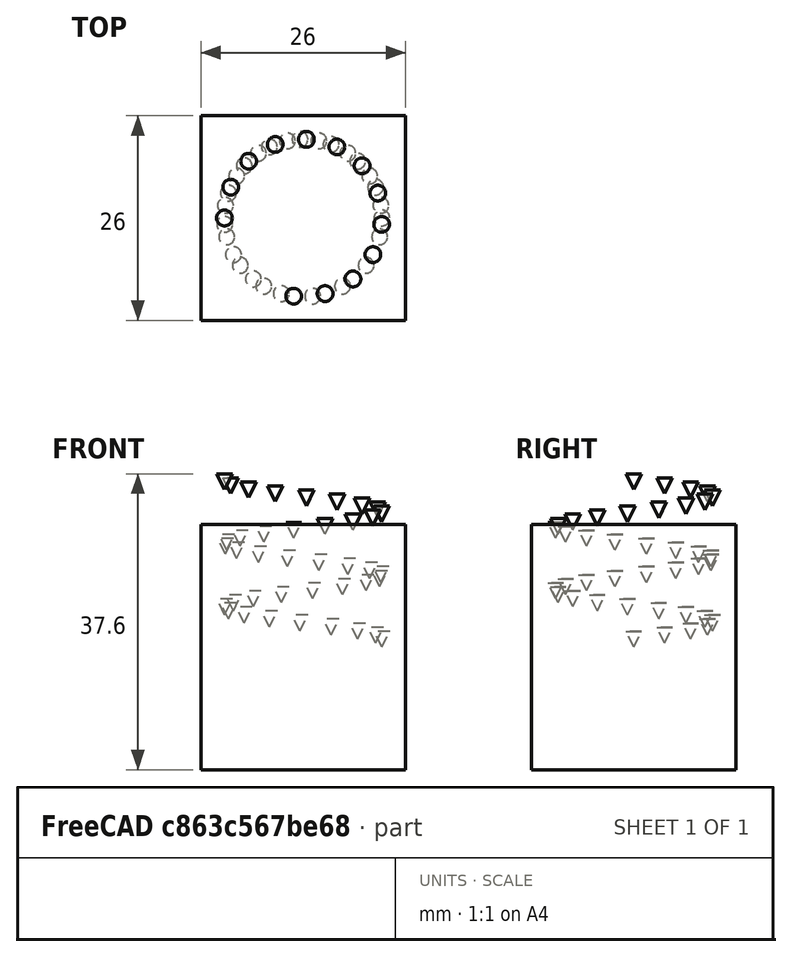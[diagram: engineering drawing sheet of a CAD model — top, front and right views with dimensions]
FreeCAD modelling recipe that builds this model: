
FCSTD DOCUMENT  (FreeCAD 0.21R33694 (Git))
Label: PathArray
License: All rights reserved
objects: App::DocumentObjectGroupPython×1251, Part::FeaturePython×2, App::Part×2, Part::Cone×1, Part::Helix×1
note: 4 computed .brp shape members not serialized (recipe doc carries the construction recipe); baked Part::Feature solids carry a one-line shape summary decoded from their .brp

FEATURE [App::DocumentObjectGroupPython] HALFPI  # scripted group (container) (typed FeaturePython)
  name = HALFPI
  value = pi/2.
FEATURE [App::DocumentObjectGroupPython] PI  # scripted group (container) (typed FeaturePython)
  name = PI
  value = 1.*pi
FEATURE [App::DocumentObjectGroupPython] TWOPI  # scripted group (container) (typed FeaturePython)
  name = TWOPI
  value = 2.*pi
FEATURE [App::DocumentObjectGroupPython] Constants  # scripted group (container) (typed FeaturePython)
  Group = -> [HALFPI,PI,TWOPI]
FEATURE [App::DocumentObjectGroupPython] Variables  # scripted group (container) (typed FeaturePython)
FEATURE [App::DocumentObjectGroupPython] Quantities  # scripted group (container) (typed FeaturePython)
FEATURE [App::DocumentObjectGroupPython] Isotopes  # scripted group (container) (typed FeaturePython)
FEATURE [App::DocumentObjectGroupPython] Elements  # scripted group (container) (typed FeaturePython)
FEATURE [App::DocumentObjectGroupPython] Matrix  # scripted group (container) (typed FeaturePython)
FEATURE [App::DocumentObjectGroupPython] Surfaces  # scripted group (container) (typed FeaturePython)
FEATURE [App::DocumentObjectGroupPython] Opticals  # scripted group (container) (typed FeaturePython)
  Group = -> [Matrix,Surfaces]
FEATURE [App::DocumentObjectGroupPython] G4Isotopes  # scripted group (container) (typed FeaturePython)
FEATURE [App::DocumentObjectGroupPython] H_element  # scripted group (container) (typed FeaturePython)
  Z = 1
  atom_value = 1.008
  formula = H
  name = H_element
FEATURE [App::DocumentObjectGroupPython] He_element  # scripted group (container) (typed FeaturePython)
  Z = 2
  atom_value = 4.0026
  formula = He
  name = He_element
FEATURE [App::DocumentObjectGroupPython] Li_element  # scripted group (container) (typed FeaturePython)
  Z = 3
  atom_value = 6.94
  formula = Li
  name = Li_element
FEATURE [App::DocumentObjectGroupPython] Be_element  # scripted group (container) (typed FeaturePython)
  Z = 4
  atom_value = 9.01218
  formula = Be
  name = Be_element
FEATURE [App::DocumentObjectGroupPython] B_element  # scripted group (container) (typed FeaturePython)
  Z = 5
  atom_value = 10.81
  formula = B
  name = B_element
FEATURE [App::DocumentObjectGroupPython] C_element  # scripted group (container) (typed FeaturePython)
  Z = 6
  atom_value = 12.011
  formula = C
  name = C_element
FEATURE [App::DocumentObjectGroupPython] N_element  # scripted group (container) (typed FeaturePython)
  Z = 7
  atom_value = 14.007
  formula = N
  name = N_element
FEATURE [App::DocumentObjectGroupPython] O_element  # scripted group (container) (typed FeaturePython)
  Z = 8
  atom_value = 15.999
  formula = O
  name = O_element
FEATURE [App::DocumentObjectGroupPython] F_element  # scripted group (container) (typed FeaturePython)
  Z = 9
  atom_value = 18.9984
  formula = F
  name = F_element
FEATURE [App::DocumentObjectGroupPython] Ne_element  # scripted group (container) (typed FeaturePython)
  Z = 10
  atom_value = 20.1797
  formula = Ne
  name = Ne_element
FEATURE [App::DocumentObjectGroupPython] Na_element  # scripted group (container) (typed FeaturePython)
  Z = 11
  atom_value = 22.9898
  formula = Na
  name = Na_element
FEATURE [App::DocumentObjectGroupPython] Mg_element  # scripted group (container) (typed FeaturePython)
  Z = 12
  atom_value = 24.305
  formula = Mg
  name = Mg_element
FEATURE [App::DocumentObjectGroupPython] Al_element  # scripted group (container) (typed FeaturePython)
  Z = 13
  atom_value = 26.9815
  formula = Al
  name = Al_element
FEATURE [App::DocumentObjectGroupPython] Si_element  # scripted group (container) (typed FeaturePython)
  Z = 14
  atom_value = 28.085
  formula = Si
  name = Si_element
FEATURE [App::DocumentObjectGroupPython] P_element  # scripted group (container) (typed FeaturePython)
  Z = 15
  atom_value = 30.9738
  formula = P
  name = P_element
FEATURE [App::DocumentObjectGroupPython] S_element  # scripted group (container) (typed FeaturePython)
  Z = 16
  atom_value = 32.06
  formula = S
  name = S_element
FEATURE [App::DocumentObjectGroupPython] Cl_element  # scripted group (container) (typed FeaturePython)
  Z = 17
  atom_value = 35.45
  formula = Cl
  name = Cl_element
FEATURE [App::DocumentObjectGroupPython] Ar_element  # scripted group (container) (typed FeaturePython)
  Z = 18
  atom_value = 39.95
  formula = Ar
  name = Ar_element
FEATURE [App::DocumentObjectGroupPython] K_element  # scripted group (container) (typed FeaturePython)
  Z = 19
  atom_value = 39.0983
  formula = K
  name = K_element
FEATURE [App::DocumentObjectGroupPython] Ca_element  # scripted group (container) (typed FeaturePython)
  Z = 20
  atom_value = 40.078
  formula = Ca
  name = Ca_element
FEATURE [App::DocumentObjectGroupPython] Sc_element  # scripted group (container) (typed FeaturePython)
  Z = 21
  atom_value = 44.9559
  formula = Sc
  name = Sc_element
FEATURE [App::DocumentObjectGroupPython] Ti_element  # scripted group (container) (typed FeaturePython)
  Z = 22
  atom_value = 47.867
  formula = Ti
  name = Ti_element
FEATURE [App::DocumentObjectGroupPython] V_element  # scripted group (container) (typed FeaturePython)
  Z = 23
  atom_value = 50.9415
  formula = V
  name = V_element
FEATURE [App::DocumentObjectGroupPython] Cr_element  # scripted group (container) (typed FeaturePython)
  Z = 24
  atom_value = 51.9961
  formula = Cr
  name = Cr_element
FEATURE [App::DocumentObjectGroupPython] Mn_element  # scripted group (container) (typed FeaturePython)
  Z = 25
  atom_value = 54.938
  formula = Mn
  name = Mn_element
FEATURE [App::DocumentObjectGroupPython] Fe_element  # scripted group (container) (typed FeaturePython)
  Z = 26
  atom_value = 55.845
  formula = Fe
  name = Fe_element
FEATURE [App::DocumentObjectGroupPython] Co_element  # scripted group (container) (typed FeaturePython)
  Z = 27
  atom_value = 58.9332
  formula = Co
  name = Co_element
FEATURE [App::DocumentObjectGroupPython] Ni_element  # scripted group (container) (typed FeaturePython)
  Z = 28
  atom_value = 58.6934
  formula = Ni
  name = Ni_element
FEATURE [App::DocumentObjectGroupPython] Cu_element  # scripted group (container) (typed FeaturePython)
  Z = 29
  atom_value = 63.546
  formula = Cu
  name = Cu_element
FEATURE [App::DocumentObjectGroupPython] Zn_element  # scripted group (container) (typed FeaturePython)
  Z = 30
  atom_value = 65.38
  formula = Zn
  name = Zn_element
FEATURE [App::DocumentObjectGroupPython] Ga_element  # scripted group (container) (typed FeaturePython)
  Z = 31
  atom_value = 69.723
  formula = Ga
  name = Ga_element
FEATURE [App::DocumentObjectGroupPython] Ge_element  # scripted group (container) (typed FeaturePython)
  Z = 32
  atom_value = 72.63
  formula = Ge
  name = Ge_element
FEATURE [App::DocumentObjectGroupPython] As_element  # scripted group (container) (typed FeaturePython)
  Z = 33
  atom_value = 74.9216
  formula = As
  name = As_element
FEATURE [App::DocumentObjectGroupPython] Se_element  # scripted group (container) (typed FeaturePython)
  Z = 34
  atom_value = 78.971
  formula = Se
  name = Se_element
FEATURE [App::DocumentObjectGroupPython] Br_element  # scripted group (container) (typed FeaturePython)
  Z = 35
  atom_value = 79.904
  formula = Br
  name = Br_element
FEATURE [App::DocumentObjectGroupPython] Kr_element  # scripted group (container) (typed FeaturePython)
  Z = 36
  atom_value = 83.798
  formula = Kr
  name = Kr_element
FEATURE [App::DocumentObjectGroupPython] Rb_element  # scripted group (container) (typed FeaturePython)
  Z = 37
  atom_value = 85.4678
  formula = Rb
  name = Rb_element
FEATURE [App::DocumentObjectGroupPython] Sr_element  # scripted group (container) (typed FeaturePython)
  Z = 38
  atom_value = 87.62
  formula = Sr
  name = Sr_element
FEATURE [App::DocumentObjectGroupPython] Y_element  # scripted group (container) (typed FeaturePython)
  Z = 39
  atom_value = 88.9058
  formula = Y
  name = Y_element
FEATURE [App::DocumentObjectGroupPython] Zr_element  # scripted group (container) (typed FeaturePython)
  Z = 40
  atom_value = 91.224
  formula = Zr
  name = Zr_element
FEATURE [App::DocumentObjectGroupPython] Nb_element  # scripted group (container) (typed FeaturePython)
  Z = 41
  atom_value = 92.9064
  formula = Nb
  name = Nb_element
FEATURE [App::DocumentObjectGroupPython] Mo_element  # scripted group (container) (typed FeaturePython)
  Z = 42
  atom_value = 95.95
  formula = Mo
  name = Mo_element
FEATURE [App::DocumentObjectGroupPython] Tc_element  # scripted group (container) (typed FeaturePython)
  Z = 43
  atom_value = 97
  formula = Tc
  name = Tc_element
FEATURE [App::DocumentObjectGroupPython] Ru_element  # scripted group (container) (typed FeaturePython)
  Z = 44
  atom_value = 101.07
  formula = Ru
  name = Ru_element
FEATURE [App::DocumentObjectGroupPython] Rh_element  # scripted group (container) (typed FeaturePython)
  Z = 45
  atom_value = 102.905
  formula = Rh
  name = Rh_element
FEATURE [App::DocumentObjectGroupPython] Pd_element  # scripted group (container) (typed FeaturePython)
  Z = 46
  atom_value = 106.42
  formula = Pd
  name = Pd_element
FEATURE [App::DocumentObjectGroupPython] Ag_element  # scripted group (container) (typed FeaturePython)
  Z = 47
  atom_value = 107.868
  formula = Ag
  name = Ag_element
FEATURE [App::DocumentObjectGroupPython] Cd_element  # scripted group (container) (typed FeaturePython)
  Z = 48
  atom_value = 112.414
  formula = Cd
  name = Cd_element
FEATURE [App::DocumentObjectGroupPython] In_element  # scripted group (container) (typed FeaturePython)
  Z = 49
  atom_value = 114.818
  formula = In
  name = In_element
FEATURE [App::DocumentObjectGroupPython] Sn_element  # scripted group (container) (typed FeaturePython)
  Z = 50
  atom_value = 118.71
  formula = Sn
  name = Sn_element
FEATURE [App::DocumentObjectGroupPython] Sb_element  # scripted group (container) (typed FeaturePython)
  Z = 51
  atom_value = 121.76
  formula = Sb
  name = Sb_element
FEATURE [App::DocumentObjectGroupPython] Te_element  # scripted group (container) (typed FeaturePython)
  Z = 52
  atom_value = 127.6
  formula = Te
  name = Te_element
FEATURE [App::DocumentObjectGroupPython] I_element  # scripted group (container) (typed FeaturePython)
  Z = 53
  atom_value = 126.904
  formula = I
  name = I_element
FEATURE [App::DocumentObjectGroupPython] Xe_element  # scripted group (container) (typed FeaturePython)
  Z = 54
  atom_value = 131.293
  formula = Xe
  name = Xe_element
FEATURE [App::DocumentObjectGroupPython] Cs_element  # scripted group (container) (typed FeaturePython)
  Z = 55
  atom_value = 132.905
  formula = Cs
  name = Cs_element
FEATURE [App::DocumentObjectGroupPython] Ba_element  # scripted group (container) (typed FeaturePython)
  Z = 56
  atom_value = 137.327
  formula = Ba
  name = Ba_element
FEATURE [App::DocumentObjectGroupPython] La_element  # scripted group (container) (typed FeaturePython)
  Z = 57
  atom_value = 138.905
  formula = La
  name = La_element
FEATURE [App::DocumentObjectGroupPython] Ce_element  # scripted group (container) (typed FeaturePython)
  Z = 58
  atom_value = 140.116
  formula = Ce
  name = Ce_element
FEATURE [App::DocumentObjectGroupPython] Pr_element  # scripted group (container) (typed FeaturePython)
  Z = 59
  atom_value = 140.908
  formula = Pr
  name = Pr_element
FEATURE [App::DocumentObjectGroupPython] Nd_element  # scripted group (container) (typed FeaturePython)
  Z = 60
  atom_value = 144.242
  formula = Nd
  name = Nd_element
FEATURE [App::DocumentObjectGroupPython] Pm_element  # scripted group (container) (typed FeaturePython)
  Z = 61
  atom_value = 145
  formula = Pm
  name = Pm_element
FEATURE [App::DocumentObjectGroupPython] Sm_element  # scripted group (container) (typed FeaturePython)
  Z = 62
  atom_value = 150.36
  formula = Sm
  name = Sm_element
FEATURE [App::DocumentObjectGroupPython] Eu_element  # scripted group (container) (typed FeaturePython)
  Z = 63
  atom_value = 151.964
  formula = Eu
  name = Eu_element
FEATURE [App::DocumentObjectGroupPython] Gd_element  # scripted group (container) (typed FeaturePython)
  Z = 64
  atom_value = 157.25
  formula = Gd
  name = Gd_element
FEATURE [App::DocumentObjectGroupPython] Tb_element  # scripted group (container) (typed FeaturePython)
  Z = 65
  atom_value = 158.925
  formula = Tb
  name = Tb_element
FEATURE [App::DocumentObjectGroupPython] Dy_element  # scripted group (container) (typed FeaturePython)
  Z = 66
  atom_value = 162.5
  formula = Dy
  name = Dy_element
FEATURE [App::DocumentObjectGroupPython] Ho_element  # scripted group (container) (typed FeaturePython)
  Z = 67
  atom_value = 164.93
  formula = Ho
  name = Ho_element
FEATURE [App::DocumentObjectGroupPython] Er_element  # scripted group (container) (typed FeaturePython)
  Z = 68
  atom_value = 167.259
  formula = Er
  name = Er_element
FEATURE [App::DocumentObjectGroupPython] Tm_element  # scripted group (container) (typed FeaturePython)
  Z = 69
  atom_value = 168.934
  formula = Tm
  name = Tm_element
FEATURE [App::DocumentObjectGroupPython] Yb_element  # scripted group (container) (typed FeaturePython)
  Z = 70
  atom_value = 173.045
  formula = Yb
  name = Yb_element
FEATURE [App::DocumentObjectGroupPython] Lu_element  # scripted group (container) (typed FeaturePython)
  Z = 71
  atom_value = 174.967
  formula = Lu
  name = Lu_element
FEATURE [App::DocumentObjectGroupPython] Hf_element  # scripted group (container) (typed FeaturePython)
  Z = 72
  atom_value = 178.49
  formula = Hf
  name = Hf_element
FEATURE [App::DocumentObjectGroupPython] Ta_element  # scripted group (container) (typed FeaturePython)
  Z = 73
  atom_value = 180.948
  formula = Ta
  name = Ta_element
FEATURE [App::DocumentObjectGroupPython] W_element  # scripted group (container) (typed FeaturePython)
  Z = 74
  atom_value = 183.84
  formula = W
  name = W_element
FEATURE [App::DocumentObjectGroupPython] Re_element  # scripted group (container) (typed FeaturePython)
  Z = 75
  atom_value = 186.207
  formula = Re
  name = Re_element
FEATURE [App::DocumentObjectGroupPython] Os_element  # scripted group (container) (typed FeaturePython)
  Z = 76
  atom_value = 190.23
  formula = Os
  name = Os_element
FEATURE [App::DocumentObjectGroupPython] Ir_element  # scripted group (container) (typed FeaturePython)
  Z = 77
  atom_value = 192.217
  formula = Ir
  name = Ir_element
FEATURE [App::DocumentObjectGroupPython] Pt_element  # scripted group (container) (typed FeaturePython)
  Z = 78
  atom_value = 195.084
  formula = Pt
  name = Pt_element
FEATURE [App::DocumentObjectGroupPython] Au_element  # scripted group (container) (typed FeaturePython)
  Z = 79
  atom_value = 196.967
  formula = Au
  name = Au_element
FEATURE [App::DocumentObjectGroupPython] Hg_element  # scripted group (container) (typed FeaturePython)
  Z = 80
  atom_value = 200.592
  formula = Hg
  name = Hg_element
FEATURE [App::DocumentObjectGroupPython] Tl_element  # scripted group (container) (typed FeaturePython)
  Z = 81
  atom_value = 204.38
  formula = Tl
  name = Tl_element
FEATURE [App::DocumentObjectGroupPython] Pb_element  # scripted group (container) (typed FeaturePython)
  Z = 82
  atom_value = 207.2
  formula = Pb
  name = Pb_element
FEATURE [App::DocumentObjectGroupPython] Bi_element  # scripted group (container) (typed FeaturePython)
  Z = 83
  atom_value = 208.98
  formula = Bi
  name = Bi_element
FEATURE [App::DocumentObjectGroupPython] Po_element  # scripted group (container) (typed FeaturePython)
  Z = 84
  atom_value = 209
  formula = Po
  name = Po_element
FEATURE [App::DocumentObjectGroupPython] At_element  # scripted group (container) (typed FeaturePython)
  Z = 85
  atom_value = 210
  formula = At
  name = At_element
FEATURE [App::DocumentObjectGroupPython] Rn_element  # scripted group (container) (typed FeaturePython)
  Z = 86
  atom_value = 222
  formula = Rn
  name = Rn_element
FEATURE [App::DocumentObjectGroupPython] Fr_element  # scripted group (container) (typed FeaturePython)
  Z = 87
  atom_value = 223
  formula = Fr
  name = Fr_element
FEATURE [App::DocumentObjectGroupPython] Ra_element  # scripted group (container) (typed FeaturePython)
  Z = 88
  atom_value = 226
  formula = Ra
  name = Ra_element
FEATURE [App::DocumentObjectGroupPython] Ac_element  # scripted group (container) (typed FeaturePython)
  Z = 89
  atom_value = 227
  formula = Ac
  name = Ac_element
FEATURE [App::DocumentObjectGroupPython] Th_element  # scripted group (container) (typed FeaturePython)
  Z = 90
  atom_value = 232.038
  formula = Th
  name = Th_element
FEATURE [App::DocumentObjectGroupPython] Pa_element  # scripted group (container) (typed FeaturePython)
  Z = 91
  atom_value = 231.036
  formula = Pa
  name = Pa_element
FEATURE [App::DocumentObjectGroupPython] U_element  # scripted group (container) (typed FeaturePython)
  Z = 92
  atom_value = 238.029
  formula = U
  name = U_element
FEATURE [App::DocumentObjectGroupPython] Np_element  # scripted group (container) (typed FeaturePython)
  Z = 93
  atom_value = 237
  formula = Np
  name = Np_element
FEATURE [App::DocumentObjectGroupPython] Pu_element  # scripted group (container) (typed FeaturePython)
  Z = 94
  atom_value = 244
  formula = Pu
  name = Pu_element
FEATURE [App::DocumentObjectGroupPython] Am_element  # scripted group (container) (typed FeaturePython)
  Z = 95
  atom_value = 243
  formula = Am
  name = Am_element
FEATURE [App::DocumentObjectGroupPython] Cm_element  # scripted group (container) (typed FeaturePython)
  Z = 96
  atom_value = 247
  formula = Cm
  name = Cm_element
FEATURE [App::DocumentObjectGroupPython] Bk_element  # scripted group (container) (typed FeaturePython)
  Z = 97
  atom_value = 247
  formula = Bk
  name = Bk_element
FEATURE [App::DocumentObjectGroupPython] Cf_element  # scripted group (container) (typed FeaturePython)
  Z = 98
  atom_value = 251
  formula = Cf
  name = Cf_element
FEATURE [App::DocumentObjectGroupPython] G4Elements  # scripted group (container) (typed FeaturePython)
  Group = -> [H_element,He_element,Li_element,Be_element,B_element,C_element,N_element,O_element,F_element,Ne_element,Na_element,Mg_element,Al_element,Si_element,P_element,S_element,Cl_element,Ar_element,K_element,Ca_element,Sc_element,Ti_element,V_element,Cr_element,Mn_element,Fe_element,Co_element,Ni_element,Cu_element,Zn_element,Ga_element,Ge_element,As_element,Se_element,Br_element,Kr_element,Rb_element,+61 more]
FEATURE [App::DocumentObjectGroupPython] H_element001  label="H_element : 0.101"  # scripted group (container) (typed FeaturePython)
  n = 0.101327
FEATURE [App::DocumentObjectGroupPython] C_element001  label="C_element : 0.775"  # scripted group (container) (typed FeaturePython)
  n = 0.7755
FEATURE [App::DocumentObjectGroupPython] N_element001  label="N_element : 0.035"  # scripted group (container) (typed FeaturePython)
  n = 0.035057
FEATURE [App::DocumentObjectGroupPython] O_element001  label="O_element : 0.052"  # scripted group (container) (typed FeaturePython)
  n = 0.0523159
FEATURE [App::DocumentObjectGroupPython] F_element001  label="F_element : 0.017"  # scripted group (container) (typed FeaturePython)
  n = 0.017422
FEATURE [App::DocumentObjectGroupPython] Ca_element001  label="Ca_element : 0.018"  # scripted group (container) (typed FeaturePython)
  n = 0.018378
FEATURE [App::DocumentObjectGroupPython] G4_A_150_TISSUE  label="G4_A-150_TISSUE"  # scripted group (container) (typed FeaturePython)
  Dunit = g/cm3
  Dvalue = 1.127
  Group = -> [H_element001,C_element001,N_element001,O_element001,F_element001,Ca_element001]
  conduct = 2
  density = 1
  expand = 3
  formula = G4_A-150_TISSUE
  name = G4_A-150_TISSUE
  specific = 4
FEATURE [App::DocumentObjectGroupPython] C_element002  label="C_element : 3"  # scripted group (container) (typed FeaturePython)
  n = 3
  ref = C_element
FEATURE [App::DocumentObjectGroupPython] H_element002  label="H_element : 6"  # scripted group (container) (typed FeaturePython)
  n = 6
  ref = H_element
FEATURE [App::DocumentObjectGroupPython] O_element002  label="O_element : 1"  # scripted group (container) (typed FeaturePython)
  n = 1
  ref = O_element
FEATURE [App::DocumentObjectGroupPython] G4_ACETONE  # scripted group (container) (typed FeaturePython)
  Dunit = g/cm3
  Dvalue = 0.7899
  Group = -> [C_element002,H_element002,O_element002]
  conduct = 2
  density = 1
  expand = 3
  formula = G4_ACETONE
  name = G4_ACETONE
  specific = 4
FEATURE [App::DocumentObjectGroupPython] C_element003  label="C_element : 2"  # scripted group (container) (typed FeaturePython)
  n = 2
  ref = C_element
FEATURE [App::DocumentObjectGroupPython] H_element003  label="H_element : 2"  # scripted group (container) (typed FeaturePython)
  n = 2
  ref = H_element
FEATURE [App::DocumentObjectGroupPython] G4_ACETYLENE  # scripted group (container) (typed FeaturePython)
  Dunit = g/cm3
  Dvalue = 0.0010967
  Group = -> [C_element003,H_element003]
  conduct = 2
  density = 1
  expand = 3
  formula = G4_ACETYLENE
  name = G4_ACETYLENE
  specific = 4
FEATURE [App::DocumentObjectGroupPython] C_element004  label="C_element : 5"  # scripted group (container) (typed FeaturePython)
  n = 5
  ref = C_element
FEATURE [App::DocumentObjectGroupPython] H_element004  label="H_element : 5"  # scripted group (container) (typed FeaturePython)
  n = 5
  ref = H_element
FEATURE [App::DocumentObjectGroupPython] N_element002  label="N_element : 5"  # scripted group (container) (typed FeaturePython)
  n = 5
  ref = N_element
FEATURE [App::DocumentObjectGroupPython] G4_ADENINE  # scripted group (container) (typed FeaturePython)
  Dunit = g/cm3
  Dvalue = 1.6
  Group = -> [C_element004,H_element004,N_element002]
  conduct = 2
  density = 1
  expand = 3
  formula = G4_ADENINE
  name = G4_ADENINE
  specific = 4
FEATURE [App::DocumentObjectGroupPython] H_element005  label="H_element : 0.114"  # scripted group (container) (typed FeaturePython)
  n = 0.114
FEATURE [App::DocumentObjectGroupPython] C_element005  label="C_element : 0.598"  # scripted group (container) (typed FeaturePython)
  n = 0.598
FEATURE [App::DocumentObjectGroupPython] N_element003  label="N_element : 0.007"  # scripted group (container) (typed FeaturePython)
  n = 0.007
FEATURE [App::DocumentObjectGroupPython] O_element003  label="O_element : 0.278"  # scripted group (container) (typed FeaturePython)
  n = 0.278
FEATURE [App::DocumentObjectGroupPython] Na_element001  label="Na_element : 0.001"  # scripted group (container) (typed FeaturePython)
  n = 0.001
FEATURE [App::DocumentObjectGroupPython] S_element001  label="S_element : 0.001"  # scripted group (container) (typed FeaturePython)
  n = 0.001
FEATURE [App::DocumentObjectGroupPython] Cl_element001  label="Cl_element : 0.001"  # scripted group (container) (typed FeaturePython)
  n = 0.001
FEATURE [App::DocumentObjectGroupPython] G4_ADIPOSE_TISSUE_ICRP  # scripted group (container) (typed FeaturePython)
  Dunit = g/cm3
  Dvalue = 0.95
  Group = -> [H_element005,C_element005,N_element003,O_element003,Na_element001,S_element001,Cl_element001]
  conduct = 2
  density = 1
  expand = 3
  formula = G4_ADIPOSE_TISSUE_ICRP
  name = G4_ADIPOSE_TISSUE_ICRP
  specific = 4
FEATURE [App::DocumentObjectGroupPython] C_element006  label="C_element : 0.000"  # scripted group (container) (typed FeaturePython)
  n = 0.000124
FEATURE [App::DocumentObjectGroupPython] N_element004  label="N_element : 0.755"  # scripted group (container) (typed FeaturePython)
  n = 0.755268
FEATURE [App::DocumentObjectGroupPython] O_element004  label="O_element : 0.232"  # scripted group (container) (typed FeaturePython)
  n = 0.231781
FEATURE [App::DocumentObjectGroupPython] Ar_element001  label="Ar_element : 0.013"  # scripted group (container) (typed FeaturePython)
  n = 0.012827
FEATURE [App::DocumentObjectGroupPython] G4_AIR  # scripted group (container) (typed FeaturePython)
  Dunit = g/cm3
  Dvalue = 0.00120479
  Group = -> [C_element006,N_element004,O_element004,Ar_element001]
  conduct = 2
  density = 1
  expand = 3
  formula = G4_AIR
  name = G4_AIR
  specific = 4
FEATURE [App::DocumentObjectGroupPython] C_element007  label="C_element : 006"  # scripted group (container) (typed FeaturePython)
  n = 3
  ref = C_element
FEATURE [App::DocumentObjectGroupPython] H_element006  label="H_element : 7"  # scripted group (container) (typed FeaturePython)
  n = 7
  ref = H_element
FEATURE [App::DocumentObjectGroupPython] N_element005  label="N_element : 1"  # scripted group (container) (typed FeaturePython)
  n = 1
  ref = N_element
FEATURE [App::DocumentObjectGroupPython] O_element005  label="O_element : 2"  # scripted group (container) (typed FeaturePython)
  n = 2
  ref = O_element
FEATURE [App::DocumentObjectGroupPython] G4_ALANINE  # scripted group (container) (typed FeaturePython)
  Dunit = g/cm3
  Dvalue = 1.42
  Group = -> [C_element007,H_element006,N_element005,O_element005]
  conduct = 2
  density = 1
  expand = 3
  formula = G4_ALANINE
  name = G4_ALANINE
  specific = 4
FEATURE [App::DocumentObjectGroupPython] Al_element001  label="Al_element : 2"  # scripted group (container) (typed FeaturePython)
  n = 2
  ref = Al_element
FEATURE [App::DocumentObjectGroupPython] O_element006  label="O_element : 3"  # scripted group (container) (typed FeaturePython)
  n = 3
  ref = O_element
FEATURE [App::DocumentObjectGroupPython] G4_ALUMINUM_OXIDE  # scripted group (container) (typed FeaturePython)
  Dunit = g/cm3
  Dvalue = 3.97
  Group = -> [Al_element001,O_element006]
  conduct = 2
  density = 1
  expand = 3
  formula = G4_ALUMINUM_OXIDE
  name = G4_ALUMINUM_OXIDE
  specific = 4
FEATURE [App::DocumentObjectGroupPython] H_element007  label="H_element : 0.106"  # scripted group (container) (typed FeaturePython)
  n = 0.10593
FEATURE [App::DocumentObjectGroupPython] C_element008  label="C_element : 0.789"  # scripted group (container) (typed FeaturePython)
  n = 0.788974
FEATURE [App::DocumentObjectGroupPython] O_element007  label="O_element : 0.105"  # scripted group (container) (typed FeaturePython)
  n = 0.105096
FEATURE [App::DocumentObjectGroupPython] G4_AMBER  # scripted group (container) (typed FeaturePython)
  Dunit = g/cm3
  Dvalue = 1.1
  Group = -> [H_element007,C_element008,O_element007]
  conduct = 2
  density = 1
  expand = 3
  formula = G4_AMBER
  name = G4_AMBER
  specific = 4
FEATURE [App::DocumentObjectGroupPython] N_element006  label="N_element : 006"  # scripted group (container) (typed FeaturePython)
  n = 1
  ref = N_element
FEATURE [App::DocumentObjectGroupPython] H_element008  label="H_element : 3"  # scripted group (container) (typed FeaturePython)
  n = 3
  ref = H_element
FEATURE [App::DocumentObjectGroupPython] G4_AMMONIA  # scripted group (container) (typed FeaturePython)
  Dunit = g/cm3
  Dvalue = 0.000826019
  Group = -> [N_element006,H_element008]
  conduct = 2
  density = 1
  expand = 3
  formula = G4_AMMONIA
  name = G4_AMMONIA
  specific = 4
FEATURE [App::DocumentObjectGroupPython] C_element009  label="C_element : 6"  # scripted group (container) (typed FeaturePython)
  n = 6
  ref = C_element
FEATURE [App::DocumentObjectGroupPython] H_element009  label="H_element : 008"  # scripted group (container) (typed FeaturePython)
  n = 7
  ref = H_element
FEATURE [App::DocumentObjectGroupPython] N_element007  label="N_element : 007"  # scripted group (container) (typed FeaturePython)
  n = 1
  ref = N_element
FEATURE [App::DocumentObjectGroupPython] G4_ANILINE  # scripted group (container) (typed FeaturePython)
  Dunit = g/cm3
  Dvalue = 1.0235
  Group = -> [C_element009,H_element009,N_element007]
  conduct = 2
  density = 1
  expand = 3
  formula = G4_ANILINE
  name = G4_ANILINE
  specific = 4
FEATURE [App::DocumentObjectGroupPython] C_element010  label="C_element : 14"  # scripted group (container) (typed FeaturePython)
  n = 14
  ref = C_element
FEATURE [App::DocumentObjectGroupPython] H_element010  label="H_element : 10"  # scripted group (container) (typed FeaturePython)
  n = 10
  ref = H_element
FEATURE [App::DocumentObjectGroupPython] G4_ANTHRACENE  # scripted group (container) (typed FeaturePython)
  Dunit = g/cm3
  Dvalue = 1.283
  Group = -> [C_element010,H_element010]
  conduct = 2
  density = 1
  expand = 3
  formula = G4_ANTHRACENE
  name = G4_ANTHRACENE
  specific = 4
FEATURE [App::DocumentObjectGroupPython] H_element011  label="H_element : 0.065"  # scripted group (container) (typed FeaturePython)
  n = 0.0654709
FEATURE [App::DocumentObjectGroupPython] C_element011  label="C_element : 0.537"  # scripted group (container) (typed FeaturePython)
  n = 0.536944
FEATURE [App::DocumentObjectGroupPython] N_element008  label="N_element : 0.021"  # scripted group (container) (typed FeaturePython)
  n = 0.0215
FEATURE [App::DocumentObjectGroupPython] O_element008  label="O_element : 0.032"  # scripted group (container) (typed FeaturePython)
  n = 0.032085
FEATURE [App::DocumentObjectGroupPython] F_element002  label="F_element : 0.167"  # scripted group (container) (typed FeaturePython)
  n = 0.167411
FEATURE [App::DocumentObjectGroupPython] Ca_element002  label="Ca_element : 0.177"  # scripted group (container) (typed FeaturePython)
  n = 0.176589
FEATURE [App::DocumentObjectGroupPython] G4_B_100_BONE  label="G4_B-100_BONE"  # scripted group (container) (typed FeaturePython)
  Dunit = g/cm3
  Dvalue = 1.45
  Group = -> [H_element011,C_element011,N_element008,O_element008,F_element002,Ca_element002]
  conduct = 2
  density = 1
  expand = 3
  formula = G4_B-100_BONE
  name = G4_B-100_BONE
  specific = 4
FEATURE [App::DocumentObjectGroupPython] H_element012  label="H_element : 0.057"  # scripted group (container) (typed FeaturePython)
  n = 0.057441
FEATURE [App::DocumentObjectGroupPython] C_element012  label="C_element : 0.790"  # scripted group (container) (typed FeaturePython)
  n = 0.774591
FEATURE [App::DocumentObjectGroupPython] O_element009  label="O_element : 0.168"  # scripted group (container) (typed FeaturePython)
  n = 0.167968
FEATURE [App::DocumentObjectGroupPython] G4_BAKELITE  # scripted group (container) (typed FeaturePython)
  Dunit = g/cm3
  Dvalue = 1.25
  Group = -> [H_element012,C_element012,O_element009]
  conduct = 2
  density = 1
  expand = 3
  formula = G4_BAKELITE
  name = G4_BAKELITE
  specific = 4
FEATURE [App::DocumentObjectGroupPython] Ba_element001  label="Ba_element : 1"  # scripted group (container) (typed FeaturePython)
  n = 1
  ref = Ba_element
FEATURE [App::DocumentObjectGroupPython] F_element003  label="F_element : 2"  # scripted group (container) (typed FeaturePython)
  n = 2
  ref = F_element
FEATURE [App::DocumentObjectGroupPython] G4_BARIUM_FLUORIDE  # scripted group (container) (typed FeaturePython)
  Dunit = g/cm3
  Dvalue = 4.89
  Group = -> [Ba_element001,F_element003]
  conduct = 2
  density = 1
  expand = 3
  formula = G4_BARIUM_FLUORIDE
  name = G4_BARIUM_FLUORIDE
  specific = 4
FEATURE [App::DocumentObjectGroupPython] Ba_element002  label="Ba_element : 002"  # scripted group (container) (typed FeaturePython)
  n = 1
  ref = Ba_element
FEATURE [App::DocumentObjectGroupPython] S_element002  label="S_element : 1"  # scripted group (container) (typed FeaturePython)
  n = 1
  ref = S_element
FEATURE [App::DocumentObjectGroupPython] O_element010  label="O_element : 4"  # scripted group (container) (typed FeaturePython)
  n = 4
  ref = O_element
FEATURE [App::DocumentObjectGroupPython] G4_BARIUM_SULFATE  # scripted group (container) (typed FeaturePython)
  Dunit = g/cm3
  Dvalue = 4.5
  Group = -> [Ba_element002,S_element002,O_element010]
  conduct = 2
  density = 1
  expand = 3
  formula = G4_BARIUM_SULFATE
  name = G4_BARIUM_SULFATE
  specific = 4
FEATURE [App::DocumentObjectGroupPython] C_element013  label="C_element : 007"  # scripted group (container) (typed FeaturePython)
  n = 6
  ref = C_element
FEATURE [App::DocumentObjectGroupPython] H_element013  label="H_element : 009"  # scripted group (container) (typed FeaturePython)
  n = 6
  ref = H_element
FEATURE [App::DocumentObjectGroupPython] G4_BENZENE  # scripted group (container) (typed FeaturePython)
  Dunit = g/cm3
  Dvalue = 0.87865
  Group = -> [C_element013,H_element013]
  conduct = 2
  density = 1
  expand = 3
  formula = G4_BENZENE
  name = G4_BENZENE
  specific = 4
FEATURE [App::DocumentObjectGroupPython] Be_element001  label="Be_element : 1"  # scripted group (container) (typed FeaturePython)
  n = 1
  ref = Be_element
FEATURE [App::DocumentObjectGroupPython] O_element011  label="O_element : 005"  # scripted group (container) (typed FeaturePython)
  n = 1
  ref = O_element
FEATURE [App::DocumentObjectGroupPython] G4_BERYLLIUM_OXIDE  # scripted group (container) (typed FeaturePython)
  Dunit = g/cm3
  Dvalue = 3.01
  Group = -> [Be_element001,O_element011]
  conduct = 2
  density = 1
  expand = 3
  formula = G4_BERYLLIUM_OXIDE
  name = G4_BERYLLIUM_OXIDE
  specific = 4
FEATURE [App::DocumentObjectGroupPython] Bi_element001  label="Bi_element : 4"  # scripted group (container) (typed FeaturePython)
  n = 4
  ref = Bi_element
FEATURE [App::DocumentObjectGroupPython] Ge_element001  label="Ge_element : 3"  # scripted group (container) (typed FeaturePython)
  n = 3
  ref = Ge_element
FEATURE [App::DocumentObjectGroupPython] O_element012  label="O_element : 12"  # scripted group (container) (typed FeaturePython)
  n = 12
  ref = O_element
FEATURE [App::DocumentObjectGroupPython] G4_BGO  # scripted group (container) (typed FeaturePython)
  Dunit = g/cm3
  Dvalue = 7.13
  Group = -> [Bi_element001,Ge_element001,O_element012]
  conduct = 2
  density = 1
  expand = 3
  formula = G4_BGO
  name = G4_BGO
  specific = 4
FEATURE [App::DocumentObjectGroupPython] H_element014  label="H_element : 0.102"  # scripted group (container) (typed FeaturePython)
  n = 0.102
FEATURE [App::DocumentObjectGroupPython] C_element014  label="C_element : 0.110"  # scripted group (container) (typed FeaturePython)
  n = 0.11
FEATURE [App::DocumentObjectGroupPython] N_element009  label="N_element : 0.033"  # scripted group (container) (typed FeaturePython)
  n = 0.033
FEATURE [App::DocumentObjectGroupPython] O_element013  label="O_element : 0.745"  # scripted group (container) (typed FeaturePython)
  n = 0.745
FEATURE [App::DocumentObjectGroupPython] Na_element002  label="Na_element : 0.002"  # scripted group (container) (typed FeaturePython)
  n = 0.001
FEATURE [App::DocumentObjectGroupPython] P_element001  label="P_element : 0.001"  # scripted group (container) (typed FeaturePython)
  n = 0.001
FEATURE [App::DocumentObjectGroupPython] S_element003  label="S_element : 0.002"  # scripted group (container) (typed FeaturePython)
  n = 0.002
FEATURE [App::DocumentObjectGroupPython] Cl_element002  label="Cl_element : 0.003"  # scripted group (container) (typed FeaturePython)
  n = 0.003
FEATURE [App::DocumentObjectGroupPython] K_element001  label="K_element : 0.002"  # scripted group (container) (typed FeaturePython)
  n = 0.002
FEATURE [App::DocumentObjectGroupPython] Fe_element001  label="Fe_element : 0.001"  # scripted group (container) (typed FeaturePython)
  n = 0.001
FEATURE [App::DocumentObjectGroupPython] G4_BLOOD_ICRP  # scripted group (container) (typed FeaturePython)
  Dunit = g/cm3
  Dvalue = 1.06
  Group = -> [H_element014,C_element014,N_element009,O_element013,Na_element002,P_element001,S_element003,Cl_element002,K_element001,Fe_element001]
  conduct = 2
  density = 1
  expand = 3
  formula = G4_BLOOD_ICRP
  name = G4_BLOOD_ICRP
  specific = 4
FEATURE [App::DocumentObjectGroupPython] H_element015  label="H_element : 0.064"  # scripted group (container) (typed FeaturePython)
  n = 0.064
FEATURE [App::DocumentObjectGroupPython] C_element015  label="C_element : 0.278"  # scripted group (container) (typed FeaturePython)
  n = 0.278
FEATURE [App::DocumentObjectGroupPython] N_element010  label="N_element : 0.027"  # scripted group (container) (typed FeaturePython)
  n = 0.027
FEATURE [App::DocumentObjectGroupPython] O_element014  label="O_element : 0.410"  # scripted group (container) (typed FeaturePython)
  n = 0.41
FEATURE [App::DocumentObjectGroupPython] Mg_element001  label="Mg_element : 0.002"  # scripted group (container) (typed FeaturePython)
  n = 0.002
FEATURE [App::DocumentObjectGroupPython] P_element002  label="P_element : 0.070"  # scripted group (container) (typed FeaturePython)
  n = 0.07
FEATURE [App::DocumentObjectGroupPython] S_element004  label="S_element : 0.003"  # scripted group (container) (typed FeaturePython)
  n = 0.002
FEATURE [App::DocumentObjectGroupPython] Ca_element003  label="Ca_element : 0.147"  # scripted group (container) (typed FeaturePython)
  n = 0.147
FEATURE [App::DocumentObjectGroupPython] G4_BONE_COMPACT_ICRU  # scripted group (container) (typed FeaturePython)
  Dunit = g/cm3
  Dvalue = 1.85
  Group = -> [H_element015,C_element015,N_element010,O_element014,Mg_element001,P_element002,S_element004,Ca_element003]
  conduct = 2
  density = 1
  expand = 3
  formula = G4_BONE_COMPACT_ICRU
  name = G4_BONE_COMPACT_ICRU
  specific = 4
FEATURE [App::DocumentObjectGroupPython] H_element016  label="H_element : 0.034"  # scripted group (container) (typed FeaturePython)
  n = 0.034
FEATURE [App::DocumentObjectGroupPython] C_element016  label="C_element : 0.155"  # scripted group (container) (typed FeaturePython)
  n = 0.155
FEATURE [App::DocumentObjectGroupPython] N_element011  label="N_element : 0.042"  # scripted group (container) (typed FeaturePython)
  n = 0.042
FEATURE [App::DocumentObjectGroupPython] O_element015  label="O_element : 0.435"  # scripted group (container) (typed FeaturePython)
  n = 0.435
FEATURE [App::DocumentObjectGroupPython] Na_element003  label="Na_element : 0.003"  # scripted group (container) (typed FeaturePython)
  n = 0.001
FEATURE [App::DocumentObjectGroupPython] Mg_element002  label="Mg_element : 0.003"  # scripted group (container) (typed FeaturePython)
  n = 0.002
FEATURE [App::DocumentObjectGroupPython] P_element003  label="P_element : 0.103"  # scripted group (container) (typed FeaturePython)
  n = 0.103
FEATURE [App::DocumentObjectGroupPython] S_element005  label="S_element : 0.004"  # scripted group (container) (typed FeaturePython)
  n = 0.003
FEATURE [App::DocumentObjectGroupPython] Ca_element004  label="Ca_element : 0.225"  # scripted group (container) (typed FeaturePython)
  n = 0.225
FEATURE [App::DocumentObjectGroupPython] G4_BONE_CORTICAL_ICRP  # scripted group (container) (typed FeaturePython)
  Dunit = g/cm3
  Dvalue = 1.92
  Group = -> [H_element016,C_element016,N_element011,O_element015,Na_element003,Mg_element002,P_element003,S_element005,Ca_element004]
  conduct = 2
  density = 1
  expand = 3
  formula = G4_BONE_CORTICAL_ICRP
  name = G4_BONE_CORTICAL_ICRP
  specific = 4
FEATURE [App::DocumentObjectGroupPython] B_element001  label="B_element : 4"  # scripted group (container) (typed FeaturePython)
  n = 4
  ref = B_element
FEATURE [App::DocumentObjectGroupPython] C_element017  label="C_element : 1"  # scripted group (container) (typed FeaturePython)
  n = 1
  ref = C_element
FEATURE [App::DocumentObjectGroupPython] G4_BORON_CARBIDE  # scripted group (container) (typed FeaturePython)
  Dunit = g/cm3
  Dvalue = 2.52
  Group = -> [B_element001,C_element017]
  conduct = 2
  density = 1
  expand = 3
  formula = G4_BORON_CARBIDE
  name = G4_BORON_CARBIDE
  specific = 4
FEATURE [App::DocumentObjectGroupPython] B_element002  label="B_element : 2"  # scripted group (container) (typed FeaturePython)
  n = 2
  ref = B_element
FEATURE [App::DocumentObjectGroupPython] O_element016  label="O_element : 006"  # scripted group (container) (typed FeaturePython)
  n = 3
  ref = O_element
FEATURE [App::DocumentObjectGroupPython] G4_BORON_OXIDE  # scripted group (container) (typed FeaturePython)
  Dunit = g/cm3
  Dvalue = 1.812
  Group = -> [B_element002,O_element016]
  conduct = 2
  density = 1
  expand = 3
  formula = G4_BORON_OXIDE
  name = G4_BORON_OXIDE
  specific = 4
FEATURE [App::DocumentObjectGroupPython] H_element017  label="H_element : 0.107"  # scripted group (container) (typed FeaturePython)
  n = 0.107
FEATURE [App::DocumentObjectGroupPython] C_element018  label="C_element : 0.145"  # scripted group (container) (typed FeaturePython)
  n = 0.145
FEATURE [App::DocumentObjectGroupPython] N_element012  label="N_element : 0.022"  # scripted group (container) (typed FeaturePython)
  n = 0.022
FEATURE [App::DocumentObjectGroupPython] O_element017  label="O_element : 0.712"  # scripted group (container) (typed FeaturePython)
  n = 0.712
FEATURE [App::DocumentObjectGroupPython] Na_element004  label="Na_element : 0.004"  # scripted group (container) (typed FeaturePython)
  n = 0.002
FEATURE [App::DocumentObjectGroupPython] P_element004  label="P_element : 0.004"  # scripted group (container) (typed FeaturePython)
  n = 0.004
FEATURE [App::DocumentObjectGroupPython] S_element006  label="S_element : 0.005"  # scripted group (container) (typed FeaturePython)
  n = 0.002
FEATURE [App::DocumentObjectGroupPython] Cl_element003  label="Cl_element : 0.004"  # scripted group (container) (typed FeaturePython)
  n = 0.003
FEATURE [App::DocumentObjectGroupPython] K_element002  label="K_element : 0.003"  # scripted group (container) (typed FeaturePython)
  n = 0.003
FEATURE [App::DocumentObjectGroupPython] G4_BRAIN_ICRP  # scripted group (container) (typed FeaturePython)
  Dunit = g/cm3
  Dvalue = 1.04
  Group = -> [H_element017,C_element018,N_element012,O_element017,Na_element004,P_element004,S_element006,Cl_element003,K_element002]
  conduct = 2
  density = 1
  expand = 3
  formula = G4_BRAIN_ICRP
  name = G4_BRAIN_ICRP
  specific = 4
FEATURE [App::DocumentObjectGroupPython] C_element019  label="C_element : 4"  # scripted group (container) (typed FeaturePython)
  n = 4
  ref = C_element
FEATURE [App::DocumentObjectGroupPython] H_element018  label="H_element : 010"  # scripted group (container) (typed FeaturePython)
  n = 10
  ref = H_element
FEATURE [App::DocumentObjectGroupPython] G4_BUTANE  # scripted group (container) (typed FeaturePython)
  Dunit = g/cm3
  Dvalue = 0.00249343
  Group = -> [C_element019,H_element018]
  conduct = 2
  density = 1
  expand = 3
  formula = G4_BUTANE
  name = G4_BUTANE
  specific = 4
FEATURE [App::DocumentObjectGroupPython] C_element020  label="C_element : 008"  # scripted group (container) (typed FeaturePython)
  n = 4
  ref = C_element
FEATURE [App::DocumentObjectGroupPython] H_element019  label="H_element : 011"  # scripted group (container) (typed FeaturePython)
  n = 10
  ref = H_element
FEATURE [App::DocumentObjectGroupPython] O_element018  label="O_element : 007"  # scripted group (container) (typed FeaturePython)
  n = 1
  ref = O_element
FEATURE [App::DocumentObjectGroupPython] G4_N_BUTYL_ALCOHOL  label="G4_N-BUTYL_ALCOHOL"  # scripted group (container) (typed FeaturePython)
  Dunit = g/cm3
  Dvalue = 0.8098
  Group = -> [C_element020,H_element019,O_element018]
  conduct = 2
  density = 1
  expand = 3
  formula = G4_N-BUTYL_ALCOHOL
  name = G4_N-BUTYL_ALCOHOL
  specific = 4
FEATURE [App::DocumentObjectGroupPython] H_element020  label="H_element : 0.025"  # scripted group (container) (typed FeaturePython)
  n = 0.02468
FEATURE [App::DocumentObjectGroupPython] C_element021  label="C_element : 0.502"  # scripted group (container) (typed FeaturePython)
  n = 0.501611
FEATURE [App::DocumentObjectGroupPython] O_element019  label="O_element : 0.005"  # scripted group (container) (typed FeaturePython)
  n = 0.004527
FEATURE [App::DocumentObjectGroupPython] F_element004  label="F_element : 0.465"  # scripted group (container) (typed FeaturePython)
  n = 0.465209
FEATURE [App::DocumentObjectGroupPython] Si_element001  label="Si_element : 0.004"  # scripted group (container) (typed FeaturePython)
  n = 0.003973
FEATURE [App::DocumentObjectGroupPython] G4_C_552  label="G4_C-552"  # scripted group (container) (typed FeaturePython)
  Dunit = g/cm3
  Dvalue = 1.76
  Group = -> [H_element020,C_element021,O_element019,F_element004,Si_element001]
  conduct = 2
  density = 1
  expand = 3
  formula = G4_C-552
  name = G4_C-552
  specific = 4
FEATURE [App::DocumentObjectGroupPython] Cd_element001  label="Cd_element : 1"  # scripted group (container) (typed FeaturePython)
  n = 1
  ref = Cd_element
FEATURE [App::DocumentObjectGroupPython] Te_element001  label="Te_element : 1"  # scripted group (container) (typed FeaturePython)
  n = 1
  ref = Te_element
FEATURE [App::DocumentObjectGroupPython] G4_CADMIUM_TELLURIDE  # scripted group (container) (typed FeaturePython)
  Dunit = g/cm3
  Dvalue = 6.2
  Group = -> [Cd_element001,Te_element001]
  conduct = 2
  density = 1
  expand = 3
  formula = G4_CADMIUM_TELLURIDE
  name = G4_CADMIUM_TELLURIDE
  specific = 4
FEATURE [App::DocumentObjectGroupPython] Cd_element002  label="Cd_element : 002"  # scripted group (container) (typed FeaturePython)
  n = 1
  ref = Cd_element
FEATURE [App::DocumentObjectGroupPython] W_element001  label="W_element : 1"  # scripted group (container) (typed FeaturePython)
  n = 1
  ref = W_element
FEATURE [App::DocumentObjectGroupPython] O_element020  label="O_element : 008"  # scripted group (container) (typed FeaturePython)
  n = 4
  ref = O_element
FEATURE [App::DocumentObjectGroupPython] G4_CADMIUM_TUNGSTATE  # scripted group (container) (typed FeaturePython)
  Dunit = g/cm3
  Dvalue = 7.9
  Group = -> [Cd_element002,W_element001,O_element020]
  conduct = 2
  density = 1
  expand = 3
  formula = G4_CADMIUM_TUNGSTATE
  name = G4_CADMIUM_TUNGSTATE
  specific = 4
FEATURE [App::DocumentObjectGroupPython] Ca_element005  label="Ca_element : 1"  # scripted group (container) (typed FeaturePython)
  n = 1
  ref = Ca_element
FEATURE [App::DocumentObjectGroupPython] C_element022  label="C_element : 009"  # scripted group (container) (typed FeaturePython)
  n = 1
  ref = C_element
FEATURE [App::DocumentObjectGroupPython] O_element021  label="O_element : 009"  # scripted group (container) (typed FeaturePython)
  n = 3
  ref = O_element
FEATURE [App::DocumentObjectGroupPython] G4_CALCIUM_CARBONATE  # scripted group (container) (typed FeaturePython)
  Dunit = g/cm3
  Dvalue = 2.8
  Group = -> [Ca_element005,C_element022,O_element021]
  conduct = 2
  density = 1
  expand = 3
  formula = G4_CALCIUM_CARBONATE
  name = G4_CALCIUM_CARBONATE
  specific = 4
FEATURE [App::DocumentObjectGroupPython] Ca_element006  label="Ca_element : 002"  # scripted group (container) (typed FeaturePython)
  n = 1
  ref = Ca_element
FEATURE [App::DocumentObjectGroupPython] F_element005  label="F_element : 003"  # scripted group (container) (typed FeaturePython)
  n = 2
  ref = F_element
FEATURE [App::DocumentObjectGroupPython] G4_CALCIUM_FLUORIDE  # scripted group (container) (typed FeaturePython)
  Dunit = g/cm3
  Dvalue = 3.18
  Group = -> [Ca_element006,F_element005]
  conduct = 2
  density = 1
  expand = 3
  formula = G4_CALCIUM_FLUORIDE
  name = G4_CALCIUM_FLUORIDE
  specific = 4
FEATURE [App::DocumentObjectGroupPython] Ca_element007  label="Ca_element : 003"  # scripted group (container) (typed FeaturePython)
  n = 1
  ref = Ca_element
FEATURE [App::DocumentObjectGroupPython] O_element022  label="O_element : 010"  # scripted group (container) (typed FeaturePython)
  n = 1
  ref = O_element
FEATURE [App::DocumentObjectGroupPython] G4_CALCIUM_OXIDE  # scripted group (container) (typed FeaturePython)
  Dunit = g/cm3
  Dvalue = 3.3
  Group = -> [Ca_element007,O_element022]
  conduct = 2
  density = 1
  expand = 3
  formula = G4_CALCIUM_OXIDE
  name = G4_CALCIUM_OXIDE
  specific = 4
FEATURE [App::DocumentObjectGroupPython] Ca_element008  label="Ca_element : 004"  # scripted group (container) (typed FeaturePython)
  n = 1
  ref = Ca_element
FEATURE [App::DocumentObjectGroupPython] S_element007  label="S_element : 002"  # scripted group (container) (typed FeaturePython)
  n = 1
  ref = S_element
FEATURE [App::DocumentObjectGroupPython] O_element023  label="O_element : 011"  # scripted group (container) (typed FeaturePython)
  n = 4
  ref = O_element
FEATURE [App::DocumentObjectGroupPython] G4_CALCIUM_SULFATE  # scripted group (container) (typed FeaturePython)
  Dunit = g/cm3
  Dvalue = 2.96
  Group = -> [Ca_element008,S_element007,O_element023]
  conduct = 2
  density = 1
  expand = 3
  formula = G4_CALCIUM_SULFATE
  name = G4_CALCIUM_SULFATE
  specific = 4
FEATURE [App::DocumentObjectGroupPython] Ca_element009  label="Ca_element : 005"  # scripted group (container) (typed FeaturePython)
  n = 1
  ref = Ca_element
FEATURE [App::DocumentObjectGroupPython] W_element002  label="W_element : 002"  # scripted group (container) (typed FeaturePython)
  n = 1
  ref = W_element
FEATURE [App::DocumentObjectGroupPython] O_element024  label="O_element : 012"  # scripted group (container) (typed FeaturePython)
  n = 4
  ref = O_element
FEATURE [App::DocumentObjectGroupPython] G4_CALCIUM_TUNGSTATE  # scripted group (container) (typed FeaturePython)
  Dunit = g/cm3
  Dvalue = 6.062
  Group = -> [Ca_element009,W_element002,O_element024]
  conduct = 2
  density = 1
  expand = 3
  formula = G4_CALCIUM_TUNGSTATE
  name = G4_CALCIUM_TUNGSTATE
  specific = 4
FEATURE [App::DocumentObjectGroupPython] C_element023  label="C_element : 010"  # scripted group (container) (typed FeaturePython)
  n = 1
  ref = C_element
FEATURE [App::DocumentObjectGroupPython] O_element025  label="O_element : 013"  # scripted group (container) (typed FeaturePython)
  n = 2
  ref = O_element
FEATURE [App::DocumentObjectGroupPython] G4_CARBON_DIOXIDE  # scripted group (container) (typed FeaturePython)
  Dunit = g/cm3
  Dvalue = 0.00184212
  Group = -> [C_element023,O_element025]
  conduct = 2
  density = 1
  expand = 3
  formula = G4_CARBON_DIOXIDE
  name = G4_CARBON_DIOXIDE
  specific = 4
FEATURE [App::DocumentObjectGroupPython] C_element024  label="C_element : 011"  # scripted group (container) (typed FeaturePython)
  n = 1
  ref = C_element
FEATURE [App::DocumentObjectGroupPython] Cl_element004  label="Cl_element : 4"  # scripted group (container) (typed FeaturePython)
  n = 4
  ref = Cl_element
FEATURE [App::DocumentObjectGroupPython] G4_CARBON_TETRACHLORIDE  # scripted group (container) (typed FeaturePython)
  Dunit = g/cm3
  Dvalue = 1.594
  Group = -> [C_element024,Cl_element004]
  conduct = 2
  density = 1
  expand = 3
  formula = G4_CARBON_TETRACHLORIDE
  name = G4_CARBON_TETRACHLORIDE
  specific = 4
FEATURE [App::DocumentObjectGroupPython] C_element025  label="C_element : 012"  # scripted group (container) (typed FeaturePython)
  n = 6
  ref = C_element
FEATURE [App::DocumentObjectGroupPython] H_element021  label="H_element : 012"  # scripted group (container) (typed FeaturePython)
  n = 10
  ref = H_element
FEATURE [App::DocumentObjectGroupPython] O_element026  label="O_element : 5"  # scripted group (container) (typed FeaturePython)
  n = 5
  ref = O_element
FEATURE [App::DocumentObjectGroupPython] G4_CELLULOSE_CELLOPHANE  # scripted group (container) (typed FeaturePython)
  Dunit = g/cm3
  Dvalue = 1.42
  Group = -> [C_element025,H_element021,O_element026]
  conduct = 2
  density = 1
  expand = 3
  formula = G4_CELLULOSE_CELLOPHANE
  name = G4_CELLULOSE_CELLOPHANE
  specific = 4
FEATURE [App::DocumentObjectGroupPython] H_element022  label="H_element : 0.067"  # scripted group (container) (typed FeaturePython)
  n = 0.067125
FEATURE [App::DocumentObjectGroupPython] C_element026  label="C_element : 0.545"  # scripted group (container) (typed FeaturePython)
  n = 0.545403
FEATURE [App::DocumentObjectGroupPython] O_element027  label="O_element : 0.387"  # scripted group (container) (typed FeaturePython)
  n = 0.387472
FEATURE [App::DocumentObjectGroupPython] G4_CELLULOSE_BUTYRATE  # scripted group (container) (typed FeaturePython)
  Dunit = g/cm3
  Dvalue = 1.2
  Group = -> [H_element022,C_element026,O_element027]
  conduct = 2
  density = 1
  expand = 3
  formula = G4_CELLULOSE_BUTYRATE
  name = G4_CELLULOSE_BUTYRATE
  specific = 4
FEATURE [App::DocumentObjectGroupPython] H_element023  label="H_element : 0.029"  # scripted group (container) (typed FeaturePython)
  n = 0.029216
FEATURE [App::DocumentObjectGroupPython] C_element027  label="C_element : 0.271"  # scripted group (container) (typed FeaturePython)
  n = 0.271296
FEATURE [App::DocumentObjectGroupPython] N_element013  label="N_element : 0.121"  # scripted group (container) (typed FeaturePython)
  n = 0.121276
FEATURE [App::DocumentObjectGroupPython] O_element028  label="O_element : 0.578"  # scripted group (container) (typed FeaturePython)
  n = 0.578212
FEATURE [App::DocumentObjectGroupPython] G4_CELLULOSE_NITRATE  # scripted group (container) (typed FeaturePython)
  Dunit = g/cm3
  Dvalue = 1.49
  Group = -> [H_element023,C_element027,N_element013,O_element028]
  conduct = 2
  density = 1
  expand = 3
  formula = G4_CELLULOSE_NITRATE
  name = G4_CELLULOSE_NITRATE
  specific = 4
FEATURE [App::DocumentObjectGroupPython] H_element024  label="H_element : 0.108"  # scripted group (container) (typed FeaturePython)
  n = 0.107596
FEATURE [App::DocumentObjectGroupPython] N_element014  label="N_element : 0.001"  # scripted group (container) (typed FeaturePython)
  n = 0.0008
FEATURE [App::DocumentObjectGroupPython] O_element029  label="O_element : 0.875"  # scripted group (container) (typed FeaturePython)
  n = 0.874976
FEATURE [App::DocumentObjectGroupPython] S_element008  label="S_element : 0.015"  # scripted group (container) (typed FeaturePython)
  n = 0.014627
FEATURE [App::DocumentObjectGroupPython] Ce_element001  label="Ce_element : 0.002"  # scripted group (container) (typed FeaturePython)
  n = 0.002001
FEATURE [App::DocumentObjectGroupPython] G4_CERIC_SULFATE  # scripted group (container) (typed FeaturePython)
  Dunit = g/cm3
  Dvalue = 1.03
  Group = -> [H_element024,N_element014,O_element029,S_element008,Ce_element001]
  conduct = 2
  density = 1
  expand = 3
  formula = G4_CERIC_SULFATE
  name = G4_CERIC_SULFATE
  specific = 4
FEATURE [App::DocumentObjectGroupPython] Cs_element001  label="Cs_element : 1"  # scripted group (container) (typed FeaturePython)
  n = 1
  ref = Cs_element
FEATURE [App::DocumentObjectGroupPython] F_element006  label="F_element : 1"  # scripted group (container) (typed FeaturePython)
  n = 1
  ref = F_element
FEATURE [App::DocumentObjectGroupPython] G4_CESIUM_FLUORIDE  # scripted group (container) (typed FeaturePython)
  Dunit = g/cm3
  Dvalue = 4.115
  Group = -> [Cs_element001,F_element006]
  conduct = 2
  density = 1
  expand = 3
  formula = G4_CESIUM_FLUORIDE
  name = G4_CESIUM_FLUORIDE
  specific = 4
FEATURE [App::DocumentObjectGroupPython] Cs_element002  label="Cs_element : 002"  # scripted group (container) (typed FeaturePython)
  n = 1
  ref = Cs_element
FEATURE [App::DocumentObjectGroupPython] I_element001  label="I_element : 1"  # scripted group (container) (typed FeaturePython)
  n = 1
  ref = I_element
FEATURE [App::DocumentObjectGroupPython] G4_CESIUM_IODIDE  # scripted group (container) (typed FeaturePython)
  Dunit = g/cm3
  Dvalue = 4.51
  Group = -> [Cs_element002,I_element001]
  conduct = 2
  density = 1
  expand = 3
  formula = G4_CESIUM_IODIDE
  name = G4_CESIUM_IODIDE
  specific = 4
FEATURE [App::DocumentObjectGroupPython] C_element028  label="C_element : 013"  # scripted group (container) (typed FeaturePython)
  n = 6
  ref = C_element
FEATURE [App::DocumentObjectGroupPython] H_element025  label="H_element : 013"  # scripted group (container) (typed FeaturePython)
  n = 5
  ref = H_element
FEATURE [App::DocumentObjectGroupPython] Cl_element005  label="Cl_element : 1"  # scripted group (container) (typed FeaturePython)
  n = 1
  ref = Cl_element
FEATURE [App::DocumentObjectGroupPython] G4_CHLOROBENZENE  # scripted group (container) (typed FeaturePython)
  Dunit = g/cm3
  Dvalue = 1.1058
  Group = -> [C_element028,H_element025,Cl_element005]
  conduct = 2
  density = 1
  expand = 3
  formula = G4_CHLOROBENZENE
  name = G4_CHLOROBENZENE
  specific = 4
FEATURE [App::DocumentObjectGroupPython] C_element029  label="C_element : 014"  # scripted group (container) (typed FeaturePython)
  n = 1
  ref = C_element
FEATURE [App::DocumentObjectGroupPython] H_element026  label="H_element : 1"  # scripted group (container) (typed FeaturePython)
  n = 1
  ref = H_element
FEATURE [App::DocumentObjectGroupPython] Cl_element006  label="Cl_element : 3"  # scripted group (container) (typed FeaturePython)
  n = 3
  ref = Cl_element
FEATURE [App::DocumentObjectGroupPython] G4_CHLOROFORM  # scripted group (container) (typed FeaturePython)
  Dunit = g/cm3
  Dvalue = 1.4832
  Group = -> [C_element029,H_element026,Cl_element006]
  conduct = 2
  density = 1
  expand = 3
  formula = G4_CHLOROFORM
  name = G4_CHLOROFORM
  specific = 4
FEATURE [App::DocumentObjectGroupPython] H_element027  label="H_element : 0.010"  # scripted group (container) (typed FeaturePython)
  n = 0.01
FEATURE [App::DocumentObjectGroupPython] C_element030  label="C_element : 0.001"  # scripted group (container) (typed FeaturePython)
  n = 0.001
FEATURE [App::DocumentObjectGroupPython] O_element030  label="O_element : 0.529"  # scripted group (container) (typed FeaturePython)
  n = 0.529107
FEATURE [App::DocumentObjectGroupPython] Na_element005  label="Na_element : 0.016"  # scripted group (container) (typed FeaturePython)
  n = 0.016
FEATURE [App::DocumentObjectGroupPython] Mg_element003  label="Mg_element : 0.004"  # scripted group (container) (typed FeaturePython)
  n = 0.002
FEATURE [App::DocumentObjectGroupPython] Al_element002  label="Al_element : 0.034"  # scripted group (container) (typed FeaturePython)
  n = 0.033872
FEATURE [App::DocumentObjectGroupPython] Si_element002  label="Si_element : 0.337"  # scripted group (container) (typed FeaturePython)
  n = 0.337021
FEATURE [App::DocumentObjectGroupPython] K_element003  label="K_element : 0.013"  # scripted group (container) (typed FeaturePython)
  n = 0.013
FEATURE [App::DocumentObjectGroupPython] Ca_element010  label="Ca_element : 0.044"  # scripted group (container) (typed FeaturePython)
  n = 0.044
FEATURE [App::DocumentObjectGroupPython] Fe_element002  label="Fe_element : 0.014"  # scripted group (container) (typed FeaturePython)
  n = 0.014
FEATURE [App::DocumentObjectGroupPython] G4_CONCRETE  # scripted group (container) (typed FeaturePython)
  Dunit = g/cm3
  Dvalue = 2.3
  Group = -> [H_element027,C_element030,O_element030,Na_element005,Mg_element003,Al_element002,Si_element002,K_element003,Ca_element010,Fe_element002]
  conduct = 2
  density = 1
  expand = 3
  formula = G4_CONCRETE
  name = G4_CONCRETE
  specific = 4
FEATURE [App::DocumentObjectGroupPython] C_element031  label="C_element : 015"  # scripted group (container) (typed FeaturePython)
  n = 6
  ref = C_element
FEATURE [App::DocumentObjectGroupPython] H_element028  label="H_element : 12"  # scripted group (container) (typed FeaturePython)
  n = 12
  ref = H_element
FEATURE [App::DocumentObjectGroupPython] G4_CYCLOHEXANE  # scripted group (container) (typed FeaturePython)
  Dunit = g/cm3
  Dvalue = 0.779
  Group = -> [C_element031,H_element028]
  conduct = 2
  density = 1
  expand = 3
  formula = G4_CYCLOHEXANE
  name = G4_CYCLOHEXANE
  specific = 4
FEATURE [App::DocumentObjectGroupPython] C_element032  label="C_element : 016"  # scripted group (container) (typed FeaturePython)
  n = 6
  ref = C_element
FEATURE [App::DocumentObjectGroupPython] H_element029  label="H_element : 4"  # scripted group (container) (typed FeaturePython)
  n = 4
  ref = H_element
FEATURE [App::DocumentObjectGroupPython] Cl_element007  label="Cl_element : 2"  # scripted group (container) (typed FeaturePython)
  n = 2
  ref = Cl_element
FEATURE [App::DocumentObjectGroupPython] G4_1_2_DICHLOROBENZENE  label="G4_1.2-DICHLOROBENZENE"  # scripted group (container) (typed FeaturePython)
  Dunit = g/cm3
  Dvalue = 1.3048
  Group = -> [C_element032,H_element029,Cl_element007]
  conduct = 2
  density = 1
  expand = 3
  formula = G4_1.2-DICHLOROBENZENE
  name = G4_1.2-DICHLOROBENZENE
  specific = 4
FEATURE [App::DocumentObjectGroupPython] C_element033  label="C_element : 017"  # scripted group (container) (typed FeaturePython)
  n = 4
  ref = C_element
FEATURE [App::DocumentObjectGroupPython] H_element030  label="H_element : 8"  # scripted group (container) (typed FeaturePython)
  n = 8
  ref = H_element
FEATURE [App::DocumentObjectGroupPython] O_element031  label="O_element : 014"  # scripted group (container) (typed FeaturePython)
  n = 1
  ref = O_element
FEATURE [App::DocumentObjectGroupPython] Cl_element008  label="Cl_element : 005"  # scripted group (container) (typed FeaturePython)
  n = 2
  ref = Cl_element
FEATURE [App::DocumentObjectGroupPython] G4_DICHLORODIETHYL_ETHER  # scripted group (container) (typed FeaturePython)
  Dunit = g/cm3
  Dvalue = 1.2199
  Group = -> [C_element033,H_element030,O_element031,Cl_element008]
  conduct = 2
  density = 1
  expand = 3
  formula = G4_DICHLORODIETHYL_ETHER
  name = G4_DICHLORODIETHYL_ETHER
  specific = 4
FEATURE [App::DocumentObjectGroupPython] C_element034  label="C_element : 018"  # scripted group (container) (typed FeaturePython)
  n = 2
  ref = C_element
FEATURE [App::DocumentObjectGroupPython] H_element031  label="H_element : 014"  # scripted group (container) (typed FeaturePython)
  n = 4
  ref = H_element
FEATURE [App::DocumentObjectGroupPython] Cl_element009  label="Cl_element : 006"  # scripted group (container) (typed FeaturePython)
  n = 2
  ref = Cl_element
FEATURE [App::DocumentObjectGroupPython] G4_1_2_DICHLOROETHANE  label="G4_1.2-DICHLOROETHANE"  # scripted group (container) (typed FeaturePython)
  Dunit = g/cm3
  Dvalue = 1.2351
  Group = -> [C_element034,H_element031,Cl_element009]
  conduct = 2
  density = 1
  expand = 3
  formula = G4_1.2-DICHLOROETHANE
  name = G4_1.2-DICHLOROETHANE
  specific = 4
FEATURE [App::DocumentObjectGroupPython] C_element035  label="C_element : 019"  # scripted group (container) (typed FeaturePython)
  n = 4
  ref = C_element
FEATURE [App::DocumentObjectGroupPython] H_element032  label="H_element : 015"  # scripted group (container) (typed FeaturePython)
  n = 10
  ref = H_element
FEATURE [App::DocumentObjectGroupPython] O_element032  label="O_element : 015"  # scripted group (container) (typed FeaturePython)
  n = 1
  ref = O_element
FEATURE [App::DocumentObjectGroupPython] G4_DIETHYL_ETHER  # scripted group (container) (typed FeaturePython)
  Dunit = g/cm3
  Dvalue = 0.71378
  Group = -> [C_element035,H_element032,O_element032]
  conduct = 2
  density = 1
  expand = 3
  formula = G4_DIETHYL_ETHER
  name = G4_DIETHYL_ETHER
  specific = 4
FEATURE [App::DocumentObjectGroupPython] C_element036  label="C_element : 020"  # scripted group (container) (typed FeaturePython)
  n = 3
  ref = C_element
FEATURE [App::DocumentObjectGroupPython] H_element033  label="H_element : 016"  # scripted group (container) (typed FeaturePython)
  n = 7
  ref = H_element
FEATURE [App::DocumentObjectGroupPython] N_element015  label="N_element : 008"  # scripted group (container) (typed FeaturePython)
  n = 1
  ref = N_element
FEATURE [App::DocumentObjectGroupPython] O_element033  label="O_element : 016"  # scripted group (container) (typed FeaturePython)
  n = 1
  ref = O_element
FEATURE [App::DocumentObjectGroupPython] G4_N_N_DIMETHYL_FORMAMIDE  label="G4_N.N-DIMETHYL_FORMAMIDE"  # scripted group (container) (typed FeaturePython)
  Dunit = g/cm3
  Dvalue = 0.9487
  Group = -> [C_element036,H_element033,N_element015,O_element033]
  conduct = 2
  density = 1
  expand = 3
  formula = G4_N.N-DIMETHYL_FORMAMIDE
  name = G4_N.N-DIMETHYL_FORMAMIDE
  specific = 4
FEATURE [App::DocumentObjectGroupPython] C_element037  label="C_element : 021"  # scripted group (container) (typed FeaturePython)
  n = 2
  ref = C_element
FEATURE [App::DocumentObjectGroupPython] H_element034  label="H_element : 017"  # scripted group (container) (typed FeaturePython)
  n = 6
  ref = H_element
FEATURE [App::DocumentObjectGroupPython] O_element034  label="O_element : 017"  # scripted group (container) (typed FeaturePython)
  n = 1
  ref = O_element
FEATURE [App::DocumentObjectGroupPython] S_element009  label="S_element : 003"  # scripted group (container) (typed FeaturePython)
  n = 1
  ref = S_element
FEATURE [App::DocumentObjectGroupPython] G4_DIMETHYL_SULFOXIDE  # scripted group (container) (typed FeaturePython)
  Dunit = g/cm3
  Dvalue = 1.1014
  Group = -> [C_element037,H_element034,O_element034,S_element009]
  conduct = 2
  density = 1
  expand = 3
  formula = G4_DIMETHYL_SULFOXIDE
  name = G4_DIMETHYL_SULFOXIDE
  specific = 4
FEATURE [App::DocumentObjectGroupPython] C_element038  label="C_element : 022"  # scripted group (container) (typed FeaturePython)
  n = 2
  ref = C_element
FEATURE [App::DocumentObjectGroupPython] H_element035  label="H_element : 018"  # scripted group (container) (typed FeaturePython)
  n = 6
  ref = H_element
FEATURE [App::DocumentObjectGroupPython] G4_ETHANE  # scripted group (container) (typed FeaturePython)
  Dunit = g/cm3
  Dvalue = 0.00125324
  Group = -> [C_element038,H_element035]
  conduct = 2
  density = 1
  expand = 3
  formula = G4_ETHANE
  name = G4_ETHANE
  specific = 4
FEATURE [App::DocumentObjectGroupPython] C_element039  label="C_element : 023"  # scripted group (container) (typed FeaturePython)
  n = 2
  ref = C_element
FEATURE [App::DocumentObjectGroupPython] H_element036  label="H_element : 019"  # scripted group (container) (typed FeaturePython)
  n = 6
  ref = H_element
FEATURE [App::DocumentObjectGroupPython] O_element035  label="O_element : 018"  # scripted group (container) (typed FeaturePython)
  n = 1
  ref = O_element
FEATURE [App::DocumentObjectGroupPython] G4_ETHYL_ALCOHOL  # scripted group (container) (typed FeaturePython)
  Dunit = g/cm3
  Dvalue = 0.7893
  Group = -> [C_element039,H_element036,O_element035]
  conduct = 2
  density = 1
  expand = 3
  formula = G4_ETHYL_ALCOHOL
  name = G4_ETHYL_ALCOHOL
  specific = 4
FEATURE [App::DocumentObjectGroupPython] H_element037  label="H_element : 0.090"  # scripted group (container) (typed FeaturePython)
  n = 0.090027
FEATURE [App::DocumentObjectGroupPython] C_element040  label="C_element : 0.585"  # scripted group (container) (typed FeaturePython)
  n = 0.585182
FEATURE [App::DocumentObjectGroupPython] O_element036  label="O_element : 0.325"  # scripted group (container) (typed FeaturePython)
  n = 0.324791
FEATURE [App::DocumentObjectGroupPython] G4_ETHYL_CELLULOSE  # scripted group (container) (typed FeaturePython)
  Dunit = g/cm3
  Dvalue = 1.13
  Group = -> [H_element037,C_element040,O_element036]
  conduct = 2
  density = 1
  expand = 3
  formula = G4_ETHYL_CELLULOSE
  name = G4_ETHYL_CELLULOSE
  specific = 4
FEATURE [App::DocumentObjectGroupPython] C_element041  label="C_element : 024"  # scripted group (container) (typed FeaturePython)
  n = 2
  ref = C_element
FEATURE [App::DocumentObjectGroupPython] H_element038  label="H_element : 020"  # scripted group (container) (typed FeaturePython)
  n = 4
  ref = H_element
FEATURE [App::DocumentObjectGroupPython] G4_ETHYLENE  # scripted group (container) (typed FeaturePython)
  Dunit = g/cm3
  Dvalue = 0.00117497
  Group = -> [C_element041,H_element038]
  conduct = 2
  density = 1
  expand = 3
  formula = G4_ETHYLENE
  name = G4_ETHYLENE
  specific = 4
FEATURE [App::DocumentObjectGroupPython] H_element039  label="H_element : 0.096"  # scripted group (container) (typed FeaturePython)
  n = 0.096
FEATURE [App::DocumentObjectGroupPython] C_element042  label="C_element : 0.195"  # scripted group (container) (typed FeaturePython)
  n = 0.195
FEATURE [App::DocumentObjectGroupPython] N_element016  label="N_element : 0.057"  # scripted group (container) (typed FeaturePython)
  n = 0.057
FEATURE [App::DocumentObjectGroupPython] O_element037  label="O_element : 0.646"  # scripted group (container) (typed FeaturePython)
  n = 0.646
FEATURE [App::DocumentObjectGroupPython] Na_element006  label="Na_element : 0.017"  # scripted group (container) (typed FeaturePython)
  n = 0.001
FEATURE [App::DocumentObjectGroupPython] P_element005  label="P_element : 0.104"  # scripted group (container) (typed FeaturePython)
  n = 0.001
FEATURE [App::DocumentObjectGroupPython] S_element010  label="S_element : 0.016"  # scripted group (container) (typed FeaturePython)
  n = 0.003
FEATURE [App::DocumentObjectGroupPython] Cl_element010  label="Cl_element : 0.005"  # scripted group (container) (typed FeaturePython)
  n = 0.001
FEATURE [App::DocumentObjectGroupPython] G4_EYE_LENS_ICRP  # scripted group (container) (typed FeaturePython)
  Dunit = g/cm3
  Dvalue = 1.07
  Group = -> [H_element039,C_element042,N_element016,O_element037,Na_element006,P_element005,S_element010,Cl_element010]
  conduct = 2
  density = 1
  expand = 3
  formula = G4_EYE_LENS_ICRP
  name = G4_EYE_LENS_ICRP
  specific = 4
FEATURE [App::DocumentObjectGroupPython] Fe_element003  label="Fe_element : 2"  # scripted group (container) (typed FeaturePython)
  n = 2
  ref = Fe_element
FEATURE [App::DocumentObjectGroupPython] O_element038  label="O_element : 019"  # scripted group (container) (typed FeaturePython)
  n = 3
  ref = O_element
FEATURE [App::DocumentObjectGroupPython] G4_FERRIC_OXIDE  # scripted group (container) (typed FeaturePython)
  Dunit = g/cm3
  Dvalue = 5.2
  Group = -> [Fe_element003,O_element038]
  conduct = 2
  density = 1
  expand = 3
  formula = G4_FERRIC_OXIDE
  name = G4_FERRIC_OXIDE
  specific = 4
FEATURE [App::DocumentObjectGroupPython] Fe_element004  label="Fe_element : 1"  # scripted group (container) (typed FeaturePython)
  n = 1
  ref = Fe_element
FEATURE [App::DocumentObjectGroupPython] B_element003  label="B_element : 1"  # scripted group (container) (typed FeaturePython)
  n = 1
  ref = B_element
FEATURE [App::DocumentObjectGroupPython] G4_FERROBORIDE  # scripted group (container) (typed FeaturePython)
  Dunit = g/cm3
  Dvalue = 7.15
  Group = -> [Fe_element004,B_element003]
  conduct = 2
  density = 1
  expand = 3
  formula = G4_FERROBORIDE
  name = G4_FERROBORIDE
  specific = 4
FEATURE [App::DocumentObjectGroupPython] Fe_element005  label="Fe_element : 003"  # scripted group (container) (typed FeaturePython)
  n = 1
  ref = Fe_element
FEATURE [App::DocumentObjectGroupPython] O_element039  label="O_element : 020"  # scripted group (container) (typed FeaturePython)
  n = 1
  ref = O_element
FEATURE [App::DocumentObjectGroupPython] G4_FERROUS_OXIDE  # scripted group (container) (typed FeaturePython)
  Dunit = g/cm3
  Dvalue = 5.7
  Group = -> [Fe_element005,O_element039]
  conduct = 2
  density = 1
  expand = 3
  formula = G4_FERROUS_OXIDE
  name = G4_FERROUS_OXIDE
  specific = 4
FEATURE [App::DocumentObjectGroupPython] H_element040  label="H_element : 0.115"  # scripted group (container) (typed FeaturePython)
  n = 0.108259
FEATURE [App::DocumentObjectGroupPython] N_element017  label="N_element : 0.000"  # scripted group (container) (typed FeaturePython)
  n = 2.7e-05
FEATURE [App::DocumentObjectGroupPython] O_element040  label="O_element : 0.879"  # scripted group (container) (typed FeaturePython)
  n = 0.878636
FEATURE [App::DocumentObjectGroupPython] Na_element007  label="Na_element : 0.000"  # scripted group (container) (typed FeaturePython)
  n = 2.2e-05
FEATURE [App::DocumentObjectGroupPython] S_element011  label="S_element : 0.013"  # scripted group (container) (typed FeaturePython)
  n = 0.012968
FEATURE [App::DocumentObjectGroupPython] Cl_element011  label="Cl_element : 0.000"  # scripted group (container) (typed FeaturePython)
  n = 3.4e-05
FEATURE [App::DocumentObjectGroupPython] Fe_element006  label="Fe_element : 0.000"  # scripted group (container) (typed FeaturePython)
  n = 5.4e-05
FEATURE [App::DocumentObjectGroupPython] G4_FERROUS_SULFATE  # scripted group (container) (typed FeaturePython)
  Dunit = g/cm3
  Dvalue = 1.024
  Group = -> [H_element040,N_element017,O_element040,Na_element007,S_element011,Cl_element011,Fe_element006]
  conduct = 2
  density = 1
  expand = 3
  formula = G4_FERROUS_SULFATE
  name = G4_FERROUS_SULFATE
  specific = 4
FEATURE [App::DocumentObjectGroupPython] C_element043  label="C_element : 0.099"  # scripted group (container) (typed FeaturePython)
  n = 0.099335
FEATURE [App::DocumentObjectGroupPython] F_element007  label="F_element : 0.314"  # scripted group (container) (typed FeaturePython)
  n = 0.314247
FEATURE [App::DocumentObjectGroupPython] Cl_element012  label="Cl_element : 0.586"  # scripted group (container) (typed FeaturePython)
  n = 0.586418
FEATURE [App::DocumentObjectGroupPython] G4_FREON_12  label="G4_FREON-12"  # scripted group (container) (typed FeaturePython)
  Dunit = g/cm3
  Dvalue = 1.12
  Group = -> [C_element043,F_element007,Cl_element012]
  conduct = 2
  density = 1
  expand = 3
  formula = G4_FREON-12
  name = G4_FREON-12
  specific = 4
FEATURE [App::DocumentObjectGroupPython] C_element044  label="C_element : 0.057"  # scripted group (container) (typed FeaturePython)
  n = 0.057245
FEATURE [App::DocumentObjectGroupPython] F_element008  label="F_element : 0.181"  # scripted group (container) (typed FeaturePython)
  n = 0.181096
FEATURE [App::DocumentObjectGroupPython] Br_element001  label="Br_element : 0.762"  # scripted group (container) (typed FeaturePython)
  n = 0.761659
FEATURE [App::DocumentObjectGroupPython] G4_FREON_12B2  label="G4_FREON-12B2"  # scripted group (container) (typed FeaturePython)
  Dunit = g/cm3
  Dvalue = 1.8
  Group = -> [C_element044,F_element008,Br_element001]
  conduct = 2
  density = 1
  expand = 3
  formula = G4_FREON-12B2
  name = G4_FREON-12B2
  specific = 4
FEATURE [App::DocumentObjectGroupPython] C_element045  label="C_element : 0.115"  # scripted group (container) (typed FeaturePython)
  n = 0.114983
FEATURE [App::DocumentObjectGroupPython] F_element009  label="F_element : 0.546"  # scripted group (container) (typed FeaturePython)
  n = 0.545621
FEATURE [App::DocumentObjectGroupPython] Cl_element013  label="Cl_element : 0.339"  # scripted group (container) (typed FeaturePython)
  n = 0.339396
FEATURE [App::DocumentObjectGroupPython] G4_FREON_13  label="G4_FREON-13"  # scripted group (container) (typed FeaturePython)
  Dunit = g/cm3
  Dvalue = 0.95
  Group = -> [C_element045,F_element009,Cl_element013]
  conduct = 2
  density = 1
  expand = 3
  formula = G4_FREON-13
  name = G4_FREON-13
  specific = 4
FEATURE [App::DocumentObjectGroupPython] C_element046  label="C_element : 025"  # scripted group (container) (typed FeaturePython)
  n = 1
  ref = C_element
FEATURE [App::DocumentObjectGroupPython] F_element010  label="F_element : 3"  # scripted group (container) (typed FeaturePython)
  n = 3
  ref = F_element
FEATURE [App::DocumentObjectGroupPython] Br_element002  label="Br_element : 1"  # scripted group (container) (typed FeaturePython)
  n = 1
  ref = Br_element
FEATURE [App::DocumentObjectGroupPython] G4_FREON_13B1  label="G4_FREON-13B1"  # scripted group (container) (typed FeaturePython)
  Dunit = g/cm3
  Dvalue = 1.5
  Group = -> [C_element046,F_element010,Br_element002]
  conduct = 2
  density = 1
  expand = 3
  formula = G4_FREON-13B1
  name = G4_FREON-13B1
  specific = 4
FEATURE [App::DocumentObjectGroupPython] C_element047  label="C_element : 0.061"  # scripted group (container) (typed FeaturePython)
  n = 0.061309
FEATURE [App::DocumentObjectGroupPython] F_element011  label="F_element : 0.291"  # scripted group (container) (typed FeaturePython)
  n = 0.290924
FEATURE [App::DocumentObjectGroupPython] I_element002  label="I_element : 0.648"  # scripted group (container) (typed FeaturePython)
  n = 0.647767
FEATURE [App::DocumentObjectGroupPython] G4_FREON_13I1  label="G4_FREON-13I1"  # scripted group (container) (typed FeaturePython)
  Dunit = g/cm3
  Dvalue = 1.8
  Group = -> [C_element047,F_element011,I_element002]
  conduct = 2
  density = 1
  expand = 3
  formula = G4_FREON-13I1
  name = G4_FREON-13I1
  specific = 4
FEATURE [App::DocumentObjectGroupPython] Gd_element001  label="Gd_element : 2"  # scripted group (container) (typed FeaturePython)
  n = 2
  ref = Gd_element
FEATURE [App::DocumentObjectGroupPython] O_element041  label="O_element : 021"  # scripted group (container) (typed FeaturePython)
  n = 2
  ref = O_element
FEATURE [App::DocumentObjectGroupPython] S_element012  label="S_element : 004"  # scripted group (container) (typed FeaturePython)
  n = 1
  ref = S_element
FEATURE [App::DocumentObjectGroupPython] G4_GADOLINIUM_OXYSULFIDE  # scripted group (container) (typed FeaturePython)
  Dunit = g/cm3
  Dvalue = 7.44
  Group = -> [Gd_element001,O_element041,S_element012]
  conduct = 2
  density = 1
  expand = 3
  formula = G4_GADOLINIUM_OXYSULFIDE
  name = G4_GADOLINIUM_OXYSULFIDE
  specific = 4
FEATURE [App::DocumentObjectGroupPython] Ga_element001  label="Ga_element : 1"  # scripted group (container) (typed FeaturePython)
  n = 1
  ref = Ga_element
FEATURE [App::DocumentObjectGroupPython] As_element001  label="As_element : 1"  # scripted group (container) (typed FeaturePython)
  n = 1
  ref = As_element
FEATURE [App::DocumentObjectGroupPython] G4_GALLIUM_ARSENIDE  # scripted group (container) (typed FeaturePython)
  Dunit = g/cm3
  Dvalue = 5.31
  Group = -> [Ga_element001,As_element001]
  conduct = 2
  density = 1
  expand = 3
  formula = G4_GALLIUM_ARSENIDE
  name = G4_GALLIUM_ARSENIDE
  specific = 4
FEATURE [App::DocumentObjectGroupPython] H_element041  label="H_element : 0.081"  # scripted group (container) (typed FeaturePython)
  n = 0.08118
FEATURE [App::DocumentObjectGroupPython] C_element048  label="C_element : 0.416"  # scripted group (container) (typed FeaturePython)
  n = 0.41606
FEATURE [App::DocumentObjectGroupPython] N_element018  label="N_element : 0.111"  # scripted group (container) (typed FeaturePython)
  n = 0.11124
FEATURE [App::DocumentObjectGroupPython] O_element042  label="O_element : 0.381"  # scripted group (container) (typed FeaturePython)
  n = 0.38064
FEATURE [App::DocumentObjectGroupPython] S_element013  label="S_element : 0.011"  # scripted group (container) (typed FeaturePython)
  n = 0.01088
FEATURE [App::DocumentObjectGroupPython] G4_GEL_PHOTO_EMULSION  # scripted group (container) (typed FeaturePython)
  Dunit = g/cm3
  Dvalue = 1.2914
  Group = -> [H_element041,C_element048,N_element018,O_element042,S_element013]
  conduct = 2
  density = 1
  expand = 3
  formula = G4_GEL_PHOTO_EMULSION
  name = G4_GEL_PHOTO_EMULSION
  specific = 4
FEATURE [App::DocumentObjectGroupPython] B_element004  label="B_element : 0.040"  # scripted group (container) (typed FeaturePython)
  n = 0.0400639
FEATURE [App::DocumentObjectGroupPython] O_element043  label="O_element : 0.540"  # scripted group (container) (typed FeaturePython)
  n = 0.539561
FEATURE [App::DocumentObjectGroupPython] Na_element008  label="Na_element : 0.028"  # scripted group (container) (typed FeaturePython)
  n = 0.0281909
FEATURE [App::DocumentObjectGroupPython] Al_element003  label="Al_element : 0.012"  # scripted group (container) (typed FeaturePython)
  n = 0.011644
FEATURE [App::DocumentObjectGroupPython] Si_element003  label="Si_element : 0.377"  # scripted group (container) (typed FeaturePython)
  n = 0.377219
FEATURE [App::DocumentObjectGroupPython] K_element004  label="K_element : 0.014"  # scripted group (container) (typed FeaturePython)
  n = 0.00332099
FEATURE [App::DocumentObjectGroupPython] G4_Pyrex_Glass  # scripted group (container) (typed FeaturePython)
  Dunit = g/cm3
  Dvalue = 2.23
  Group = -> [B_element004,O_element043,Na_element008,Al_element003,Si_element003,K_element004]
  conduct = 2
  density = 1
  expand = 3
  formula = G4_Pyrex_Glass
  name = G4_Pyrex_Glass
  specific = 4
FEATURE [App::DocumentObjectGroupPython] O_element044  label="O_element : 0.156"  # scripted group (container) (typed FeaturePython)
  n = 0.156453
FEATURE [App::DocumentObjectGroupPython] Si_element004  label="Si_element : 0.081"  # scripted group (container) (typed FeaturePython)
  n = 0.080866
FEATURE [App::DocumentObjectGroupPython] Ti_element001  label="Ti_element : 0.008"  # scripted group (container) (typed FeaturePython)
  n = 0.008092
FEATURE [App::DocumentObjectGroupPython] As_element002  label="As_element : 0.003"  # scripted group (container) (typed FeaturePython)
  n = 0.002651
FEATURE [App::DocumentObjectGroupPython] Pb_element001  label="Pb_element : 0.752"  # scripted group (container) (typed FeaturePython)
  n = 0.751938
FEATURE [App::DocumentObjectGroupPython] G4_GLASS_LEAD  # scripted group (container) (typed FeaturePython)
  Dunit = g/cm3
  Dvalue = 6.22
  Group = -> [O_element044,Si_element004,Ti_element001,As_element002,Pb_element001]
  conduct = 2
  density = 1
  expand = 3
  formula = G4_GLASS_LEAD
  name = G4_GLASS_LEAD
  specific = 4
FEATURE [App::DocumentObjectGroupPython] O_element045  label="O_element : 0.460"  # scripted group (container) (typed FeaturePython)
  n = 0.4598
FEATURE [App::DocumentObjectGroupPython] Na_element009  label="Na_element : 0.096"  # scripted group (container) (typed FeaturePython)
  n = 0.0964411
FEATURE [App::DocumentObjectGroupPython] Si_element005  label="Si_element : 0.378"  # scripted group (container) (typed FeaturePython)
  n = 0.336553
FEATURE [App::DocumentObjectGroupPython] Ca_element011  label="Ca_element : 0.107"  # scripted group (container) (typed FeaturePython)
  n = 0.107205
FEATURE [App::DocumentObjectGroupPython] G4_GLASS_PLATE  # scripted group (container) (typed FeaturePython)
  Dunit = g/cm3
  Dvalue = 2.4
  Group = -> [O_element045,Na_element009,Si_element005,Ca_element011]
  conduct = 2
  density = 1
  expand = 3
  formula = G4_GLASS_PLATE
  name = G4_GLASS_PLATE
  specific = 4
FEATURE [App::DocumentObjectGroupPython] C_element049  label="C_element : 026"  # scripted group (container) (typed FeaturePython)
  n = 5
  ref = C_element
FEATURE [App::DocumentObjectGroupPython] H_element042  label="H_element : 021"  # scripted group (container) (typed FeaturePython)
  n = 10
  ref = H_element
FEATURE [App::DocumentObjectGroupPython] N_element019  label="N_element : 2"  # scripted group (container) (typed FeaturePython)
  n = 2
  ref = N_element
FEATURE [App::DocumentObjectGroupPython] O_element046  label="O_element : 022"  # scripted group (container) (typed FeaturePython)
  n = 3
  ref = O_element
FEATURE [App::DocumentObjectGroupPython] G4_GLUTAMINE  # scripted group (container) (typed FeaturePython)
  Dunit = g/cm3
  Dvalue = 1.46
  Group = -> [C_element049,H_element042,N_element019,O_element046]
  conduct = 2
  density = 1
  expand = 3
  formula = G4_GLUTAMINE
  name = G4_GLUTAMINE
  specific = 4
FEATURE [App::DocumentObjectGroupPython] C_element050  label="C_element : 027"  # scripted group (container) (typed FeaturePython)
  n = 3
  ref = C_element
FEATURE [App::DocumentObjectGroupPython] H_element043  label="H_element : 022"  # scripted group (container) (typed FeaturePython)
  n = 8
  ref = H_element
FEATURE [App::DocumentObjectGroupPython] O_element047  label="O_element : 023"  # scripted group (container) (typed FeaturePython)
  n = 3
  ref = O_element
FEATURE [App::DocumentObjectGroupPython] G4_GLYCEROL  # scripted group (container) (typed FeaturePython)
  Dunit = g/cm3
  Dvalue = 1.2613
  Group = -> [C_element050,H_element043,O_element047]
  conduct = 2
  density = 1
  expand = 3
  formula = G4_GLYCEROL
  name = G4_GLYCEROL
  specific = 4
FEATURE [App::DocumentObjectGroupPython] C_element051  label="C_element : 028"  # scripted group (container) (typed FeaturePython)
  n = 5
  ref = C_element
FEATURE [App::DocumentObjectGroupPython] H_element044  label="H_element : 023"  # scripted group (container) (typed FeaturePython)
  n = 5
  ref = H_element
FEATURE [App::DocumentObjectGroupPython] N_element020  label="N_element : 009"  # scripted group (container) (typed FeaturePython)
  n = 5
  ref = N_element
FEATURE [App::DocumentObjectGroupPython] O_element048  label="O_element : 024"  # scripted group (container) (typed FeaturePython)
  n = 1
  ref = O_element
FEATURE [App::DocumentObjectGroupPython] G4_GUANINE  # scripted group (container) (typed FeaturePython)
  Dunit = g/cm3
  Dvalue = 2.2
  Group = -> [C_element051,H_element044,N_element020,O_element048]
  conduct = 2
  density = 1
  expand = 3
  formula = G4_GUANINE
  name = G4_GUANINE
  specific = 4
FEATURE [App::DocumentObjectGroupPython] Ca_element012  label="Ca_element : 006"  # scripted group (container) (typed FeaturePython)
  n = 1
  ref = Ca_element
FEATURE [App::DocumentObjectGroupPython] S_element014  label="S_element : 005"  # scripted group (container) (typed FeaturePython)
  n = 1
  ref = S_element
FEATURE [App::DocumentObjectGroupPython] O_element049  label="O_element : 6"  # scripted group (container) (typed FeaturePython)
  n = 6
  ref = O_element
FEATURE [App::DocumentObjectGroupPython] H_element045  label="H_element : 024"  # scripted group (container) (typed FeaturePython)
  n = 4
  ref = H_element
FEATURE [App::DocumentObjectGroupPython] G4_GYPSUM  # scripted group (container) (typed FeaturePython)
  Dunit = g/cm3
  Dvalue = 2.32
  Group = -> [Ca_element012,S_element014,O_element049,H_element045]
  conduct = 2
  density = 1
  expand = 3
  formula = G4_GYPSUM
  name = G4_GYPSUM
  specific = 4
FEATURE [App::DocumentObjectGroupPython] C_element052  label="C_element : 7"  # scripted group (container) (typed FeaturePython)
  n = 7
  ref = C_element
FEATURE [App::DocumentObjectGroupPython] H_element046  label="H_element : 16"  # scripted group (container) (typed FeaturePython)
  n = 16
  ref = H_element
FEATURE [App::DocumentObjectGroupPython] G4_N_HEPTANE  label="G4_N-HEPTANE"  # scripted group (container) (typed FeaturePython)
  Dunit = g/cm3
  Dvalue = 0.68376
  Group = -> [C_element052,H_element046]
  conduct = 2
  density = 1
  expand = 3
  formula = G4_N-HEPTANE
  name = G4_N-HEPTANE
  specific = 4
FEATURE [App::DocumentObjectGroupPython] C_element053  label="C_element : 029"  # scripted group (container) (typed FeaturePython)
  n = 6
  ref = C_element
FEATURE [App::DocumentObjectGroupPython] H_element047  label="H_element : 14"  # scripted group (container) (typed FeaturePython)
  n = 14
  ref = H_element
FEATURE [App::DocumentObjectGroupPython] G4_N_HEXANE  label="G4_N-HEXANE"  # scripted group (container) (typed FeaturePython)
  Dunit = g/cm3
  Dvalue = 0.6603
  Group = -> [C_element053,H_element047]
  conduct = 2
  density = 1
  expand = 3
  formula = G4_N-HEXANE
  name = G4_N-HEXANE
  specific = 4
FEATURE [App::DocumentObjectGroupPython] C_element054  label="C_element : 22"  # scripted group (container) (typed FeaturePython)
  n = 22
  ref = C_element
FEATURE [App::DocumentObjectGroupPython] H_element048  label="H_element : 025"  # scripted group (container) (typed FeaturePython)
  n = 10
  ref = H_element
FEATURE [App::DocumentObjectGroupPython] N_element021  label="N_element : 010"  # scripted group (container) (typed FeaturePython)
  n = 2
  ref = N_element
FEATURE [App::DocumentObjectGroupPython] O_element050  label="O_element : 025"  # scripted group (container) (typed FeaturePython)
  n = 5
  ref = O_element
FEATURE [App::DocumentObjectGroupPython] G4_KAPTON  # scripted group (container) (typed FeaturePython)
  Dunit = g/cm3
  Dvalue = 1.42
  Group = -> [C_element054,H_element048,N_element021,O_element050]
  conduct = 2
  density = 1
  expand = 3
  formula = G4_KAPTON
  name = G4_KAPTON
  specific = 4
FEATURE [App::DocumentObjectGroupPython] La_element001  label="La_element : 1"  # scripted group (container) (typed FeaturePython)
  n = 1
  ref = La_element
FEATURE [App::DocumentObjectGroupPython] Br_element003  label="Br_element : 002"  # scripted group (container) (typed FeaturePython)
  n = 1
  ref = Br_element
FEATURE [App::DocumentObjectGroupPython] O_element051  label="O_element : 026"  # scripted group (container) (typed FeaturePython)
  n = 1
  ref = O_element
FEATURE [App::DocumentObjectGroupPython] G4_LANTHANUM_OXYBROMIDE  # scripted group (container) (typed FeaturePython)
  Dunit = g/cm3
  Dvalue = 6.28
  Group = -> [La_element001,Br_element003,O_element051]
  conduct = 2
  density = 1
  expand = 3
  formula = G4_LANTHANUM_OXYBROMIDE
  name = G4_LANTHANUM_OXYBROMIDE
  specific = 4
FEATURE [App::DocumentObjectGroupPython] La_element002  label="La_element : 2"  # scripted group (container) (typed FeaturePython)
  n = 2
  ref = La_element
FEATURE [App::DocumentObjectGroupPython] O_element052  label="O_element : 027"  # scripted group (container) (typed FeaturePython)
  n = 2
  ref = O_element
FEATURE [App::DocumentObjectGroupPython] S_element015  label="S_element : 006"  # scripted group (container) (typed FeaturePython)
  n = 1
  ref = S_element
FEATURE [App::DocumentObjectGroupPython] G4_LANTHANUM_OXYSULFIDE  # scripted group (container) (typed FeaturePython)
  Dunit = g/cm3
  Dvalue = 5.86
  Group = -> [La_element002,O_element052,S_element015]
  conduct = 2
  density = 1
  expand = 3
  formula = G4_LANTHANUM_OXYSULFIDE
  name = G4_LANTHANUM_OXYSULFIDE
  specific = 4
FEATURE [App::DocumentObjectGroupPython] O_element053  label="O_element : 0.072"  # scripted group (container) (typed FeaturePython)
  n = 0.071682
FEATURE [App::DocumentObjectGroupPython] Pb_element002  label="Pb_element : 0.928"  # scripted group (container) (typed FeaturePython)
  n = 0.928318
FEATURE [App::DocumentObjectGroupPython] G4_LEAD_OXIDE  # scripted group (container) (typed FeaturePython)
  Dunit = g/cm3
  Dvalue = 9.53
  Group = -> [O_element053,Pb_element002]
  conduct = 2
  density = 1
  expand = 3
  formula = G4_LEAD_OXIDE
  name = G4_LEAD_OXIDE
  specific = 4
FEATURE [App::DocumentObjectGroupPython] Li_element001  label="Li_element : 1"  # scripted group (container) (typed FeaturePython)
  n = 1
  ref = Li_element
FEATURE [App::DocumentObjectGroupPython] N_element022  label="N_element : 011"  # scripted group (container) (typed FeaturePython)
  n = 1
  ref = N_element
FEATURE [App::DocumentObjectGroupPython] H_element049  label="H_element : 026"  # scripted group (container) (typed FeaturePython)
  n = 2
  ref = H_element
FEATURE [App::DocumentObjectGroupPython] G4_LITHIUM_AMIDE  # scripted group (container) (typed FeaturePython)
  Dunit = g/cm3
  Dvalue = 1.178
  Group = -> [Li_element001,N_element022,H_element049]
  conduct = 2
  density = 1
  expand = 3
  formula = G4_LITHIUM_AMIDE
  name = G4_LITHIUM_AMIDE
  specific = 4
FEATURE [App::DocumentObjectGroupPython] Li_element002  label="Li_element : 2"  # scripted group (container) (typed FeaturePython)
  n = 2
  ref = Li_element
FEATURE [App::DocumentObjectGroupPython] C_element055  label="C_element : 030"  # scripted group (container) (typed FeaturePython)
  n = 1
  ref = C_element
FEATURE [App::DocumentObjectGroupPython] O_element054  label="O_element : 028"  # scripted group (container) (typed FeaturePython)
  n = 3
  ref = O_element
FEATURE [App::DocumentObjectGroupPython] G4_LITHIUM_CARBONATE  # scripted group (container) (typed FeaturePython)
  Dunit = g/cm3
  Dvalue = 2.11
  Group = -> [Li_element002,C_element055,O_element054]
  conduct = 2
  density = 1
  expand = 3
  formula = G4_LITHIUM_CARBONATE
  name = G4_LITHIUM_CARBONATE
  specific = 4
FEATURE [App::DocumentObjectGroupPython] Li_element003  label="Li_element : 003"  # scripted group (container) (typed FeaturePython)
  n = 1
  ref = Li_element
FEATURE [App::DocumentObjectGroupPython] F_element012  label="F_element : 004"  # scripted group (container) (typed FeaturePython)
  n = 1
  ref = F_element
FEATURE [App::DocumentObjectGroupPython] G4_LITHIUM_FLUORIDE  # scripted group (container) (typed FeaturePython)
  Dunit = g/cm3
  Dvalue = 2.635
  Group = -> [Li_element003,F_element012]
  conduct = 2
  density = 1
  expand = 3
  formula = G4_LITHIUM_FLUORIDE
  name = G4_LITHIUM_FLUORIDE
  specific = 4
FEATURE [App::DocumentObjectGroupPython] Li_element004  label="Li_element : 004"  # scripted group (container) (typed FeaturePython)
  n = 1
  ref = Li_element
FEATURE [App::DocumentObjectGroupPython] H_element050  label="H_element : 027"  # scripted group (container) (typed FeaturePython)
  n = 1
  ref = H_element
FEATURE [App::DocumentObjectGroupPython] G4_LITHIUM_HYDRIDE  # scripted group (container) (typed FeaturePython)
  Dunit = g/cm3
  Dvalue = 0.82
  Group = -> [Li_element004,H_element050]
  conduct = 2
  density = 1
  expand = 3
  formula = G4_LITHIUM_HYDRIDE
  name = G4_LITHIUM_HYDRIDE
  specific = 4
FEATURE [App::DocumentObjectGroupPython] Li_element005  label="Li_element : 005"  # scripted group (container) (typed FeaturePython)
  n = 1
  ref = Li_element
FEATURE [App::DocumentObjectGroupPython] I_element003  label="I_element : 002"  # scripted group (container) (typed FeaturePython)
  n = 1
  ref = I_element
FEATURE [App::DocumentObjectGroupPython] G4_LITHIUM_IODIDE  # scripted group (container) (typed FeaturePython)
  Dunit = g/cm3
  Dvalue = 3.494
  Group = -> [Li_element005,I_element003]
  conduct = 2
  density = 1
  expand = 3
  formula = G4_LITHIUM_IODIDE
  name = G4_LITHIUM_IODIDE
  specific = 4
FEATURE [App::DocumentObjectGroupPython] Li_element006  label="Li_element : 006"  # scripted group (container) (typed FeaturePython)
  n = 2
  ref = Li_element
FEATURE [App::DocumentObjectGroupPython] O_element055  label="O_element : 029"  # scripted group (container) (typed FeaturePython)
  n = 1
  ref = O_element
FEATURE [App::DocumentObjectGroupPython] G4_LITHIUM_OXIDE  # scripted group (container) (typed FeaturePython)
  Dunit = g/cm3
  Dvalue = 2.013
  Group = -> [Li_element006,O_element055]
  conduct = 2
  density = 1
  expand = 3
  formula = G4_LITHIUM_OXIDE
  name = G4_LITHIUM_OXIDE
  specific = 4
FEATURE [App::DocumentObjectGroupPython] Li_element007  label="Li_element : 007"  # scripted group (container) (typed FeaturePython)
  n = 2
  ref = Li_element
FEATURE [App::DocumentObjectGroupPython] B_element005  label="B_element : 005"  # scripted group (container) (typed FeaturePython)
  n = 4
  ref = B_element
FEATURE [App::DocumentObjectGroupPython] O_element056  label="O_element : 7"  # scripted group (container) (typed FeaturePython)
  n = 7
  ref = O_element
FEATURE [App::DocumentObjectGroupPython] G4_LITHIUM_TETRABORATE  # scripted group (container) (typed FeaturePython)
  Dunit = g/cm3
  Dvalue = 2.44
  Group = -> [Li_element007,B_element005,O_element056]
  conduct = 2
  density = 1
  expand = 3
  formula = G4_LITHIUM_TETRABORATE
  name = G4_LITHIUM_TETRABORATE
  specific = 4
FEATURE [App::DocumentObjectGroupPython] H_element051  label="H_element : 0.105"  # scripted group (container) (typed FeaturePython)
  n = 0.105
FEATURE [App::DocumentObjectGroupPython] C_element056  label="C_element : 0.083"  # scripted group (container) (typed FeaturePython)
  n = 0.083
FEATURE [App::DocumentObjectGroupPython] N_element023  label="N_element : 0.023"  # scripted group (container) (typed FeaturePython)
  n = 0.023
FEATURE [App::DocumentObjectGroupPython] O_element057  label="O_element : 0.779"  # scripted group (container) (typed FeaturePython)
  n = 0.779
FEATURE [App::DocumentObjectGroupPython] Na_element010  label="Na_element : 0.097"  # scripted group (container) (typed FeaturePython)
  n = 0.002
FEATURE [App::DocumentObjectGroupPython] P_element006  label="P_element : 0.105"  # scripted group (container) (typed FeaturePython)
  n = 0.001
FEATURE [App::DocumentObjectGroupPython] S_element016  label="S_element : 0.017"  # scripted group (container) (typed FeaturePython)
  n = 0.002
FEATURE [App::DocumentObjectGroupPython] Cl_element014  label="Cl_element : 0.587"  # scripted group (container) (typed FeaturePython)
  n = 0.003
FEATURE [App::DocumentObjectGroupPython] K_element005  label="K_element : 0.015"  # scripted group (container) (typed FeaturePython)
  n = 0.002
FEATURE [App::DocumentObjectGroupPython] G4_LUNG_ICRP  # scripted group (container) (typed FeaturePython)
  Dunit = g/cm3
  Dvalue = 1.04
  Group = -> [H_element051,C_element056,N_element023,O_element057,Na_element010,P_element006,S_element016,Cl_element014,K_element005]
  conduct = 2
  density = 1
  expand = 3
  formula = G4_LUNG_ICRP
  name = G4_LUNG_ICRP
  specific = 4
FEATURE [App::DocumentObjectGroupPython] H_element052  label="H_element : 0.116"  # scripted group (container) (typed FeaturePython)
  n = 0.114318
FEATURE [App::DocumentObjectGroupPython] C_element057  label="C_element : 0.656"  # scripted group (container) (typed FeaturePython)
  n = 0.655824
FEATURE [App::DocumentObjectGroupPython] O_element058  label="O_element : 0.092"  # scripted group (container) (typed FeaturePython)
  n = 0.0921831
FEATURE [App::DocumentObjectGroupPython] Mg_element004  label="Mg_element : 0.135"  # scripted group (container) (typed FeaturePython)
  n = 0.134792
FEATURE [App::DocumentObjectGroupPython] Ca_element013  label="Ca_element : 0.003"  # scripted group (container) (typed FeaturePython)
  n = 0.002883
FEATURE [App::DocumentObjectGroupPython] G4_M3_WAX  # scripted group (container) (typed FeaturePython)
  Dunit = g/cm3
  Dvalue = 1.05
  Group = -> [H_element052,C_element057,O_element058,Mg_element004,Ca_element013]
  conduct = 2
  density = 1
  expand = 3
  formula = G4_M3_WAX
  name = G4_M3_WAX
  specific = 4
FEATURE [App::DocumentObjectGroupPython] Mg_element005  label="Mg_element : 1"  # scripted group (container) (typed FeaturePython)
  n = 1
  ref = Mg_element
FEATURE [App::DocumentObjectGroupPython] C_element058  label="C_element : 031"  # scripted group (container) (typed FeaturePython)
  n = 1
  ref = C_element
FEATURE [App::DocumentObjectGroupPython] O_element059  label="O_element : 030"  # scripted group (container) (typed FeaturePython)
  n = 3
  ref = O_element
FEATURE [App::DocumentObjectGroupPython] G4_MAGNESIUM_CARBONATE  # scripted group (container) (typed FeaturePython)
  Dunit = g/cm3
  Dvalue = 2.958
  Group = -> [Mg_element005,C_element058,O_element059]
  conduct = 2
  density = 1
  expand = 3
  formula = G4_MAGNESIUM_CARBONATE
  name = G4_MAGNESIUM_CARBONATE
  specific = 4
FEATURE [App::DocumentObjectGroupPython] Mg_element006  label="Mg_element : 002"  # scripted group (container) (typed FeaturePython)
  n = 1
  ref = Mg_element
FEATURE [App::DocumentObjectGroupPython] F_element013  label="F_element : 005"  # scripted group (container) (typed FeaturePython)
  n = 2
  ref = F_element
FEATURE [App::DocumentObjectGroupPython] G4_MAGNESIUM_FLUORIDE  # scripted group (container) (typed FeaturePython)
  Dunit = g/cm3
  Dvalue = 3
  Group = -> [Mg_element006,F_element013]
  conduct = 2
  density = 1
  expand = 3
  formula = G4_MAGNESIUM_FLUORIDE
  name = G4_MAGNESIUM_FLUORIDE
  specific = 4
FEATURE [App::DocumentObjectGroupPython] Mg_element007  label="Mg_element : 003"  # scripted group (container) (typed FeaturePython)
  n = 1
  ref = Mg_element
FEATURE [App::DocumentObjectGroupPython] O_element060  label="O_element : 031"  # scripted group (container) (typed FeaturePython)
  n = 1
  ref = O_element
FEATURE [App::DocumentObjectGroupPython] G4_MAGNESIUM_OXIDE  # scripted group (container) (typed FeaturePython)
  Dunit = g/cm3
  Dvalue = 3.58
  Group = -> [Mg_element007,O_element060]
  conduct = 2
  density = 1
  expand = 3
  formula = G4_MAGNESIUM_OXIDE
  name = G4_MAGNESIUM_OXIDE
  specific = 4
FEATURE [App::DocumentObjectGroupPython] Mg_element008  label="Mg_element : 004"  # scripted group (container) (typed FeaturePython)
  n = 1
  ref = Mg_element
FEATURE [App::DocumentObjectGroupPython] B_element006  label="B_element : 006"  # scripted group (container) (typed FeaturePython)
  n = 4
  ref = B_element
FEATURE [App::DocumentObjectGroupPython] O_element061  label="O_element : 032"  # scripted group (container) (typed FeaturePython)
  n = 7
  ref = O_element
FEATURE [App::DocumentObjectGroupPython] G4_MAGNESIUM_TETRABORATE  # scripted group (container) (typed FeaturePython)
  Dunit = g/cm3
  Dvalue = 2.53
  Group = -> [Mg_element008,B_element006,O_element061]
  conduct = 2
  density = 1
  expand = 3
  formula = G4_MAGNESIUM_TETRABORATE
  name = G4_MAGNESIUM_TETRABORATE
  specific = 4
FEATURE [App::DocumentObjectGroupPython] Hg_element001  label="Hg_element : 1"  # scripted group (container) (typed FeaturePython)
  n = 1
  ref = Hg_element
FEATURE [App::DocumentObjectGroupPython] I_element004  label="I_element : 2"  # scripted group (container) (typed FeaturePython)
  n = 2
  ref = I_element
FEATURE [App::DocumentObjectGroupPython] G4_MERCURIC_IODIDE  # scripted group (container) (typed FeaturePython)
  Dunit = g/cm3
  Dvalue = 6.36
  Group = -> [Hg_element001,I_element004]
  conduct = 2
  density = 1
  expand = 3
  formula = G4_MERCURIC_IODIDE
  name = G4_MERCURIC_IODIDE
  specific = 4
FEATURE [App::DocumentObjectGroupPython] C_element059  label="C_element : 032"  # scripted group (container) (typed FeaturePython)
  n = 1
  ref = C_element
FEATURE [App::DocumentObjectGroupPython] H_element053  label="H_element : 028"  # scripted group (container) (typed FeaturePython)
  n = 4
  ref = H_element
FEATURE [App::DocumentObjectGroupPython] G4_METHANE  # scripted group (container) (typed FeaturePython)
  Dunit = g/cm3
  Dvalue = 0.000667151
  Group = -> [C_element059,H_element053]
  conduct = 2
  density = 1
  expand = 3
  formula = G4_METHANE
  name = G4_METHANE
  specific = 4
FEATURE [App::DocumentObjectGroupPython] C_element060  label="C_element : 033"  # scripted group (container) (typed FeaturePython)
  n = 1
  ref = C_element
FEATURE [App::DocumentObjectGroupPython] H_element054  label="H_element : 029"  # scripted group (container) (typed FeaturePython)
  n = 4
  ref = H_element
FEATURE [App::DocumentObjectGroupPython] O_element062  label="O_element : 033"  # scripted group (container) (typed FeaturePython)
  n = 1
  ref = O_element
FEATURE [App::DocumentObjectGroupPython] G4_METHANOL  # scripted group (container) (typed FeaturePython)
  Dunit = g/cm3
  Dvalue = 0.7914
  Group = -> [C_element060,H_element054,O_element062]
  conduct = 2
  density = 1
  expand = 3
  formula = G4_METHANOL
  name = G4_METHANOL
  specific = 4
FEATURE [App::DocumentObjectGroupPython] H_element055  label="H_element : 0.134"  # scripted group (container) (typed FeaturePython)
  n = 0.13404
FEATURE [App::DocumentObjectGroupPython] C_element061  label="C_element : 0.778"  # scripted group (container) (typed FeaturePython)
  n = 0.77796
FEATURE [App::DocumentObjectGroupPython] O_element063  label="O_element : 0.035"  # scripted group (container) (typed FeaturePython)
  n = 0.03502
FEATURE [App::DocumentObjectGroupPython] Mg_element009  label="Mg_element : 0.039"  # scripted group (container) (typed FeaturePython)
  n = 0.038594
FEATURE [App::DocumentObjectGroupPython] Ti_element002  label="Ti_element : 0.014"  # scripted group (container) (typed FeaturePython)
  n = 0.014386
FEATURE [App::DocumentObjectGroupPython] G4_MIX_D_WAX  # scripted group (container) (typed FeaturePython)
  Dunit = g/cm3
  Dvalue = 0.99
  Group = -> [H_element055,C_element061,O_element063,Mg_element009,Ti_element002]
  conduct = 2
  density = 1
  expand = 3
  formula = G4_MIX_D_WAX
  name = G4_MIX_D_WAX
  specific = 4
FEATURE [App::DocumentObjectGroupPython] H_element056  label="H_element : 0.135"  # scripted group (container) (typed FeaturePython)
  n = 0.081192
FEATURE [App::DocumentObjectGroupPython] C_element062  label="C_element : 0.583"  # scripted group (container) (typed FeaturePython)
  n = 0.583442
FEATURE [App::DocumentObjectGroupPython] N_element024  label="N_element : 0.018"  # scripted group (container) (typed FeaturePython)
  n = 0.017798
FEATURE [App::DocumentObjectGroupPython] O_element064  label="O_element : 0.186"  # scripted group (container) (typed FeaturePython)
  n = 0.186381
FEATURE [App::DocumentObjectGroupPython] Mg_element010  label="Mg_element : 0.130"  # scripted group (container) (typed FeaturePython)
  n = 0.130287
FEATURE [App::DocumentObjectGroupPython] Cl_element015  label="Cl_element : 0.588"  # scripted group (container) (typed FeaturePython)
  n = 0.0009
FEATURE [App::DocumentObjectGroupPython] G4_MS20_TISSUE  # scripted group (container) (typed FeaturePython)
  Dunit = g/cm3
  Dvalue = 1
  Group = -> [H_element056,C_element062,N_element024,O_element064,Mg_element010,Cl_element015]
  conduct = 2
  density = 1
  expand = 3
  formula = G4_MS20_TISSUE
  name = G4_MS20_TISSUE
  specific = 4
FEATURE [App::DocumentObjectGroupPython] H_element057  label="H_element : 0.136"  # scripted group (container) (typed FeaturePython)
  n = 0.102
FEATURE [App::DocumentObjectGroupPython] C_element063  label="C_element : 0.143"  # scripted group (container) (typed FeaturePython)
  n = 0.143
FEATURE [App::DocumentObjectGroupPython] N_element025  label="N_element : 0.034"  # scripted group (container) (typed FeaturePython)
  n = 0.034
FEATURE [App::DocumentObjectGroupPython] O_element065  label="O_element : 0.710"  # scripted group (container) (typed FeaturePython)
  n = 0.71
FEATURE [App::DocumentObjectGroupPython] Na_element011  label="Na_element : 0.098"  # scripted group (container) (typed FeaturePython)
  n = 0.001
FEATURE [App::DocumentObjectGroupPython] P_element007  label="P_element : 0.002"  # scripted group (container) (typed FeaturePython)
  n = 0.002
FEATURE [App::DocumentObjectGroupPython] S_element017  label="S_element : 0.018"  # scripted group (container) (typed FeaturePython)
  n = 0.003
FEATURE [App::DocumentObjectGroupPython] Cl_element016  label="Cl_element : 0.589"  # scripted group (container) (typed FeaturePython)
  n = 0.001
FEATURE [App::DocumentObjectGroupPython] K_element006  label="K_element : 0.004"  # scripted group (container) (typed FeaturePython)
  n = 0.004
FEATURE [App::DocumentObjectGroupPython] G4_MUSCLE_SKELETAL_ICRP  # scripted group (container) (typed FeaturePython)
  Dunit = g/cm3
  Dvalue = 1.05
  Group = -> [H_element057,C_element063,N_element025,O_element065,Na_element011,P_element007,S_element017,Cl_element016,K_element006]
  conduct = 2
  density = 1
  expand = 3
  formula = G4_MUSCLE_SKELETAL_ICRP
  name = G4_MUSCLE_SKELETAL_ICRP
  specific = 4
FEATURE [App::DocumentObjectGroupPython] H_element058  label="H_element : 0.137"  # scripted group (container) (typed FeaturePython)
  n = 0.102102
FEATURE [App::DocumentObjectGroupPython] C_element064  label="C_element : 0.123"  # scripted group (container) (typed FeaturePython)
  n = 0.123123
FEATURE [App::DocumentObjectGroupPython] N_element026  label="N_element : 0.756"  # scripted group (container) (typed FeaturePython)
  n = 0.035035
FEATURE [App::DocumentObjectGroupPython] O_element066  label="O_element : 0.730"  # scripted group (container) (typed FeaturePython)
  n = 0.72973
FEATURE [App::DocumentObjectGroupPython] Na_element012  label="Na_element : 0.099"  # scripted group (container) (typed FeaturePython)
  n = 0.001001
FEATURE [App::DocumentObjectGroupPython] P_element008  label="P_element : 0.106"  # scripted group (container) (typed FeaturePython)
  n = 0.002002
FEATURE [App::DocumentObjectGroupPython] S_element018  label="S_element : 0.019"  # scripted group (container) (typed FeaturePython)
  n = 0.004004
FEATURE [App::DocumentObjectGroupPython] K_element007  label="K_element : 0.016"  # scripted group (container) (typed FeaturePython)
  n = 0.003003
FEATURE [App::DocumentObjectGroupPython] G4_MUSCLE_STRIATED_ICRU  # scripted group (container) (typed FeaturePython)
  Dunit = g/cm3
  Dvalue = 1.04
  Group = -> [H_element058,C_element064,N_element026,O_element066,Na_element012,P_element008,S_element018,K_element007]
  conduct = 2
  density = 1
  expand = 3
  formula = G4_MUSCLE_STRIATED_ICRU
  name = G4_MUSCLE_STRIATED_ICRU
  specific = 4
FEATURE [App::DocumentObjectGroupPython] H_element059  label="H_element : 0.098"  # scripted group (container) (typed FeaturePython)
  n = 0.0982341
FEATURE [App::DocumentObjectGroupPython] C_element065  label="C_element : 0.156"  # scripted group (container) (typed FeaturePython)
  n = 0.156214
FEATURE [App::DocumentObjectGroupPython] N_element027  label="N_element : 0.757"  # scripted group (container) (typed FeaturePython)
  n = 0.035451
FEATURE [App::DocumentObjectGroupPython] O_element067  label="O_element : 0.880"  # scripted group (container) (typed FeaturePython)
  n = 0.710101
FEATURE [App::DocumentObjectGroupPython] G4_MUSCLE_WITH_SUCROSE  # scripted group (container) (typed FeaturePython)
  Dunit = g/cm3
  Dvalue = 1.11
  Group = -> [H_element059,C_element065,N_element027,O_element067]
  conduct = 2
  density = 1
  expand = 3
  formula = G4_MUSCLE_WITH_SUCROSE
  name = G4_MUSCLE_WITH_SUCROSE
  specific = 4
FEATURE [App::DocumentObjectGroupPython] H_element060  label="H_element : 0.138"  # scripted group (container) (typed FeaturePython)
  n = 0.101969
FEATURE [App::DocumentObjectGroupPython] C_element066  label="C_element : 0.120"  # scripted group (container) (typed FeaturePython)
  n = 0.120058
FEATURE [App::DocumentObjectGroupPython] N_element028  label="N_element : 0.758"  # scripted group (container) (typed FeaturePython)
  n = 0.035451
FEATURE [App::DocumentObjectGroupPython] O_element068  label="O_element : 0.743"  # scripted group (container) (typed FeaturePython)
  n = 0.742522
FEATURE [App::DocumentObjectGroupPython] G4_MUSCLE_WITHOUT_SUCROSE  # scripted group (container) (typed FeaturePython)
  Dunit = g/cm3
  Dvalue = 1.07
  Group = -> [H_element060,C_element066,N_element028,O_element068]
  conduct = 2
  density = 1
  expand = 3
  formula = G4_MUSCLE_WITHOUT_SUCROSE
  name = G4_MUSCLE_WITHOUT_SUCROSE
  specific = 4
FEATURE [App::DocumentObjectGroupPython] C_element067  label="C_element : 10"  # scripted group (container) (typed FeaturePython)
  n = 10
  ref = C_element
FEATURE [App::DocumentObjectGroupPython] H_element061  label="H_element : 030"  # scripted group (container) (typed FeaturePython)
  n = 8
  ref = H_element
FEATURE [App::DocumentObjectGroupPython] G4_NAPHTHALENE  # scripted group (container) (typed FeaturePython)
  Dunit = g/cm3
  Dvalue = 1.145
  Group = -> [C_element067,H_element061]
  conduct = 2
  density = 1
  expand = 3
  formula = G4_NAPHTHALENE
  name = G4_NAPHTHALENE
  specific = 4
FEATURE [App::DocumentObjectGroupPython] C_element068  label="C_element : 034"  # scripted group (container) (typed FeaturePython)
  n = 6
  ref = C_element
FEATURE [App::DocumentObjectGroupPython] H_element062  label="H_element : 031"  # scripted group (container) (typed FeaturePython)
  n = 5
  ref = H_element
FEATURE [App::DocumentObjectGroupPython] N_element029  label="N_element : 012"  # scripted group (container) (typed FeaturePython)
  n = 1
  ref = N_element
FEATURE [App::DocumentObjectGroupPython] O_element069  label="O_element : 034"  # scripted group (container) (typed FeaturePython)
  n = 2
  ref = O_element
FEATURE [App::DocumentObjectGroupPython] G4_NITROBENZENE  # scripted group (container) (typed FeaturePython)
  Dunit = g/cm3
  Dvalue = 1.19867
  Group = -> [C_element068,H_element062,N_element029,O_element069]
  conduct = 2
  density = 1
  expand = 3
  formula = G4_NITROBENZENE
  name = G4_NITROBENZENE
  specific = 4
FEATURE [App::DocumentObjectGroupPython] N_element030  label="N_element : 013"  # scripted group (container) (typed FeaturePython)
  n = 2
  ref = N_element
FEATURE [App::DocumentObjectGroupPython] O_element070  label="O_element : 035"  # scripted group (container) (typed FeaturePython)
  n = 1
  ref = O_element
FEATURE [App::DocumentObjectGroupPython] G4_NITROUS_OXIDE  # scripted group (container) (typed FeaturePython)
  Dunit = g/cm3
  Dvalue = 0.00183094
  Group = -> [N_element030,O_element070]
  conduct = 2
  density = 1
  expand = 3
  formula = G4_NITROUS_OXIDE
  name = G4_NITROUS_OXIDE
  specific = 4
FEATURE [App::DocumentObjectGroupPython] H_element063  label="H_element : 0.104"  # scripted group (container) (typed FeaturePython)
  n = 0.103509
FEATURE [App::DocumentObjectGroupPython] C_element069  label="C_element : 0.648"  # scripted group (container) (typed FeaturePython)
  n = 0.648416
FEATURE [App::DocumentObjectGroupPython] N_element031  label="N_element : 0.100"  # scripted group (container) (typed FeaturePython)
  n = 0.0995361
FEATURE [App::DocumentObjectGroupPython] O_element071  label="O_element : 0.149"  # scripted group (container) (typed FeaturePython)
  n = 0.148539
FEATURE [App::DocumentObjectGroupPython] G4_NYLON_8062  label="G4_NYLON-8062"  # scripted group (container) (typed FeaturePython)
  Dunit = g/cm3
  Dvalue = 1.08
  Group = -> [H_element063,C_element069,N_element031,O_element071]
  conduct = 2
  density = 1
  expand = 3
  formula = G4_NYLON-8062
  name = G4_NYLON-8062
  specific = 4
FEATURE [App::DocumentObjectGroupPython] C_element070  label="C_element : 035"  # scripted group (container) (typed FeaturePython)
  n = 6
  ref = C_element
FEATURE [App::DocumentObjectGroupPython] H_element064  label="H_element : 11"  # scripted group (container) (typed FeaturePython)
  n = 11
  ref = H_element
FEATURE [App::DocumentObjectGroupPython] N_element032  label="N_element : 014"  # scripted group (container) (typed FeaturePython)
  n = 1
  ref = N_element
FEATURE [App::DocumentObjectGroupPython] O_element072  label="O_element : 036"  # scripted group (container) (typed FeaturePython)
  n = 1
  ref = O_element
FEATURE [App::DocumentObjectGroupPython] G4_NYLON_6_6  label="G4_NYLON-6-6"  # scripted group (container) (typed FeaturePython)
  Dunit = g/cm3
  Dvalue = 1.14
  Group = -> [C_element070,H_element064,N_element032,O_element072]
  conduct = 2
  density = 1
  expand = 3
  formula = G4_NYLON-6-6
  name = G4_NYLON-6-6
  specific = 4
FEATURE [App::DocumentObjectGroupPython] H_element065  label="H_element : 0.139"  # scripted group (container) (typed FeaturePython)
  n = 0.107062
FEATURE [App::DocumentObjectGroupPython] C_element071  label="C_element : 0.680"  # scripted group (container) (typed FeaturePython)
  n = 0.680449
FEATURE [App::DocumentObjectGroupPython] N_element033  label="N_element : 0.099"  # scripted group (container) (typed FeaturePython)
  n = 0.099189
FEATURE [App::DocumentObjectGroupPython] O_element073  label="O_element : 0.113"  # scripted group (container) (typed FeaturePython)
  n = 0.1133
FEATURE [App::DocumentObjectGroupPython] G4_NYLON_6_10  label="G4_NYLON-6-10"  # scripted group (container) (typed FeaturePython)
  Dunit = g/cm3
  Dvalue = 1.14
  Group = -> [H_element065,C_element071,N_element033,O_element073]
  conduct = 2
  density = 1
  expand = 3
  formula = G4_NYLON-6-10
  name = G4_NYLON-6-10
  specific = 4
FEATURE [App::DocumentObjectGroupPython] H_element066  label="H_element : 0.140"  # scripted group (container) (typed FeaturePython)
  n = 0.115476
FEATURE [App::DocumentObjectGroupPython] C_element072  label="C_element : 0.721"  # scripted group (container) (typed FeaturePython)
  n = 0.720818
FEATURE [App::DocumentObjectGroupPython] N_element034  label="N_element : 0.076"  # scripted group (container) (typed FeaturePython)
  n = 0.0764169
FEATURE [App::DocumentObjectGroupPython] O_element074  label="O_element : 0.087"  # scripted group (container) (typed FeaturePython)
  n = 0.0872889
FEATURE [App::DocumentObjectGroupPython] G4_NYLON_11_RILSAN  label="G4_NYLON-11_RILSAN"  # scripted group (container) (typed FeaturePython)
  Dunit = g/cm3
  Dvalue = 1.425
  Group = -> [H_element066,C_element072,N_element034,O_element074]
  conduct = 2
  density = 1
  expand = 3
  formula = G4_NYLON-11_RILSAN
  name = G4_NYLON-11_RILSAN
  specific = 4
FEATURE [App::DocumentObjectGroupPython] C_element073  label="C_element : 8"  # scripted group (container) (typed FeaturePython)
  n = 8
  ref = C_element
FEATURE [App::DocumentObjectGroupPython] H_element067  label="H_element : 18"  # scripted group (container) (typed FeaturePython)
  n = 18
  ref = H_element
FEATURE [App::DocumentObjectGroupPython] G4_OCTANE  # scripted group (container) (typed FeaturePython)
  Dunit = g/cm3
  Dvalue = 0.7026
  Group = -> [C_element073,H_element067]
  conduct = 2
  density = 1
  expand = 3
  formula = G4_OCTANE
  name = G4_OCTANE
  specific = 4
FEATURE [App::DocumentObjectGroupPython] C_element074  label="C_element : 25"  # scripted group (container) (typed FeaturePython)
  n = 25
  ref = C_element
FEATURE [App::DocumentObjectGroupPython] H_element068  label="H_element : 52"  # scripted group (container) (typed FeaturePython)
  n = 52
  ref = H_element
FEATURE [App::DocumentObjectGroupPython] G4_PARAFFIN  # scripted group (container) (typed FeaturePython)
  Dunit = g/cm3
  Dvalue = 0.93
  Group = -> [C_element074,H_element068]
  conduct = 2
  density = 1
  expand = 3
  formula = G4_PARAFFIN
  name = G4_PARAFFIN
  specific = 4
FEATURE [App::DocumentObjectGroupPython] C_element075  label="C_element : 036"  # scripted group (container) (typed FeaturePython)
  n = 5
  ref = C_element
FEATURE [App::DocumentObjectGroupPython] H_element069  label="H_element : 032"  # scripted group (container) (typed FeaturePython)
  n = 12
  ref = H_element
FEATURE [App::DocumentObjectGroupPython] G4_N_PENTANE  label="G4_N-PENTANE"  # scripted group (container) (typed FeaturePython)
  Dunit = g/cm3
  Dvalue = 0.6262
  Group = -> [C_element075,H_element069]
  conduct = 2
  density = 1
  expand = 3
  formula = G4_N-PENTANE
  name = G4_N-PENTANE
  specific = 4
FEATURE [App::DocumentObjectGroupPython] H_element070  label="H_element : 0.014"  # scripted group (container) (typed FeaturePython)
  n = 0.0141
FEATURE [App::DocumentObjectGroupPython] C_element076  label="C_element : 0.072"  # scripted group (container) (typed FeaturePython)
  n = 0.072261
FEATURE [App::DocumentObjectGroupPython] N_element035  label="N_element : 0.019"  # scripted group (container) (typed FeaturePython)
  n = 0.01932
FEATURE [App::DocumentObjectGroupPython] O_element075  label="O_element : 0.066"  # scripted group (container) (typed FeaturePython)
  n = 0.066101
FEATURE [App::DocumentObjectGroupPython] S_element019  label="S_element : 0.020"  # scripted group (container) (typed FeaturePython)
  n = 0.00189
FEATURE [App::DocumentObjectGroupPython] Br_element004  label="Br_element : 0.349"  # scripted group (container) (typed FeaturePython)
  n = 0.349103
FEATURE [App::DocumentObjectGroupPython] Ag_element001  label="Ag_element : 0.474"  # scripted group (container) (typed FeaturePython)
  n = 0.474105
FEATURE [App::DocumentObjectGroupPython] I_element005  label="I_element : 0.003"  # scripted group (container) (typed FeaturePython)
  n = 0.00312
FEATURE [App::DocumentObjectGroupPython] G4_PHOTO_EMULSION  # scripted group (container) (typed FeaturePython)
  Dunit = g/cm3
  Dvalue = 3.815
  Group = -> [H_element070,C_element076,N_element035,O_element075,S_element019,Br_element004,Ag_element001,I_element005]
  conduct = 2
  density = 1
  expand = 3
  formula = G4_PHOTO_EMULSION
  name = G4_PHOTO_EMULSION
  specific = 4
FEATURE [App::DocumentObjectGroupPython] C_element077  label="C_element : 9"  # scripted group (container) (typed FeaturePython)
  n = 9
  ref = C_element
FEATURE [App::DocumentObjectGroupPython] H_element071  label="H_element : 033"  # scripted group (container) (typed FeaturePython)
  n = 10
  ref = H_element
FEATURE [App::DocumentObjectGroupPython] G4_PLASTIC_SC_VINYLTOLUENE  # scripted group (container) (typed FeaturePython)
  Dunit = g/cm3
  Dvalue = 1.032
  Group = -> [C_element077,H_element071]
  conduct = 2
  density = 1
  expand = 3
  formula = G4_PLASTIC_SC_VINYLTOLUENE
  name = G4_PLASTIC_SC_VINYLTOLUENE
  specific = 4
FEATURE [App::DocumentObjectGroupPython] Pu_element001  label="Pu_element : 1"  # scripted group (container) (typed FeaturePython)
  n = 1
  ref = Pu_element
FEATURE [App::DocumentObjectGroupPython] O_element076  label="O_element : 037"  # scripted group (container) (typed FeaturePython)
  n = 2
  ref = O_element
FEATURE [App::DocumentObjectGroupPython] G4_PLUTONIUM_DIOXIDE  # scripted group (container) (typed FeaturePython)
  Dunit = g/cm3
  Dvalue = 11.46
  Group = -> [Pu_element001,O_element076]
  conduct = 2
  density = 1
  expand = 3
  formula = G4_PLUTONIUM_DIOXIDE
  name = G4_PLUTONIUM_DIOXIDE
  specific = 4
FEATURE [App::DocumentObjectGroupPython] C_element078  label="C_element : 037"  # scripted group (container) (typed FeaturePython)
  n = 3
  ref = C_element
FEATURE [App::DocumentObjectGroupPython] H_element072  label="H_element : 034"  # scripted group (container) (typed FeaturePython)
  n = 3
  ref = H_element
FEATURE [App::DocumentObjectGroupPython] N_element036  label="N_element : 015"  # scripted group (container) (typed FeaturePython)
  n = 1
  ref = N_element
FEATURE [App::DocumentObjectGroupPython] G4_POLYACRYLONITRILE  # scripted group (container) (typed FeaturePython)
  Dunit = g/cm3
  Dvalue = 1.17
  Group = -> [C_element078,H_element072,N_element036]
  conduct = 2
  density = 1
  expand = 3
  formula = G4_POLYACRYLONITRILE
  name = G4_POLYACRYLONITRILE
  specific = 4
FEATURE [App::DocumentObjectGroupPython] C_element079  label="C_element : 16"  # scripted group (container) (typed FeaturePython)
  n = 16
  ref = C_element
FEATURE [App::DocumentObjectGroupPython] H_element073  label="H_element : 035"  # scripted group (container) (typed FeaturePython)
  n = 14
  ref = H_element
FEATURE [App::DocumentObjectGroupPython] O_element077  label="O_element : 038"  # scripted group (container) (typed FeaturePython)
  n = 3
  ref = O_element
FEATURE [App::DocumentObjectGroupPython] G4_POLYCARBONATE  # scripted group (container) (typed FeaturePython)
  Dunit = g/cm3
  Dvalue = 1.2
  Group = -> [C_element079,H_element073,O_element077]
  conduct = 2
  density = 1
  expand = 3
  formula = G4_POLYCARBONATE
  name = G4_POLYCARBONATE
  specific = 4
FEATURE [App::DocumentObjectGroupPython] C_element080  label="C_element : 038"  # scripted group (container) (typed FeaturePython)
  n = 8
  ref = C_element
FEATURE [App::DocumentObjectGroupPython] H_element074  label="H_element : 036"  # scripted group (container) (typed FeaturePython)
  n = 7
  ref = H_element
FEATURE [App::DocumentObjectGroupPython] Cl_element017  label="Cl_element : 007"  # scripted group (container) (typed FeaturePython)
  n = 1
  ref = Cl_element
FEATURE [App::DocumentObjectGroupPython] G4_POLYCHLOROSTYRENE  # scripted group (container) (typed FeaturePython)
  Dunit = g/cm3
  Dvalue = 1.3
  Group = -> [C_element080,H_element074,Cl_element017]
  conduct = 2
  density = 1
  expand = 3
  formula = G4_POLYCHLOROSTYRENE
  name = G4_POLYCHLOROSTYRENE
  specific = 4
FEATURE [App::DocumentObjectGroupPython] C_element081  label="C_element : 039"  # scripted group (container) (typed FeaturePython)
  n = 1
  ref = C_element
FEATURE [App::DocumentObjectGroupPython] H_element075  label="H_element : 037"  # scripted group (container) (typed FeaturePython)
  n = 2
  ref = H_element
FEATURE [App::DocumentObjectGroupPython] G4_POLYETHYLENE  # scripted group (container) (typed FeaturePython)
  Dunit = g/cm3
  Dvalue = 0.94
  Group = -> [C_element081,H_element075]
  conduct = 2
  density = 1
  expand = 3
  formula = G4_POLYETHYLENE
  name = G4_POLYETHYLENE
  specific = 4
FEATURE [App::DocumentObjectGroupPython] C_element082  label="C_element : 040"  # scripted group (container) (typed FeaturePython)
  n = 10
  ref = C_element
FEATURE [App::DocumentObjectGroupPython] H_element076  label="H_element : 038"  # scripted group (container) (typed FeaturePython)
  n = 8
  ref = H_element
FEATURE [App::DocumentObjectGroupPython] O_element078  label="O_element : 039"  # scripted group (container) (typed FeaturePython)
  n = 4
  ref = O_element
FEATURE [App::DocumentObjectGroupPython] G4_MYLAR  # scripted group (container) (typed FeaturePython)
  Dunit = g/cm3
  Dvalue = 1.4
  Group = -> [C_element082,H_element076,O_element078]
  conduct = 2
  density = 1
  expand = 3
  formula = G4_MYLAR
  name = G4_MYLAR
  specific = 4
FEATURE [App::DocumentObjectGroupPython] C_element083  label="C_element : 041"  # scripted group (container) (typed FeaturePython)
  n = 5
  ref = C_element
FEATURE [App::DocumentObjectGroupPython] H_element077  label="H_element : 039"  # scripted group (container) (typed FeaturePython)
  n = 8
  ref = H_element
FEATURE [App::DocumentObjectGroupPython] O_element079  label="O_element : 040"  # scripted group (container) (typed FeaturePython)
  n = 2
  ref = O_element
FEATURE [App::DocumentObjectGroupPython] G4_PLEXIGLASS  # scripted group (container) (typed FeaturePython)
  Dunit = g/cm3
  Dvalue = 1.19
  Group = -> [C_element083,H_element077,O_element079]
  conduct = 2
  density = 1
  expand = 3
  formula = G4_PLEXIGLASS
  name = G4_PLEXIGLASS
  specific = 4
FEATURE [App::DocumentObjectGroupPython] C_element084  label="C_element : 042"  # scripted group (container) (typed FeaturePython)
  n = 1
  ref = C_element
FEATURE [App::DocumentObjectGroupPython] H_element078  label="H_element : 040"  # scripted group (container) (typed FeaturePython)
  n = 2
  ref = H_element
FEATURE [App::DocumentObjectGroupPython] O_element080  label="O_element : 041"  # scripted group (container) (typed FeaturePython)
  n = 1
  ref = O_element
FEATURE [App::DocumentObjectGroupPython] G4_POLYOXYMETHYLENE  # scripted group (container) (typed FeaturePython)
  Dunit = g/cm3
  Dvalue = 1.425
  Group = -> [C_element084,H_element078,O_element080]
  conduct = 2
  density = 1
  expand = 3
  formula = G4_POLYOXYMETHYLENE
  name = G4_POLYOXYMETHYLENE
  specific = 4
FEATURE [App::DocumentObjectGroupPython] C_element085  label="C_element : 043"  # scripted group (container) (typed FeaturePython)
  n = 2
  ref = C_element
FEATURE [App::DocumentObjectGroupPython] H_element079  label="H_element : 041"  # scripted group (container) (typed FeaturePython)
  n = 4
  ref = H_element
FEATURE [App::DocumentObjectGroupPython] G4_POLYPROPYLENE  # scripted group (container) (typed FeaturePython)
  Dunit = g/cm3
  Dvalue = 0.9
  Group = -> [C_element085,H_element079]
  conduct = 2
  density = 1
  expand = 3
  formula = G4_POLYPROPYLENE
  name = G4_POLYPROPYLENE
  specific = 4
FEATURE [App::DocumentObjectGroupPython] C_element086  label="C_element : 044"  # scripted group (container) (typed FeaturePython)
  n = 8
  ref = C_element
FEATURE [App::DocumentObjectGroupPython] H_element080  label="H_element : 042"  # scripted group (container) (typed FeaturePython)
  n = 8
  ref = H_element
FEATURE [App::DocumentObjectGroupPython] G4_POLYSTYRENE  # scripted group (container) (typed FeaturePython)
  Dunit = g/cm3
  Dvalue = 1.06
  Group = -> [C_element086,H_element080]
  conduct = 2
  density = 1
  expand = 3
  formula = G4_POLYSTYRENE
  name = G4_POLYSTYRENE
  specific = 4
FEATURE [App::DocumentObjectGroupPython] C_element087  label="C_element : 045"  # scripted group (container) (typed FeaturePython)
  n = 2
  ref = C_element
FEATURE [App::DocumentObjectGroupPython] F_element014  label="F_element : 4"  # scripted group (container) (typed FeaturePython)
  n = 4
  ref = F_element
FEATURE [App::DocumentObjectGroupPython] G4_TEFLON  # scripted group (container) (typed FeaturePython)
  Dunit = g/cm3
  Dvalue = 2.2
  Group = -> [C_element087,F_element014]
  conduct = 2
  density = 1
  expand = 3
  formula = G4_TEFLON
  name = G4_TEFLON
  specific = 4
FEATURE [App::DocumentObjectGroupPython] C_element088  label="C_element : 046"  # scripted group (container) (typed FeaturePython)
  n = 2
  ref = C_element
FEATURE [App::DocumentObjectGroupPython] F_element015  label="F_element : 006"  # scripted group (container) (typed FeaturePython)
  n = 3
  ref = F_element
FEATURE [App::DocumentObjectGroupPython] Cl_element018  label="Cl_element : 008"  # scripted group (container) (typed FeaturePython)
  n = 1
  ref = Cl_element
FEATURE [App::DocumentObjectGroupPython] G4_POLYTRIFLUOROCHLOROETHYLENE  # scripted group (container) (typed FeaturePython)
  Dunit = g/cm3
  Dvalue = 2.1
  Group = -> [C_element088,F_element015,Cl_element018]
  conduct = 2
  density = 1
  expand = 3
  formula = G4_POLYTRIFLUOROCHLOROETHYLENE
  name = G4_POLYTRIFLUOROCHLOROETHYLENE
  specific = 4
FEATURE [App::DocumentObjectGroupPython] C_element089  label="C_element : 047"  # scripted group (container) (typed FeaturePython)
  n = 4
  ref = C_element
FEATURE [App::DocumentObjectGroupPython] H_element081  label="H_element : 043"  # scripted group (container) (typed FeaturePython)
  n = 6
  ref = H_element
FEATURE [App::DocumentObjectGroupPython] O_element081  label="O_element : 042"  # scripted group (container) (typed FeaturePython)
  n = 2
  ref = O_element
FEATURE [App::DocumentObjectGroupPython] G4_POLYVINYL_ACETATE  # scripted group (container) (typed FeaturePython)
  Dunit = g/cm3
  Dvalue = 1.19
  Group = -> [C_element089,H_element081,O_element081]
  conduct = 2
  density = 1
  expand = 3
  formula = G4_POLYVINYL_ACETATE
  name = G4_POLYVINYL_ACETATE
  specific = 4
FEATURE [App::DocumentObjectGroupPython] C_element090  label="C_element : 048"  # scripted group (container) (typed FeaturePython)
  n = 2
  ref = C_element
FEATURE [App::DocumentObjectGroupPython] H_element082  label="H_element : 044"  # scripted group (container) (typed FeaturePython)
  n = 4
  ref = H_element
FEATURE [App::DocumentObjectGroupPython] O_element082  label="O_element : 043"  # scripted group (container) (typed FeaturePython)
  n = 1
  ref = O_element
FEATURE [App::DocumentObjectGroupPython] G4_POLYVINYL_ALCOHOL  # scripted group (container) (typed FeaturePython)
  Dunit = g/cm3
  Dvalue = 1.3
  Group = -> [C_element090,H_element082,O_element082]
  conduct = 2
  density = 1
  expand = 3
  formula = G4_POLYVINYL_ALCOHOL
  name = G4_POLYVINYL_ALCOHOL
  specific = 4
FEATURE [App::DocumentObjectGroupPython] C_element091  label="C_element : 049"  # scripted group (container) (typed FeaturePython)
  n = 8
  ref = C_element
FEATURE [App::DocumentObjectGroupPython] H_element083  label="H_element : 045"  # scripted group (container) (typed FeaturePython)
  n = 14
  ref = H_element
FEATURE [App::DocumentObjectGroupPython] O_element083  label="O_element : 044"  # scripted group (container) (typed FeaturePython)
  n = 2
  ref = O_element
FEATURE [App::DocumentObjectGroupPython] G4_POLYVINYL_BUTYRAL  # scripted group (container) (typed FeaturePython)
  Dunit = g/cm3
  Dvalue = 1.12
  Group = -> [C_element091,H_element083,O_element083]
  conduct = 2
  density = 1
  expand = 3
  formula = G4_POLYVINYL_BUTYRAL
  name = G4_POLYVINYL_BUTYRAL
  specific = 4
FEATURE [App::DocumentObjectGroupPython] C_element092  label="C_element : 050"  # scripted group (container) (typed FeaturePython)
  n = 2
  ref = C_element
FEATURE [App::DocumentObjectGroupPython] H_element084  label="H_element : 046"  # scripted group (container) (typed FeaturePython)
  n = 3
  ref = H_element
FEATURE [App::DocumentObjectGroupPython] Cl_element019  label="Cl_element : 009"  # scripted group (container) (typed FeaturePython)
  n = 1
  ref = Cl_element
FEATURE [App::DocumentObjectGroupPython] G4_POLYVINYL_CHLORIDE  # scripted group (container) (typed FeaturePython)
  Dunit = g/cm3
  Dvalue = 1.3
  Group = -> [C_element092,H_element084,Cl_element019]
  conduct = 2
  density = 1
  expand = 3
  formula = G4_POLYVINYL_CHLORIDE
  name = G4_POLYVINYL_CHLORIDE
  specific = 4
FEATURE [App::DocumentObjectGroupPython] C_element093  label="C_element : 051"  # scripted group (container) (typed FeaturePython)
  n = 2
  ref = C_element
FEATURE [App::DocumentObjectGroupPython] H_element085  label="H_element : 047"  # scripted group (container) (typed FeaturePython)
  n = 2
  ref = H_element
FEATURE [App::DocumentObjectGroupPython] Cl_element020  label="Cl_element : 010"  # scripted group (container) (typed FeaturePython)
  n = 2
  ref = Cl_element
FEATURE [App::DocumentObjectGroupPython] G4_POLYVINYLIDENE_CHLORIDE  # scripted group (container) (typed FeaturePython)
  Dunit = g/cm3
  Dvalue = 1.7
  Group = -> [C_element093,H_element085,Cl_element020]
  conduct = 2
  density = 1
  expand = 3
  formula = G4_POLYVINYLIDENE_CHLORIDE
  name = G4_POLYVINYLIDENE_CHLORIDE
  specific = 4
FEATURE [App::DocumentObjectGroupPython] C_element094  label="C_element : 052"  # scripted group (container) (typed FeaturePython)
  n = 2
  ref = C_element
FEATURE [App::DocumentObjectGroupPython] H_element086  label="H_element : 048"  # scripted group (container) (typed FeaturePython)
  n = 2
  ref = H_element
FEATURE [App::DocumentObjectGroupPython] F_element016  label="F_element : 007"  # scripted group (container) (typed FeaturePython)
  n = 2
  ref = F_element
FEATURE [App::DocumentObjectGroupPython] G4_POLYVINYLIDENE_FLUORIDE  # scripted group (container) (typed FeaturePython)
  Dunit = g/cm3
  Dvalue = 1.76
  Group = -> [C_element094,H_element086,F_element016]
  conduct = 2
  density = 1
  expand = 3
  formula = G4_POLYVINYLIDENE_FLUORIDE
  name = G4_POLYVINYLIDENE_FLUORIDE
  specific = 4
FEATURE [App::DocumentObjectGroupPython] C_element095  label="C_element : 053"  # scripted group (container) (typed FeaturePython)
  n = 6
  ref = C_element
FEATURE [App::DocumentObjectGroupPython] H_element087  label="H_element : 9"  # scripted group (container) (typed FeaturePython)
  n = 9
  ref = H_element
FEATURE [App::DocumentObjectGroupPython] N_element037  label="N_element : 016"  # scripted group (container) (typed FeaturePython)
  n = 1
  ref = N_element
FEATURE [App::DocumentObjectGroupPython] O_element084  label="O_element : 045"  # scripted group (container) (typed FeaturePython)
  n = 1
  ref = O_element
FEATURE [App::DocumentObjectGroupPython] G4_POLYVINYL_PYRROLIDONE  # scripted group (container) (typed FeaturePython)
  Dunit = g/cm3
  Dvalue = 1.25
  Group = -> [C_element095,H_element087,N_element037,O_element084]
  conduct = 2
  density = 1
  expand = 3
  formula = G4_POLYVINYL_PYRROLIDONE
  name = G4_POLYVINYL_PYRROLIDONE
  specific = 4
FEATURE [App::DocumentObjectGroupPython] K_element008  label="K_element : 1"  # scripted group (container) (typed FeaturePython)
  n = 1
  ref = K_element
FEATURE [App::DocumentObjectGroupPython] I_element006  label="I_element : 003"  # scripted group (container) (typed FeaturePython)
  n = 1
  ref = I_element
FEATURE [App::DocumentObjectGroupPython] G4_POTASSIUM_IODIDE  # scripted group (container) (typed FeaturePython)
  Dunit = g/cm3
  Dvalue = 3.13
  Group = -> [K_element008,I_element006]
  conduct = 2
  density = 1
  expand = 3
  formula = G4_POTASSIUM_IODIDE
  name = G4_POTASSIUM_IODIDE
  specific = 4
FEATURE [App::DocumentObjectGroupPython] K_element009  label="K_element : 2"  # scripted group (container) (typed FeaturePython)
  n = 2
  ref = K_element
FEATURE [App::DocumentObjectGroupPython] O_element085  label="O_element : 046"  # scripted group (container) (typed FeaturePython)
  n = 1
  ref = O_element
FEATURE [App::DocumentObjectGroupPython] G4_POTASSIUM_OXIDE  # scripted group (container) (typed FeaturePython)
  Dunit = g/cm3
  Dvalue = 2.32
  Group = -> [K_element009,O_element085]
  conduct = 2
  density = 1
  expand = 3
  formula = G4_POTASSIUM_OXIDE
  name = G4_POTASSIUM_OXIDE
  specific = 4
FEATURE [App::DocumentObjectGroupPython] C_element096  label="C_element : 054"  # scripted group (container) (typed FeaturePython)
  n = 3
  ref = C_element
FEATURE [App::DocumentObjectGroupPython] H_element088  label="H_element : 049"  # scripted group (container) (typed FeaturePython)
  n = 8
  ref = H_element
FEATURE [App::DocumentObjectGroupPython] G4_PROPANE  # scripted group (container) (typed FeaturePython)
  Dunit = g/cm3
  Dvalue = 0.00187939
  Group = -> [C_element096,H_element088]
  conduct = 2
  density = 1
  expand = 3
  formula = G4_PROPANE
  name = G4_PROPANE
  specific = 4
FEATURE [App::DocumentObjectGroupPython] C_element097  label="C_element : 055"  # scripted group (container) (typed FeaturePython)
  n = 3
  ref = C_element
FEATURE [App::DocumentObjectGroupPython] H_element089  label="H_element : 050"  # scripted group (container) (typed FeaturePython)
  n = 8
  ref = H_element
FEATURE [App::DocumentObjectGroupPython] G4_lPROPANE  # scripted group (container) (typed FeaturePython)
  Dunit = g/cm3
  Dvalue = 0.43
  Group = -> [C_element097,H_element089]
  conduct = 2
  density = 1
  expand = 3
  formula = G4_lPROPANE
  name = G4_lPROPANE
  specific = 4
FEATURE [App::DocumentObjectGroupPython] C_element098  label="C_element : 056"  # scripted group (container) (typed FeaturePython)
  n = 3
  ref = C_element
FEATURE [App::DocumentObjectGroupPython] H_element090  label="H_element : 051"  # scripted group (container) (typed FeaturePython)
  n = 8
  ref = H_element
FEATURE [App::DocumentObjectGroupPython] O_element086  label="O_element : 047"  # scripted group (container) (typed FeaturePython)
  n = 1
  ref = O_element
FEATURE [App::DocumentObjectGroupPython] G4_N_PROPYL_ALCOHOL  label="G4_N-PROPYL_ALCOHOL"  # scripted group (container) (typed FeaturePython)
  Dunit = g/cm3
  Dvalue = 0.8035
  Group = -> [C_element098,H_element090,O_element086]
  conduct = 2
  density = 1
  expand = 3
  formula = G4_N-PROPYL_ALCOHOL
  name = G4_N-PROPYL_ALCOHOL
  specific = 4
FEATURE [App::DocumentObjectGroupPython] C_element099  label="C_element : 057"  # scripted group (container) (typed FeaturePython)
  n = 5
  ref = C_element
FEATURE [App::DocumentObjectGroupPython] H_element091  label="H_element : 052"  # scripted group (container) (typed FeaturePython)
  n = 5
  ref = H_element
FEATURE [App::DocumentObjectGroupPython] N_element038  label="N_element : 017"  # scripted group (container) (typed FeaturePython)
  n = 1
  ref = N_element
FEATURE [App::DocumentObjectGroupPython] G4_PYRIDINE  # scripted group (container) (typed FeaturePython)
  Dunit = g/cm3
  Dvalue = 0.9819
  Group = -> [C_element099,H_element091,N_element038]
  conduct = 2
  density = 1
  expand = 3
  formula = G4_PYRIDINE
  name = G4_PYRIDINE
  specific = 4
FEATURE [App::DocumentObjectGroupPython] H_element092  label="H_element : 0.144"  # scripted group (container) (typed FeaturePython)
  n = 0.143711
FEATURE [App::DocumentObjectGroupPython] C_element100  label="C_element : 0.856"  # scripted group (container) (typed FeaturePython)
  n = 0.856289
FEATURE [App::DocumentObjectGroupPython] G4_RUBBER_BUTYL  # scripted group (container) (typed FeaturePython)
  Dunit = g/cm3
  Dvalue = 0.92
  Group = -> [H_element092,C_element100]
  conduct = 2
  density = 1
  expand = 3
  formula = G4_RUBBER_BUTYL
  name = G4_RUBBER_BUTYL
  specific = 4
FEATURE [App::DocumentObjectGroupPython] H_element093  label="H_element : 0.118"  # scripted group (container) (typed FeaturePython)
  n = 0.118371
FEATURE [App::DocumentObjectGroupPython] C_element101  label="C_element : 0.882"  # scripted group (container) (typed FeaturePython)
  n = 0.881629
FEATURE [App::DocumentObjectGroupPython] G4_RUBBER_NATURAL  # scripted group (container) (typed FeaturePython)
  Dunit = g/cm3
  Dvalue = 0.92
  Group = -> [H_element093,C_element101]
  conduct = 2
  density = 1
  expand = 3
  formula = G4_RUBBER_NATURAL
  name = G4_RUBBER_NATURAL
  specific = 4
FEATURE [App::DocumentObjectGroupPython] H_element094  label="H_element : 0.145"  # scripted group (container) (typed FeaturePython)
  n = 0.05692
FEATURE [App::DocumentObjectGroupPython] C_element102  label="C_element : 0.543"  # scripted group (container) (typed FeaturePython)
  n = 0.542646
FEATURE [App::DocumentObjectGroupPython] Cl_element021  label="Cl_element : 0.400"  # scripted group (container) (typed FeaturePython)
  n = 0.400434
FEATURE [App::DocumentObjectGroupPython] G4_RUBBER_NEOPRENE  # scripted group (container) (typed FeaturePython)
  Dunit = g/cm3
  Dvalue = 1.23
  Group = -> [H_element094,C_element102,Cl_element021]
  conduct = 2
  density = 1
  expand = 3
  formula = G4_RUBBER_NEOPRENE
  name = G4_RUBBER_NEOPRENE
  specific = 4
FEATURE [App::DocumentObjectGroupPython] Si_element006  label="Si_element : 1"  # scripted group (container) (typed FeaturePython)
  n = 1
  ref = Si_element
FEATURE [App::DocumentObjectGroupPython] O_element087  label="O_element : 048"  # scripted group (container) (typed FeaturePython)
  n = 2
  ref = O_element
FEATURE [App::DocumentObjectGroupPython] G4_SILICON_DIOXIDE  # scripted group (container) (typed FeaturePython)
  Dunit = g/cm3
  Dvalue = 2.32
  Group = -> [Si_element006,O_element087]
  conduct = 2
  density = 1
  expand = 3
  formula = G4_SILICON_DIOXIDE
  name = G4_SILICON_DIOXIDE
  specific = 4
FEATURE [App::DocumentObjectGroupPython] Ag_element002  label="Ag_element : 1"  # scripted group (container) (typed FeaturePython)
  n = 1
  ref = Ag_element
FEATURE [App::DocumentObjectGroupPython] Br_element005  label="Br_element : 003"  # scripted group (container) (typed FeaturePython)
  n = 1
  ref = Br_element
FEATURE [App::DocumentObjectGroupPython] G4_SILVER_BROMIDE  # scripted group (container) (typed FeaturePython)
  Dunit = g/cm3
  Dvalue = 6.473
  Group = -> [Ag_element002,Br_element005]
  conduct = 2
  density = 1
  expand = 3
  formula = G4_SILVER_BROMIDE
  name = G4_SILVER_BROMIDE
  specific = 4
FEATURE [App::DocumentObjectGroupPython] Ag_element003  label="Ag_element : 002"  # scripted group (container) (typed FeaturePython)
  n = 1
  ref = Ag_element
FEATURE [App::DocumentObjectGroupPython] Cl_element022  label="Cl_element : 011"  # scripted group (container) (typed FeaturePython)
  n = 1
  ref = Cl_element
FEATURE [App::DocumentObjectGroupPython] G4_SILVER_CHLORIDE  # scripted group (container) (typed FeaturePython)
  Dunit = g/cm3
  Dvalue = 5.56
  Group = -> [Ag_element003,Cl_element022]
  conduct = 2
  density = 1
  expand = 3
  formula = G4_SILVER_CHLORIDE
  name = G4_SILVER_CHLORIDE
  specific = 4
FEATURE [App::DocumentObjectGroupPython] Br_element006  label="Br_element : 0.423"  # scripted group (container) (typed FeaturePython)
  n = 0.422895
FEATURE [App::DocumentObjectGroupPython] Ag_element004  label="Ag_element : 0.574"  # scripted group (container) (typed FeaturePython)
  n = 0.573748
FEATURE [App::DocumentObjectGroupPython] I_element007  label="I_element : 0.649"  # scripted group (container) (typed FeaturePython)
  n = 0.003357
FEATURE [App::DocumentObjectGroupPython] G4_SILVER_HALIDES  # scripted group (container) (typed FeaturePython)
  Dunit = g/cm3
  Dvalue = 6.47
  Group = -> [Br_element006,Ag_element004,I_element007]
  conduct = 2
  density = 1
  expand = 3
  formula = G4_SILVER_HALIDES
  name = G4_SILVER_HALIDES
  specific = 4
FEATURE [App::DocumentObjectGroupPython] Ag_element005  label="Ag_element : 003"  # scripted group (container) (typed FeaturePython)
  n = 1
  ref = Ag_element
FEATURE [App::DocumentObjectGroupPython] I_element008  label="I_element : 004"  # scripted group (container) (typed FeaturePython)
  n = 1
  ref = I_element
FEATURE [App::DocumentObjectGroupPython] G4_SILVER_IODIDE  # scripted group (container) (typed FeaturePython)
  Dunit = g/cm3
  Dvalue = 6.01
  Group = -> [Ag_element005,I_element008]
  conduct = 2
  density = 1
  expand = 3
  formula = G4_SILVER_IODIDE
  name = G4_SILVER_IODIDE
  specific = 4
FEATURE [App::DocumentObjectGroupPython] H_element095  label="H_element : 0.100"  # scripted group (container) (typed FeaturePython)
  n = 0.1
FEATURE [App::DocumentObjectGroupPython] C_element103  label="C_element : 0.204"  # scripted group (container) (typed FeaturePython)
  n = 0.204
FEATURE [App::DocumentObjectGroupPython] N_element039  label="N_element : 0.759"  # scripted group (container) (typed FeaturePython)
  n = 0.042
FEATURE [App::DocumentObjectGroupPython] O_element088  label="O_element : 0.645"  # scripted group (container) (typed FeaturePython)
  n = 0.645
FEATURE [App::DocumentObjectGroupPython] Na_element013  label="Na_element : 0.100"  # scripted group (container) (typed FeaturePython)
  n = 0.002
FEATURE [App::DocumentObjectGroupPython] P_element009  label="P_element : 0.107"  # scripted group (container) (typed FeaturePython)
  n = 0.001
FEATURE [App::DocumentObjectGroupPython] S_element020  label="S_element : 0.021"  # scripted group (container) (typed FeaturePython)
  n = 0.002
FEATURE [App::DocumentObjectGroupPython] Cl_element023  label="Cl_element : 0.590"  # scripted group (container) (typed FeaturePython)
  n = 0.003
FEATURE [App::DocumentObjectGroupPython] K_element010  label="K_element : 0.001"  # scripted group (container) (typed FeaturePython)
  n = 0.001
FEATURE [App::DocumentObjectGroupPython] G4_SKIN_ICRP  # scripted group (container) (typed FeaturePython)
  Dunit = g/cm3
  Dvalue = 1.09
  Group = -> [H_element095,C_element103,N_element039,O_element088,Na_element013,P_element009,S_element020,Cl_element023,K_element010]
  conduct = 2
  density = 1
  expand = 3
  formula = G4_SKIN_ICRP
  name = G4_SKIN_ICRP
  specific = 4
FEATURE [App::DocumentObjectGroupPython] Na_element014  label="Na_element : 2"  # scripted group (container) (typed FeaturePython)
  n = 2
  ref = Na_element
FEATURE [App::DocumentObjectGroupPython] C_element104  label="C_element : 058"  # scripted group (container) (typed FeaturePython)
  n = 1
  ref = C_element
FEATURE [App::DocumentObjectGroupPython] O_element089  label="O_element : 049"  # scripted group (container) (typed FeaturePython)
  n = 3
  ref = O_element
FEATURE [App::DocumentObjectGroupPython] G4_SODIUM_CARBONATE  # scripted group (container) (typed FeaturePython)
  Dunit = g/cm3
  Dvalue = 2.532
  Group = -> [Na_element014,C_element104,O_element089]
  conduct = 2
  density = 1
  expand = 3
  formula = G4_SODIUM_CARBONATE
  name = G4_SODIUM_CARBONATE
  specific = 4
FEATURE [App::DocumentObjectGroupPython] Na_element015  label="Na_element : 1"  # scripted group (container) (typed FeaturePython)
  n = 1
  ref = Na_element
FEATURE [App::DocumentObjectGroupPython] I_element009  label="I_element : 005"  # scripted group (container) (typed FeaturePython)
  n = 1
  ref = I_element
FEATURE [App::DocumentObjectGroupPython] G4_SODIUM_IODIDE  # scripted group (container) (typed FeaturePython)
  Dunit = g/cm3
  Dvalue = 3.667
  Group = -> [Na_element015,I_element009]
  conduct = 2
  density = 1
  expand = 3
  formula = G4_SODIUM_IODIDE
  name = G4_SODIUM_IODIDE
  specific = 4
FEATURE [App::DocumentObjectGroupPython] Na_element016  label="Na_element : 003"  # scripted group (container) (typed FeaturePython)
  n = 2
  ref = Na_element
FEATURE [App::DocumentObjectGroupPython] O_element090  label="O_element : 050"  # scripted group (container) (typed FeaturePython)
  n = 1
  ref = O_element
FEATURE [App::DocumentObjectGroupPython] G4_SODIUM_MONOXIDE  # scripted group (container) (typed FeaturePython)
  Dunit = g/cm3
  Dvalue = 2.27
  Group = -> [Na_element016,O_element090]
  conduct = 2
  density = 1
  expand = 3
  formula = G4_SODIUM_MONOXIDE
  name = G4_SODIUM_MONOXIDE
  specific = 4
FEATURE [App::DocumentObjectGroupPython] Na_element017  label="Na_element : 004"  # scripted group (container) (typed FeaturePython)
  n = 1
  ref = Na_element
FEATURE [App::DocumentObjectGroupPython] N_element040  label="N_element : 018"  # scripted group (container) (typed FeaturePython)
  n = 1
  ref = N_element
FEATURE [App::DocumentObjectGroupPython] O_element091  label="O_element : 051"  # scripted group (container) (typed FeaturePython)
  n = 3
  ref = O_element
FEATURE [App::DocumentObjectGroupPython] G4_SODIUM_NITRATE  # scripted group (container) (typed FeaturePython)
  Dunit = g/cm3
  Dvalue = 2.261
  Group = -> [Na_element017,N_element040,O_element091]
  conduct = 2
  density = 1
  expand = 3
  formula = G4_SODIUM_NITRATE
  name = G4_SODIUM_NITRATE
  specific = 4
FEATURE [App::DocumentObjectGroupPython] C_element105  label="C_element : 059"  # scripted group (container) (typed FeaturePython)
  n = 14
  ref = C_element
FEATURE [App::DocumentObjectGroupPython] H_element096  label="H_element : 053"  # scripted group (container) (typed FeaturePython)
  n = 12
  ref = H_element
FEATURE [App::DocumentObjectGroupPython] G4_STILBENE  # scripted group (container) (typed FeaturePython)
  Dunit = g/cm3
  Dvalue = 0.9707
  Group = -> [C_element105,H_element096]
  conduct = 2
  density = 1
  expand = 3
  formula = G4_STILBENE
  name = G4_STILBENE
  specific = 4
FEATURE [App::DocumentObjectGroupPython] C_element106  label="C_element : 12"  # scripted group (container) (typed FeaturePython)
  n = 12
  ref = C_element
FEATURE [App::DocumentObjectGroupPython] H_element097  label="H_element : 22"  # scripted group (container) (typed FeaturePython)
  n = 22
  ref = H_element
FEATURE [App::DocumentObjectGroupPython] O_element092  label="O_element : 11"  # scripted group (container) (typed FeaturePython)
  n = 11
  ref = O_element
FEATURE [App::DocumentObjectGroupPython] G4_SUCROSE  # scripted group (container) (typed FeaturePython)
  Dunit = g/cm3
  Dvalue = 1.5805
  Group = -> [C_element106,H_element097,O_element092]
  conduct = 2
  density = 1
  expand = 3
  formula = G4_SUCROSE
  name = G4_SUCROSE
  specific = 4
FEATURE [App::DocumentObjectGroupPython] C_element107  label="C_element : 18"  # scripted group (container) (typed FeaturePython)
  n = 18
  ref = C_element
FEATURE [App::DocumentObjectGroupPython] H_element098  label="H_element : 054"  # scripted group (container) (typed FeaturePython)
  n = 14
  ref = H_element
FEATURE [App::DocumentObjectGroupPython] G4_TERPHENYL  # scripted group (container) (typed FeaturePython)
  Dunit = g/cm3
  Dvalue = 1.24
  Group = -> [C_element107,H_element098]
  conduct = 2
  density = 1
  expand = 3
  formula = G4_TERPHENYL
  name = G4_TERPHENYL
  specific = 4
FEATURE [App::DocumentObjectGroupPython] H_element099  label="H_element : 0.146"  # scripted group (container) (typed FeaturePython)
  n = 0.106
FEATURE [App::DocumentObjectGroupPython] C_element108  label="C_element : 0.883"  # scripted group (container) (typed FeaturePython)
  n = 0.099
FEATURE [App::DocumentObjectGroupPython] N_element041  label="N_element : 0.020"  # scripted group (container) (typed FeaturePython)
  n = 0.02
FEATURE [App::DocumentObjectGroupPython] O_element093  label="O_element : 0.766"  # scripted group (container) (typed FeaturePython)
  n = 0.766
FEATURE [App::DocumentObjectGroupPython] Na_element018  label="Na_element : 0.101"  # scripted group (container) (typed FeaturePython)
  n = 0.002
FEATURE [App::DocumentObjectGroupPython] P_element010  label="P_element : 0.108"  # scripted group (container) (typed FeaturePython)
  n = 0.001
FEATURE [App::DocumentObjectGroupPython] S_element021  label="S_element : 0.022"  # scripted group (container) (typed FeaturePython)
  n = 0.002
FEATURE [App::DocumentObjectGroupPython] Cl_element024  label="Cl_element : 0.002"  # scripted group (container) (typed FeaturePython)
  n = 0.002
FEATURE [App::DocumentObjectGroupPython] K_element011  label="K_element : 0.017"  # scripted group (container) (typed FeaturePython)
  n = 0.002
FEATURE [App::DocumentObjectGroupPython] G4_TESTIS_ICRP  # scripted group (container) (typed FeaturePython)
  Dunit = g/cm3
  Dvalue = 1.04
  Group = -> [H_element099,C_element108,N_element041,O_element093,Na_element018,P_element010,S_element021,Cl_element024,K_element011]
  conduct = 2
  density = 1
  expand = 3
  formula = G4_TESTIS_ICRP
  name = G4_TESTIS_ICRP
  specific = 4
FEATURE [App::DocumentObjectGroupPython] C_element109  label="C_element : 060"  # scripted group (container) (typed FeaturePython)
  n = 2
  ref = C_element
FEATURE [App::DocumentObjectGroupPython] Cl_element025  label="Cl_element : 012"  # scripted group (container) (typed FeaturePython)
  n = 4
  ref = Cl_element
FEATURE [App::DocumentObjectGroupPython] G4_TETRACHLOROETHYLENE  # scripted group (container) (typed FeaturePython)
  Dunit = g/cm3
  Dvalue = 1.625
  Group = -> [C_element109,Cl_element025]
  conduct = 2
  density = 1
  expand = 3
  formula = G4_TETRACHLOROETHYLENE
  name = G4_TETRACHLOROETHYLENE
  specific = 4
FEATURE [App::DocumentObjectGroupPython] Tl_element001  label="Tl_element : 1"  # scripted group (container) (typed FeaturePython)
  n = 1
  ref = Tl_element
FEATURE [App::DocumentObjectGroupPython] Cl_element026  label="Cl_element : 013"  # scripted group (container) (typed FeaturePython)
  n = 1
  ref = Cl_element
FEATURE [App::DocumentObjectGroupPython] G4_THALLIUM_CHLORIDE  # scripted group (container) (typed FeaturePython)
  Dunit = g/cm3
  Dvalue = 7.004
  Group = -> [Tl_element001,Cl_element026]
  conduct = 2
  density = 1
  expand = 3
  formula = G4_THALLIUM_CHLORIDE
  name = G4_THALLIUM_CHLORIDE
  specific = 4
FEATURE [App::DocumentObjectGroupPython] H_element100  label="H_element : 0.147"  # scripted group (container) (typed FeaturePython)
  n = 0.105
FEATURE [App::DocumentObjectGroupPython] C_element110  label="C_element : 0.256"  # scripted group (container) (typed FeaturePython)
  n = 0.256
FEATURE [App::DocumentObjectGroupPython] N_element042  label="N_element : 0.760"  # scripted group (container) (typed FeaturePython)
  n = 0.027
FEATURE [App::DocumentObjectGroupPython] O_element094  label="O_element : 0.602"  # scripted group (container) (typed FeaturePython)
  n = 0.602
FEATURE [App::DocumentObjectGroupPython] Na_element019  label="Na_element : 0.102"  # scripted group (container) (typed FeaturePython)
  n = 0.001
FEATURE [App::DocumentObjectGroupPython] P_element011  label="P_element : 0.109"  # scripted group (container) (typed FeaturePython)
  n = 0.002
FEATURE [App::DocumentObjectGroupPython] S_element022  label="S_element : 0.023"  # scripted group (container) (typed FeaturePython)
  n = 0.003
FEATURE [App::DocumentObjectGroupPython] Cl_element027  label="Cl_element : 0.591"  # scripted group (container) (typed FeaturePython)
  n = 0.002
FEATURE [App::DocumentObjectGroupPython] K_element012  label="K_element : 0.018"  # scripted group (container) (typed FeaturePython)
  n = 0.002
FEATURE [App::DocumentObjectGroupPython] G4_TISSUE_SOFT_ICRP  # scripted group (container) (typed FeaturePython)
  Dunit = g/cm3
  Dvalue = 1.03
  Group = -> [H_element100,C_element110,N_element042,O_element094,Na_element019,P_element011,S_element022,Cl_element027,K_element012]
  conduct = 2
  density = 1
  expand = 3
  formula = G4_TISSUE_SOFT_ICRP
  name = G4_TISSUE_SOFT_ICRP
  specific = 4
FEATURE [App::DocumentObjectGroupPython] H_element101  label="H_element : 0.148"  # scripted group (container) (typed FeaturePython)
  n = 0.101
FEATURE [App::DocumentObjectGroupPython] C_element111  label="C_element : 0.111"  # scripted group (container) (typed FeaturePython)
  n = 0.111
FEATURE [App::DocumentObjectGroupPython] N_element043  label="N_element : 0.026"  # scripted group (container) (typed FeaturePython)
  n = 0.026
FEATURE [App::DocumentObjectGroupPython] O_element095  label="O_element : 0.762"  # scripted group (container) (typed FeaturePython)
  n = 0.762
FEATURE [App::DocumentObjectGroupPython] G4_TISSUE_SOFT_ICRU_4  label="G4_TISSUE_SOFT_ICRU-4"  # scripted group (container) (typed FeaturePython)
  Dunit = g/cm3
  Dvalue = 1
  Group = -> [H_element101,C_element111,N_element043,O_element095]
  conduct = 2
  density = 1
  expand = 3
  formula = G4_TISSUE_SOFT_ICRU-4
  name = G4_TISSUE_SOFT_ICRU-4
  specific = 4
FEATURE [App::DocumentObjectGroupPython] H_element102  label="H_element : 0.149"  # scripted group (container) (typed FeaturePython)
  n = 0.101869
FEATURE [App::DocumentObjectGroupPython] C_element112  label="C_element : 0.456"  # scripted group (container) (typed FeaturePython)
  n = 0.456179
FEATURE [App::DocumentObjectGroupPython] N_element044  label="N_element : 0.761"  # scripted group (container) (typed FeaturePython)
  n = 0.035172
FEATURE [App::DocumentObjectGroupPython] O_element096  label="O_element : 0.407"  # scripted group (container) (typed FeaturePython)
  n = 0.40678
FEATURE [App::DocumentObjectGroupPython] G4_TISSUE_METHANE  label="G4_TISSUE-METHANE"  # scripted group (container) (typed FeaturePython)
  Dunit = g/cm3
  Dvalue = 0.00106409
  Group = -> [H_element102,C_element112,N_element044,O_element096]
  conduct = 2
  density = 1
  expand = 3
  formula = G4_TISSUE-METHANE
  name = G4_TISSUE-METHANE
  specific = 4
FEATURE [App::DocumentObjectGroupPython] H_element103  label="H_element : 0.103"  # scripted group (container) (typed FeaturePython)
  n = 0.102672
FEATURE [App::DocumentObjectGroupPython] C_element113  label="C_element : 0.569"  # scripted group (container) (typed FeaturePython)
  n = 0.56894
FEATURE [App::DocumentObjectGroupPython] N_element045  label="N_element : 0.762"  # scripted group (container) (typed FeaturePython)
  n = 0.035022
FEATURE [App::DocumentObjectGroupPython] O_element097  label="O_element : 0.293"  # scripted group (container) (typed FeaturePython)
  n = 0.293366
FEATURE [App::DocumentObjectGroupPython] G4_TISSUE_PROPANE  label="G4_TISSUE-PROPANE"  # scripted group (container) (typed FeaturePython)
  Dunit = g/cm3
  Dvalue = 0.00182628
  Group = -> [H_element103,C_element113,N_element045,O_element097]
  conduct = 2
  density = 1
  expand = 3
  formula = G4_TISSUE-PROPANE
  name = G4_TISSUE-PROPANE
  specific = 4
FEATURE [App::DocumentObjectGroupPython] Ti_element003  label="Ti_element : 1"  # scripted group (container) (typed FeaturePython)
  n = 1
  ref = Ti_element
FEATURE [App::DocumentObjectGroupPython] O_element098  label="O_element : 052"  # scripted group (container) (typed FeaturePython)
  n = 2
  ref = O_element
FEATURE [App::DocumentObjectGroupPython] G4_TITANIUM_DIOXIDE  # scripted group (container) (typed FeaturePython)
  Dunit = g/cm3
  Dvalue = 4.26
  Group = -> [Ti_element003,O_element098]
  conduct = 2
  density = 1
  expand = 3
  formula = G4_TITANIUM_DIOXIDE
  name = G4_TITANIUM_DIOXIDE
  specific = 4
FEATURE [App::DocumentObjectGroupPython] C_element114  label="C_element : 061"  # scripted group (container) (typed FeaturePython)
  n = 7
  ref = C_element
FEATURE [App::DocumentObjectGroupPython] H_element104  label="H_element : 055"  # scripted group (container) (typed FeaturePython)
  n = 8
  ref = H_element
FEATURE [App::DocumentObjectGroupPython] G4_TOLUENE  # scripted group (container) (typed FeaturePython)
  Dunit = g/cm3
  Dvalue = 0.8669
  Group = -> [C_element114,H_element104]
  conduct = 2
  density = 1
  expand = 3
  formula = G4_TOLUENE
  name = G4_TOLUENE
  specific = 4
FEATURE [App::DocumentObjectGroupPython] C_element115  label="C_element : 062"  # scripted group (container) (typed FeaturePython)
  n = 2
  ref = C_element
FEATURE [App::DocumentObjectGroupPython] H_element105  label="H_element : 056"  # scripted group (container) (typed FeaturePython)
  n = 1
  ref = H_element
FEATURE [App::DocumentObjectGroupPython] Cl_element028  label="Cl_element : 014"  # scripted group (container) (typed FeaturePython)
  n = 3
  ref = Cl_element
FEATURE [App::DocumentObjectGroupPython] G4_TRICHLOROETHYLENE  # scripted group (container) (typed FeaturePython)
  Dunit = g/cm3
  Dvalue = 1.46
  Group = -> [C_element115,H_element105,Cl_element028]
  conduct = 2
  density = 1
  expand = 3
  formula = G4_TRICHLOROETHYLENE
  name = G4_TRICHLOROETHYLENE
  specific = 4
FEATURE [App::DocumentObjectGroupPython] C_element116  label="C_element : 063"  # scripted group (container) (typed FeaturePython)
  n = 6
  ref = C_element
FEATURE [App::DocumentObjectGroupPython] H_element106  label="H_element : 15"  # scripted group (container) (typed FeaturePython)
  n = 15
  ref = H_element
FEATURE [App::DocumentObjectGroupPython] O_element099  label="O_element : 053"  # scripted group (container) (typed FeaturePython)
  n = 4
  ref = O_element
FEATURE [App::DocumentObjectGroupPython] P_element012  label="P_element : 1"  # scripted group (container) (typed FeaturePython)
  n = 1
  ref = P_element
FEATURE [App::DocumentObjectGroupPython] G4_TRIETHYL_PHOSPHATE  # scripted group (container) (typed FeaturePython)
  Dunit = g/cm3
  Dvalue = 1.07
  Group = -> [C_element116,H_element106,O_element099,P_element012]
  conduct = 2
  density = 1
  expand = 3
  formula = G4_TRIETHYL_PHOSPHATE
  name = G4_TRIETHYL_PHOSPHATE
  specific = 4
FEATURE [App::DocumentObjectGroupPython] W_element003  label="W_element : 003"  # scripted group (container) (typed FeaturePython)
  n = 1
  ref = W_element
FEATURE [App::DocumentObjectGroupPython] F_element017  label="F_element : 6"  # scripted group (container) (typed FeaturePython)
  n = 6
  ref = F_element
FEATURE [App::DocumentObjectGroupPython] G4_TUNGSTEN_HEXAFLUORIDE  # scripted group (container) (typed FeaturePython)
  Dunit = g/cm3
  Dvalue = 2.4
  Group = -> [W_element003,F_element017]
  conduct = 2
  density = 1
  expand = 3
  formula = G4_TUNGSTEN_HEXAFLUORIDE
  name = G4_TUNGSTEN_HEXAFLUORIDE
  specific = 4
FEATURE [App::DocumentObjectGroupPython] U_element001  label="U_element : 1"  # scripted group (container) (typed FeaturePython)
  n = 1
  ref = U_element
FEATURE [App::DocumentObjectGroupPython] C_element117  label="C_element : 064"  # scripted group (container) (typed FeaturePython)
  n = 2
  ref = C_element
FEATURE [App::DocumentObjectGroupPython] G4_URANIUM_DICARBIDE  # scripted group (container) (typed FeaturePython)
  Dunit = g/cm3
  Dvalue = 11.28
  Group = -> [U_element001,C_element117]
  conduct = 2
  density = 1
  expand = 3
  formula = G4_URANIUM_DICARBIDE
  name = G4_URANIUM_DICARBIDE
  specific = 4
FEATURE [App::DocumentObjectGroupPython] U_element002  label="U_element : 002"  # scripted group (container) (typed FeaturePython)
  n = 1
  ref = U_element
FEATURE [App::DocumentObjectGroupPython] C_element118  label="C_element : 065"  # scripted group (container) (typed FeaturePython)
  n = 1
  ref = C_element
FEATURE [App::DocumentObjectGroupPython] G4_URANIUM_MONOCARBIDE  # scripted group (container) (typed FeaturePython)
  Dunit = g/cm3
  Dvalue = 13.63
  Group = -> [U_element002,C_element118]
  conduct = 2
  density = 1
  expand = 3
  formula = G4_URANIUM_MONOCARBIDE
  name = G4_URANIUM_MONOCARBIDE
  specific = 4
FEATURE [App::DocumentObjectGroupPython] U_element003  label="U_element : 003"  # scripted group (container) (typed FeaturePython)
  n = 1
  ref = U_element
FEATURE [App::DocumentObjectGroupPython] O_element100  label="O_element : 054"  # scripted group (container) (typed FeaturePython)
  n = 2
  ref = O_element
FEATURE [App::DocumentObjectGroupPython] G4_URANIUM_OXIDE  # scripted group (container) (typed FeaturePython)
  Dunit = g/cm3
  Dvalue = 10.96
  Group = -> [U_element003,O_element100]
  conduct = 2
  density = 1
  expand = 3
  formula = G4_URANIUM_OXIDE
  name = G4_URANIUM_OXIDE
  specific = 4
FEATURE [App::DocumentObjectGroupPython] C_element119  label="C_element : 066"  # scripted group (container) (typed FeaturePython)
  n = 1
  ref = C_element
FEATURE [App::DocumentObjectGroupPython] H_element107  label="H_element : 057"  # scripted group (container) (typed FeaturePython)
  n = 4
  ref = H_element
FEATURE [App::DocumentObjectGroupPython] N_element046  label="N_element : 019"  # scripted group (container) (typed FeaturePython)
  n = 2
  ref = N_element
FEATURE [App::DocumentObjectGroupPython] O_element101  label="O_element : 055"  # scripted group (container) (typed FeaturePython)
  n = 1
  ref = O_element
FEATURE [App::DocumentObjectGroupPython] G4_UREA  # scripted group (container) (typed FeaturePython)
  Dunit = g/cm3
  Dvalue = 1.323
  Group = -> [C_element119,H_element107,N_element046,O_element101]
  conduct = 2
  density = 1
  expand = 3
  formula = G4_UREA
  name = G4_UREA
  specific = 4
FEATURE [App::DocumentObjectGroupPython] C_element120  label="C_element : 067"  # scripted group (container) (typed FeaturePython)
  n = 5
  ref = C_element
FEATURE [App::DocumentObjectGroupPython] H_element108  label="H_element : 058"  # scripted group (container) (typed FeaturePython)
  n = 11
  ref = H_element
FEATURE [App::DocumentObjectGroupPython] N_element047  label="N_element : 020"  # scripted group (container) (typed FeaturePython)
  n = 1
  ref = N_element
FEATURE [App::DocumentObjectGroupPython] O_element102  label="O_element : 056"  # scripted group (container) (typed FeaturePython)
  n = 2
  ref = O_element
FEATURE [App::DocumentObjectGroupPython] G4_VALINE  # scripted group (container) (typed FeaturePython)
  Dunit = g/cm3
  Dvalue = 1.23
  Group = -> [C_element120,H_element108,N_element047,O_element102]
  conduct = 2
  density = 1
  expand = 3
  formula = G4_VALINE
  name = G4_VALINE
  specific = 4
FEATURE [App::DocumentObjectGroupPython] H_element109  label="H_element : 0.009"  # scripted group (container) (typed FeaturePython)
  n = 0.009417
FEATURE [App::DocumentObjectGroupPython] C_element121  label="C_element : 0.281"  # scripted group (container) (typed FeaturePython)
  n = 0.280555
FEATURE [App::DocumentObjectGroupPython] F_element018  label="F_element : 0.710"  # scripted group (container) (typed FeaturePython)
  n = 0.710028
FEATURE [App::DocumentObjectGroupPython] G4_VITON  # scripted group (container) (typed FeaturePython)
  Dunit = g/cm3
  Dvalue = 1.8
  Group = -> [H_element109,C_element121,F_element018]
  conduct = 2
  density = 1
  expand = 3
  formula = G4_VITON
  name = G4_VITON
  specific = 4
FEATURE [App::DocumentObjectGroupPython] H_element110  label="H_element : 059"  # scripted group (container) (typed FeaturePython)
  n = 2
  ref = H_element
FEATURE [App::DocumentObjectGroupPython] O_element103  label="O_element : 057"  # scripted group (container) (typed FeaturePython)
  n = 1
  ref = O_element
FEATURE [App::DocumentObjectGroupPython] G4_WATER  # scripted group (container) (typed FeaturePython)
  Dunit = g/cm3
  Dvalue = 1
  Group = -> [H_element110,O_element103]
  conduct = 2
  density = 1
  expand = 3
  formula = G4_WATER
  name = G4_WATER
  specific = 4
FEATURE [App::DocumentObjectGroupPython] H_element111  label="H_element : 060"  # scripted group (container) (typed FeaturePython)
  n = 2
  ref = H_element
FEATURE [App::DocumentObjectGroupPython] O_element104  label="O_element : 058"  # scripted group (container) (typed FeaturePython)
  n = 1
  ref = O_element
FEATURE [App::DocumentObjectGroupPython] G4_WATER_VAPOR  # scripted group (container) (typed FeaturePython)
  Dunit = g/cm3
  Dvalue = 0.000756182
  Group = -> [H_element111,O_element104]
  conduct = 2
  density = 1
  expand = 3
  formula = G4_WATER_VAPOR
  name = G4_WATER_VAPOR
  specific = 4
FEATURE [App::DocumentObjectGroupPython] C_element122  label="C_element : 068"  # scripted group (container) (typed FeaturePython)
  n = 8
  ref = C_element
FEATURE [App::DocumentObjectGroupPython] H_element112  label="H_element : 061"  # scripted group (container) (typed FeaturePython)
  n = 10
  ref = H_element
FEATURE [App::DocumentObjectGroupPython] G4_XYLENE  # scripted group (container) (typed FeaturePython)
  Dunit = g/cm3
  Dvalue = 0.87
  Group = -> [C_element122,H_element112]
  conduct = 2
  density = 1
  expand = 3
  formula = G4_XYLENE
  name = G4_XYLENE
  specific = 4
FEATURE [App::DocumentObjectGroupPython] C_element123  label="C_element : 069"  # scripted group (container) (typed FeaturePython)
  n = 1
  ref = C_element
FEATURE [App::DocumentObjectGroupPython] G4_GRAPHITE  # scripted group (container) (typed FeaturePython)
  Dunit = g/cm3
  Dvalue = 2.21
  Group = -> [C_element123]
  conduct = 2
  density = 1
  expand = 3
  formula = G4_GRAPHITE
  name = G4_GRAPHITE
  specific = 4
FEATURE [App::DocumentObjectGroupPython] NIST  # scripted group (container) (typed FeaturePython)
  Group = -> [G4_A_150_TISSUE,G4_ACETONE,G4_ACETYLENE,G4_ADENINE,G4_ADIPOSE_TISSUE_ICRP,G4_AIR,G4_ALANINE,G4_ALUMINUM_OXIDE,G4_AMBER,G4_AMMONIA,G4_ANILINE,G4_ANTHRACENE,G4_B_100_BONE,G4_BAKELITE,G4_BARIUM_FLUORIDE,G4_BARIUM_SULFATE,G4_BENZENE,G4_BERYLLIUM_OXIDE,G4_BGO,G4_BLOOD_ICRP,G4_BONE_COMPACT_ICRU,G4_BONE_CORTICAL_ICRP,G4_BORON_CARBIDE,G4_BORON_OXIDE,G4_BRAIN_ICRP,G4_BUTANE,G4_N_BUTYL_ALCOHOL,G4_C_552,+152 more]
FEATURE [App::DocumentObjectGroupPython] H_element113  label="H_element : 062"  # scripted group (container) (typed FeaturePython)
  n = 1
  ref = H_element
FEATURE [App::DocumentObjectGroupPython] G4_H  # scripted group (container) (typed FeaturePython)
  Dunit = g/cm3
  Dvalue = 8.3748e-05
  Group = -> [H_element113]
  conduct = 2
  density = 1
  expand = 3
  formula = H
  name = G4_H
  specific = 4
FEATURE [App::DocumentObjectGroupPython] He_element001  label="He_element : 1"  # scripted group (container) (typed FeaturePython)
  n = 1
  ref = He_element
FEATURE [App::DocumentObjectGroupPython] G4_He  # scripted group (container) (typed FeaturePython)
  Dunit = g/cm3
  Dvalue = 0.000166322
  Group = -> [He_element001]
  conduct = 2
  density = 1
  expand = 3
  formula = He
  name = G4_He
  specific = 4
FEATURE [App::DocumentObjectGroupPython] Li_element008  label="Li_element : 008"  # scripted group (container) (typed FeaturePython)
  n = 1
  ref = Li_element
FEATURE [App::DocumentObjectGroupPython] G4_Li  # scripted group (container) (typed FeaturePython)
  Dunit = g/cm3
  Dvalue = 0.534
  Group = -> [Li_element008]
  conduct = 2
  density = 1
  expand = 3
  formula = Li
  name = G4_Li
  specific = 4
FEATURE [App::DocumentObjectGroupPython] Be_element002  label="Be_element : 002"  # scripted group (container) (typed FeaturePython)
  n = 1
  ref = Be_element
FEATURE [App::DocumentObjectGroupPython] G4_Be  # scripted group (container) (typed FeaturePython)
  Dunit = g/cm3
  Dvalue = 1.848
  Group = -> [Be_element002]
  conduct = 2
  density = 1
  expand = 3
  formula = Be
  name = G4_Be
  specific = 4
FEATURE [App::DocumentObjectGroupPython] B_element007  label="B_element : 007"  # scripted group (container) (typed FeaturePython)
  n = 1
  ref = B_element
FEATURE [App::DocumentObjectGroupPython] G4_B  # scripted group (container) (typed FeaturePython)
  Dunit = g/cm3
  Dvalue = 2.37
  Group = -> [B_element007]
  conduct = 2
  density = 1
  expand = 3
  formula = B
  name = G4_B
  specific = 4
FEATURE [App::DocumentObjectGroupPython] C_element124  label="C_element : 070"  # scripted group (container) (typed FeaturePython)
  n = 1
  ref = C_element
FEATURE [App::DocumentObjectGroupPython] G4_C  # scripted group (container) (typed FeaturePython)
  Dunit = g/cm3
  Dvalue = 2
  Group = -> [C_element124]
  conduct = 2
  density = 1
  expand = 3
  formula = C
  name = G4_C
  specific = 4
FEATURE [App::DocumentObjectGroupPython] N_element048  label="N_element : 021"  # scripted group (container) (typed FeaturePython)
  n = 1
  ref = N_element
FEATURE [App::DocumentObjectGroupPython] G4_N  # scripted group (container) (typed FeaturePython)
  Dunit = g/cm3
  Dvalue = 0.0011652
  Group = -> [N_element048]
  conduct = 2
  density = 1
  expand = 3
  formula = N
  name = G4_N
  specific = 4
FEATURE [App::DocumentObjectGroupPython] O_element105  label="O_element : 059"  # scripted group (container) (typed FeaturePython)
  n = 1
  ref = O_element
FEATURE [App::DocumentObjectGroupPython] G4_O  # scripted group (container) (typed FeaturePython)
  Dunit = g/cm3
  Dvalue = 0.00133151
  Group = -> [O_element105]
  conduct = 2
  density = 1
  expand = 3
  formula = O
  name = G4_O
  specific = 4
FEATURE [App::DocumentObjectGroupPython] F_element019  label="F_element : 008"  # scripted group (container) (typed FeaturePython)
  n = 1
  ref = F_element
FEATURE [App::DocumentObjectGroupPython] G4_F  # scripted group (container) (typed FeaturePython)
  Dunit = g/cm3
  Dvalue = 0.00158029
  Group = -> [F_element019]
  conduct = 2
  density = 1
  expand = 3
  formula = F
  name = G4_F
  specific = 4
FEATURE [App::DocumentObjectGroupPython] Ne_element001  label="Ne_element : 1"  # scripted group (container) (typed FeaturePython)
  n = 1
  ref = Ne_element
FEATURE [App::DocumentObjectGroupPython] G4_Ne  # scripted group (container) (typed FeaturePython)
  Dunit = g/cm3
  Dvalue = 0.000838505
  Group = -> [Ne_element001]
  conduct = 2
  density = 1
  expand = 3
  formula = Ne
  name = G4_Ne
  specific = 4
FEATURE [App::DocumentObjectGroupPython] Na_element020  label="Na_element : 005"  # scripted group (container) (typed FeaturePython)
  n = 1
  ref = Na_element
FEATURE [App::DocumentObjectGroupPython] G4_Na  # scripted group (container) (typed FeaturePython)
  Dunit = g/cm3
  Dvalue = 0.971
  Group = -> [Na_element020]
  conduct = 2
  density = 1
  expand = 3
  formula = Na
  name = G4_Na
  specific = 4
FEATURE [App::DocumentObjectGroupPython] Mg_element011  label="Mg_element : 005"  # scripted group (container) (typed FeaturePython)
  n = 1
  ref = Mg_element
FEATURE [App::DocumentObjectGroupPython] G4_Mg  # scripted group (container) (typed FeaturePython)
  Dunit = g/cm3
  Dvalue = 1.74
  Group = -> [Mg_element011]
  conduct = 2
  density = 1
  expand = 3
  formula = Mg
  name = G4_Mg
  specific = 4
FEATURE [App::DocumentObjectGroupPython] Al_element004  label="Al_element : 1"  # scripted group (container) (typed FeaturePython)
  n = 1
  ref = Al_element
FEATURE [App::DocumentObjectGroupPython] G4_Al  # scripted group (container) (typed FeaturePython)
  Dunit = g/cm3
  Dvalue = 2.699
  Group = -> [Al_element004]
  conduct = 2
  density = 1
  expand = 3
  formula = Al
  name = G4_Al
  specific = 4
FEATURE [App::DocumentObjectGroupPython] Si_element007  label="Si_element : 002"  # scripted group (container) (typed FeaturePython)
  n = 1
  ref = Si_element
FEATURE [App::DocumentObjectGroupPython] G4_Si  # scripted group (container) (typed FeaturePython)
  Dunit = g/cm3
  Dvalue = 2.33
  Group = -> [Si_element007]
  conduct = 2
  density = 1
  expand = 3
  formula = Si
  name = G4_Si
  specific = 4
FEATURE [App::DocumentObjectGroupPython] P_element013  label="P_element : 002"  # scripted group (container) (typed FeaturePython)
  n = 1
  ref = P_element
FEATURE [App::DocumentObjectGroupPython] G4_P  # scripted group (container) (typed FeaturePython)
  Dunit = g/cm3
  Dvalue = 2.2
  Group = -> [P_element013]
  conduct = 2
  density = 1
  expand = 3
  formula = P
  name = G4_P
  specific = 4
FEATURE [App::DocumentObjectGroupPython] S_element023  label="S_element : 007"  # scripted group (container) (typed FeaturePython)
  n = 1
  ref = S_element
FEATURE [App::DocumentObjectGroupPython] G4_S  # scripted group (container) (typed FeaturePython)
  Dunit = g/cm3
  Dvalue = 2
  Group = -> [S_element023]
  conduct = 2
  density = 1
  expand = 3
  formula = S
  name = G4_S
  specific = 4
FEATURE [App::DocumentObjectGroupPython] Cl_element029  label="Cl_element : 015"  # scripted group (container) (typed FeaturePython)
  n = 1
  ref = Cl_element
FEATURE [App::DocumentObjectGroupPython] G4_Cl  # scripted group (container) (typed FeaturePython)
  Dunit = g/cm3
  Dvalue = 0.00299473
  Group = -> [Cl_element029]
  conduct = 2
  density = 1
  expand = 3
  formula = Cl
  name = G4_Cl
  specific = 4
FEATURE [App::DocumentObjectGroupPython] Ar_element002  label="Ar_element : 1"  # scripted group (container) (typed FeaturePython)
  n = 1
  ref = Ar_element
FEATURE [App::DocumentObjectGroupPython] G4_Ar  # scripted group (container) (typed FeaturePython)
  Dunit = g/cm3
  Dvalue = 0.00166201
  Group = -> [Ar_element002]
  conduct = 2
  density = 1
  expand = 3
  formula = Ar
  name = G4_Ar
  specific = 4
FEATURE [App::DocumentObjectGroupPython] K_element013  label="K_element : 003"  # scripted group (container) (typed FeaturePython)
  n = 1
  ref = K_element
FEATURE [App::DocumentObjectGroupPython] G4_K  # scripted group (container) (typed FeaturePython)
  Dunit = g/cm3
  Dvalue = 0.862
  Group = -> [K_element013]
  conduct = 2
  density = 1
  expand = 3
  formula = K
  name = G4_K
  specific = 4
FEATURE [App::DocumentObjectGroupPython] Ca_element014  label="Ca_element : 007"  # scripted group (container) (typed FeaturePython)
  n = 1
  ref = Ca_element
FEATURE [App::DocumentObjectGroupPython] G4_Ca  # scripted group (container) (typed FeaturePython)
  Dunit = g/cm3
  Dvalue = 1.55
  Group = -> [Ca_element014]
  conduct = 2
  density = 1
  expand = 3
  formula = Ca
  name = G4_Ca
  specific = 4
FEATURE [App::DocumentObjectGroupPython] Sc_element001  label="Sc_element : 1"  # scripted group (container) (typed FeaturePython)
  n = 1
  ref = Sc_element
FEATURE [App::DocumentObjectGroupPython] G4_Sc  # scripted group (container) (typed FeaturePython)
  Dunit = g/cm3
  Dvalue = 2.989
  Group = -> [Sc_element001]
  conduct = 2
  density = 1
  expand = 3
  formula = Sc
  name = G4_Sc
  specific = 4
FEATURE [App::DocumentObjectGroupPython] Ti_element004  label="Ti_element : 002"  # scripted group (container) (typed FeaturePython)
  n = 1
  ref = Ti_element
FEATURE [App::DocumentObjectGroupPython] G4_Ti  # scripted group (container) (typed FeaturePython)
  Dunit = g/cm3
  Dvalue = 4.54
  Group = -> [Ti_element004]
  conduct = 2
  density = 1
  expand = 3
  formula = Ti
  name = G4_Ti
  specific = 4
FEATURE [App::DocumentObjectGroupPython] V_element001  label="V_element : 1"  # scripted group (container) (typed FeaturePython)
  n = 1
  ref = V_element
FEATURE [App::DocumentObjectGroupPython] G4_V  # scripted group (container) (typed FeaturePython)
  Dunit = g/cm3
  Dvalue = 6.11
  Group = -> [V_element001]
  conduct = 2
  density = 1
  expand = 3
  formula = V
  name = G4_V
  specific = 4
FEATURE [App::DocumentObjectGroupPython] Cr_element001  label="Cr_element : 1"  # scripted group (container) (typed FeaturePython)
  n = 1
  ref = Cr_element
FEATURE [App::DocumentObjectGroupPython] G4_Cr  # scripted group (container) (typed FeaturePython)
  Dunit = g/cm3
  Dvalue = 7.18
  Group = -> [Cr_element001]
  conduct = 2
  density = 1
  expand = 3
  formula = Cr
  name = G4_Cr
  specific = 4
FEATURE [App::DocumentObjectGroupPython] Mn_element001  label="Mn_element : 1"  # scripted group (container) (typed FeaturePython)
  n = 1
  ref = Mn_element
FEATURE [App::DocumentObjectGroupPython] G4_Mn  # scripted group (container) (typed FeaturePython)
  Dunit = g/cm3
  Dvalue = 7.44
  Group = -> [Mn_element001]
  conduct = 2
  density = 1
  expand = 3
  formula = Mn
  name = G4_Mn
  specific = 4
FEATURE [App::DocumentObjectGroupPython] Fe_element007  label="Fe_element : 004"  # scripted group (container) (typed FeaturePython)
  n = 1
  ref = Fe_element
FEATURE [App::DocumentObjectGroupPython] G4_Fe  # scripted group (container) (typed FeaturePython)
  Dunit = g/cm3
  Dvalue = 7.874
  Group = -> [Fe_element007]
  conduct = 2
  density = 1
  expand = 3
  formula = Fe
  name = G4_Fe
  specific = 4
FEATURE [App::DocumentObjectGroupPython] Co_element001  label="Co_element : 1"  # scripted group (container) (typed FeaturePython)
  n = 1
  ref = Co_element
FEATURE [App::DocumentObjectGroupPython] G4_Co  # scripted group (container) (typed FeaturePython)
  Dunit = g/cm3
  Dvalue = 8.9
  Group = -> [Co_element001]
  conduct = 2
  density = 1
  expand = 3
  formula = Co
  name = G4_Co
  specific = 4
FEATURE [App::DocumentObjectGroupPython] Ni_element001  label="Ni_element : 1"  # scripted group (container) (typed FeaturePython)
  n = 1
  ref = Ni_element
FEATURE [App::DocumentObjectGroupPython] G4_Ni  # scripted group (container) (typed FeaturePython)
  Dunit = g/cm3
  Dvalue = 8.902
  Group = -> [Ni_element001]
  conduct = 2
  density = 1
  expand = 3
  formula = Ni
  name = G4_Ni
  specific = 4
FEATURE [App::DocumentObjectGroupPython] Cu_element001  label="Cu_element : 1"  # scripted group (container) (typed FeaturePython)
  n = 1
  ref = Cu_element
FEATURE [App::DocumentObjectGroupPython] G4_Cu  # scripted group (container) (typed FeaturePython)
  Dunit = g/cm3
  Dvalue = 8.96
  Group = -> [Cu_element001]
  conduct = 2
  density = 1
  expand = 3
  formula = Cu
  name = G4_Cu
  specific = 4
FEATURE [App::DocumentObjectGroupPython] Zn_element001  label="Zn_element : 1"  # scripted group (container) (typed FeaturePython)
  n = 1
  ref = Zn_element
FEATURE [App::DocumentObjectGroupPython] G4_Zn  # scripted group (container) (typed FeaturePython)
  Dunit = g/cm3
  Dvalue = 7.133
  Group = -> [Zn_element001]
  conduct = 2
  density = 1
  expand = 3
  formula = Zn
  name = G4_Zn
  specific = 4
FEATURE [App::DocumentObjectGroupPython] Ga_element002  label="Ga_element : 002"  # scripted group (container) (typed FeaturePython)
  n = 1
  ref = Ga_element
FEATURE [App::DocumentObjectGroupPython] G4_Ga  # scripted group (container) (typed FeaturePython)
  Dunit = g/cm3
  Dvalue = 5.904
  Group = -> [Ga_element002]
  conduct = 2
  density = 1
  expand = 3
  formula = Ga
  name = G4_Ga
  specific = 4
FEATURE [App::DocumentObjectGroupPython] Ge_element002  label="Ge_element : 1"  # scripted group (container) (typed FeaturePython)
  n = 1
  ref = Ge_element
FEATURE [App::DocumentObjectGroupPython] G4_Ge  # scripted group (container) (typed FeaturePython)
  Dunit = g/cm3
  Dvalue = 5.323
  Group = -> [Ge_element002]
  conduct = 2
  density = 1
  expand = 3
  formula = Ge
  name = G4_Ge
  specific = 4
FEATURE [App::DocumentObjectGroupPython] As_element003  label="As_element : 002"  # scripted group (container) (typed FeaturePython)
  n = 1
  ref = As_element
FEATURE [App::DocumentObjectGroupPython] G4_As  # scripted group (container) (typed FeaturePython)
  Dunit = g/cm3
  Dvalue = 5.73
  Group = -> [As_element003]
  conduct = 2
  density = 1
  expand = 3
  formula = As
  name = G4_As
  specific = 4
FEATURE [App::DocumentObjectGroupPython] Se_element001  label="Se_element : 1"  # scripted group (container) (typed FeaturePython)
  n = 1
  ref = Se_element
FEATURE [App::DocumentObjectGroupPython] G4_Se  # scripted group (container) (typed FeaturePython)
  Dunit = g/cm3
  Dvalue = 4.5
  Group = -> [Se_element001]
  conduct = 2
  density = 1
  expand = 3
  formula = Se
  name = G4_Se
  specific = 4
FEATURE [App::DocumentObjectGroupPython] Br_element007  label="Br_element : 004"  # scripted group (container) (typed FeaturePython)
  n = 1
  ref = Br_element
FEATURE [App::DocumentObjectGroupPython] G4_Br  # scripted group (container) (typed FeaturePython)
  Dunit = g/cm3
  Dvalue = 0.0070721
  Group = -> [Br_element007]
  conduct = 2
  density = 1
  expand = 3
  formula = Br
  name = G4_Br
  specific = 4
FEATURE [App::DocumentObjectGroupPython] Kr_element001  label="Kr_element : 1"  # scripted group (container) (typed FeaturePython)
  n = 1
  ref = Kr_element
FEATURE [App::DocumentObjectGroupPython] G4_Kr  # scripted group (container) (typed FeaturePython)
  Dunit = g/cm3
  Dvalue = 0.00347832
  Group = -> [Kr_element001]
  conduct = 2
  density = 1
  expand = 3
  formula = Kr
  name = G4_Kr
  specific = 4
FEATURE [App::DocumentObjectGroupPython] Rb_element001  label="Rb_element : 1"  # scripted group (container) (typed FeaturePython)
  n = 1
  ref = Rb_element
FEATURE [App::DocumentObjectGroupPython] G4_Rb  # scripted group (container) (typed FeaturePython)
  Dunit = g/cm3
  Dvalue = 1.532
  Group = -> [Rb_element001]
  conduct = 2
  density = 1
  expand = 3
  formula = Rb
  name = G4_Rb
  specific = 4
FEATURE [App::DocumentObjectGroupPython] Sr_element001  label="Sr_element : 1"  # scripted group (container) (typed FeaturePython)
  n = 1
  ref = Sr_element
FEATURE [App::DocumentObjectGroupPython] G4_Sr  # scripted group (container) (typed FeaturePython)
  Dunit = g/cm3
  Dvalue = 2.54
  Group = -> [Sr_element001]
  conduct = 2
  density = 1
  expand = 3
  formula = Sr
  name = G4_Sr
  specific = 4
FEATURE [App::DocumentObjectGroupPython] Y_element001  label="Y_element : 1"  # scripted group (container) (typed FeaturePython)
  n = 1
  ref = Y_element
FEATURE [App::DocumentObjectGroupPython] G4_Y  # scripted group (container) (typed FeaturePython)
  Dunit = g/cm3
  Dvalue = 4.469
  Group = -> [Y_element001]
  conduct = 2
  density = 1
  expand = 3
  formula = Y
  name = G4_Y
  specific = 4
FEATURE [App::DocumentObjectGroupPython] Zr_element001  label="Zr_element : 1"  # scripted group (container) (typed FeaturePython)
  n = 1
  ref = Zr_element
FEATURE [App::DocumentObjectGroupPython] G4_Zr  # scripted group (container) (typed FeaturePython)
  Dunit = g/cm3
  Dvalue = 6.506
  Group = -> [Zr_element001]
  conduct = 2
  density = 1
  expand = 3
  formula = Zr
  name = G4_Zr
  specific = 4
FEATURE [App::DocumentObjectGroupPython] Nb_element001  label="Nb_element : 1"  # scripted group (container) (typed FeaturePython)
  n = 1
  ref = Nb_element
FEATURE [App::DocumentObjectGroupPython] G4_Nb  # scripted group (container) (typed FeaturePython)
  Dunit = g/cm3
  Dvalue = 8.57
  Group = -> [Nb_element001]
  conduct = 2
  density = 1
  expand = 3
  formula = Nb
  name = G4_Nb
  specific = 4
FEATURE [App::DocumentObjectGroupPython] Mo_element001  label="Mo_element : 1"  # scripted group (container) (typed FeaturePython)
  n = 1
  ref = Mo_element
FEATURE [App::DocumentObjectGroupPython] G4_Mo  # scripted group (container) (typed FeaturePython)
  Dunit = g/cm3
  Dvalue = 10.22
  Group = -> [Mo_element001]
  conduct = 2
  density = 1
  expand = 3
  formula = Mo
  name = G4_Mo
  specific = 4
FEATURE [App::DocumentObjectGroupPython] Tc_element001  label="Tc_element : 1"  # scripted group (container) (typed FeaturePython)
  n = 1
  ref = Tc_element
FEATURE [App::DocumentObjectGroupPython] G4_Tc  # scripted group (container) (typed FeaturePython)
  Dunit = g/cm3
  Dvalue = 11.5
  Group = -> [Tc_element001]
  conduct = 2
  density = 1
  expand = 3
  formula = Tc
  name = G4_Tc
  specific = 4
FEATURE [App::DocumentObjectGroupPython] Ru_element001  label="Ru_element : 1"  # scripted group (container) (typed FeaturePython)
  n = 1
  ref = Ru_element
FEATURE [App::DocumentObjectGroupPython] G4_Ru  # scripted group (container) (typed FeaturePython)
  Dunit = g/cm3
  Dvalue = 12.41
  Group = -> [Ru_element001]
  conduct = 2
  density = 1
  expand = 3
  formula = Ru
  name = G4_Ru
  specific = 4
FEATURE [App::DocumentObjectGroupPython] Rh_element001  label="Rh_element : 1"  # scripted group (container) (typed FeaturePython)
  n = 1
  ref = Rh_element
FEATURE [App::DocumentObjectGroupPython] G4_Rh  # scripted group (container) (typed FeaturePython)
  Dunit = g/cm3
  Dvalue = 12.41
  Group = -> [Rh_element001]
  conduct = 2
  density = 1
  expand = 3
  formula = Rh
  name = G4_Rh
  specific = 4
FEATURE [App::DocumentObjectGroupPython] Pd_element001  label="Pd_element : 1"  # scripted group (container) (typed FeaturePython)
  n = 1
  ref = Pd_element
FEATURE [App::DocumentObjectGroupPython] G4_Pd  # scripted group (container) (typed FeaturePython)
  Dunit = g/cm3
  Dvalue = 12.02
  Group = -> [Pd_element001]
  conduct = 2
  density = 1
  expand = 3
  formula = Pd
  name = G4_Pd
  specific = 4
FEATURE [App::DocumentObjectGroupPython] Ag_element006  label="Ag_element : 004"  # scripted group (container) (typed FeaturePython)
  n = 1
  ref = Ag_element
FEATURE [App::DocumentObjectGroupPython] G4_Ag  # scripted group (container) (typed FeaturePython)
  Dunit = g/cm3
  Dvalue = 10.5
  Group = -> [Ag_element006]
  conduct = 2
  density = 1
  expand = 3
  formula = Ag
  name = G4_Ag
  specific = 4
FEATURE [App::DocumentObjectGroupPython] Cd_element003  label="Cd_element : 003"  # scripted group (container) (typed FeaturePython)
  n = 1
  ref = Cd_element
FEATURE [App::DocumentObjectGroupPython] G4_Cd  # scripted group (container) (typed FeaturePython)
  Dunit = g/cm3
  Dvalue = 8.65
  Group = -> [Cd_element003]
  conduct = 2
  density = 1
  expand = 3
  formula = Cd
  name = G4_Cd
  specific = 4
FEATURE [App::DocumentObjectGroupPython] In_element001  label="In_element : 1"  # scripted group (container) (typed FeaturePython)
  n = 1
  ref = In_element
FEATURE [App::DocumentObjectGroupPython] G4_In  # scripted group (container) (typed FeaturePython)
  Dunit = g/cm3
  Dvalue = 7.31
  Group = -> [In_element001]
  conduct = 2
  density = 1
  expand = 3
  formula = In
  name = G4_In
  specific = 4
FEATURE [App::DocumentObjectGroupPython] Sn_element001  label="Sn_element : 1"  # scripted group (container) (typed FeaturePython)
  n = 1
  ref = Sn_element
FEATURE [App::DocumentObjectGroupPython] G4_Sn  # scripted group (container) (typed FeaturePython)
  Dunit = g/cm3
  Dvalue = 7.31
  Group = -> [Sn_element001]
  conduct = 2
  density = 1
  expand = 3
  formula = Sn
  name = G4_Sn
  specific = 4
FEATURE [App::DocumentObjectGroupPython] Sb_element001  label="Sb_element : 1"  # scripted group (container) (typed FeaturePython)
  n = 1
  ref = Sb_element
FEATURE [App::DocumentObjectGroupPython] G4_Sb  # scripted group (container) (typed FeaturePython)
  Dunit = g/cm3
  Dvalue = 6.691
  Group = -> [Sb_element001]
  conduct = 2
  density = 1
  expand = 3
  formula = Sb
  name = G4_Sb
  specific = 4
FEATURE [App::DocumentObjectGroupPython] Te_element002  label="Te_element : 002"  # scripted group (container) (typed FeaturePython)
  n = 1
  ref = Te_element
FEATURE [App::DocumentObjectGroupPython] G4_Te  # scripted group (container) (typed FeaturePython)
  Dunit = g/cm3
  Dvalue = 6.24
  Group = -> [Te_element002]
  conduct = 2
  density = 1
  expand = 3
  formula = Te
  name = G4_Te
  specific = 4
FEATURE [App::DocumentObjectGroupPython] I_element010  label="I_element : 006"  # scripted group (container) (typed FeaturePython)
  n = 1
  ref = I_element
FEATURE [App::DocumentObjectGroupPython] G4_I  # scripted group (container) (typed FeaturePython)
  Dunit = g/cm3
  Dvalue = 4.93
  Group = -> [I_element010]
  conduct = 2
  density = 1
  expand = 3
  formula = I
  name = G4_I
  specific = 4
FEATURE [App::DocumentObjectGroupPython] Xe_element001  label="Xe_element : 1"  # scripted group (container) (typed FeaturePython)
  n = 1
  ref = Xe_element
FEATURE [App::DocumentObjectGroupPython] G4_Xe  # scripted group (container) (typed FeaturePython)
  Dunit = g/cm3
  Dvalue = 0.00548536
  Group = -> [Xe_element001]
  conduct = 2
  density = 1
  expand = 3
  formula = Xe
  name = G4_Xe
  specific = 4
FEATURE [App::DocumentObjectGroupPython] Cs_element003  label="Cs_element : 003"  # scripted group (container) (typed FeaturePython)
  n = 1
  ref = Cs_element
FEATURE [App::DocumentObjectGroupPython] G4_Cs  # scripted group (container) (typed FeaturePython)
  Dunit = g/cm3
  Dvalue = 1.873
  Group = -> [Cs_element003]
  conduct = 2
  density = 1
  expand = 3
  formula = Cs
  name = G4_Cs
  specific = 4
FEATURE [App::DocumentObjectGroupPython] Ba_element003  label="Ba_element : 003"  # scripted group (container) (typed FeaturePython)
  n = 1
  ref = Ba_element
FEATURE [App::DocumentObjectGroupPython] G4_Ba  # scripted group (container) (typed FeaturePython)
  Dunit = g/cm3
  Dvalue = 3.5
  Group = -> [Ba_element003]
  conduct = 2
  density = 1
  expand = 3
  formula = Ba
  name = G4_Ba
  specific = 4
FEATURE [App::DocumentObjectGroupPython] La_element003  label="La_element : 003"  # scripted group (container) (typed FeaturePython)
  n = 1
  ref = La_element
FEATURE [App::DocumentObjectGroupPython] G4_La  # scripted group (container) (typed FeaturePython)
  Dunit = g/cm3
  Dvalue = 6.154
  Group = -> [La_element003]
  conduct = 2
  density = 1
  expand = 3
  formula = La
  name = G4_La
  specific = 4
FEATURE [App::DocumentObjectGroupPython] Ce_element002  label="Ce_element : 1"  # scripted group (container) (typed FeaturePython)
  n = 1
  ref = Ce_element
FEATURE [App::DocumentObjectGroupPython] G4_Ce  # scripted group (container) (typed FeaturePython)
  Dunit = g/cm3
  Dvalue = 6.657
  Group = -> [Ce_element002]
  conduct = 2
  density = 1
  expand = 3
  formula = Ce
  name = G4_Ce
  specific = 4
FEATURE [App::DocumentObjectGroupPython] Pr_element001  label="Pr_element : 1"  # scripted group (container) (typed FeaturePython)
  n = 1
  ref = Pr_element
FEATURE [App::DocumentObjectGroupPython] G4_Pr  # scripted group (container) (typed FeaturePython)
  Dunit = g/cm3
  Dvalue = 6.71
  Group = -> [Pr_element001]
  conduct = 2
  density = 1
  expand = 3
  formula = Pr
  name = G4_Pr
  specific = 4
FEATURE [App::DocumentObjectGroupPython] Nd_element001  label="Nd_element : 1"  # scripted group (container) (typed FeaturePython)
  n = 1
  ref = Nd_element
FEATURE [App::DocumentObjectGroupPython] G4_Nd  # scripted group (container) (typed FeaturePython)
  Dunit = g/cm3
  Dvalue = 6.9
  Group = -> [Nd_element001]
  conduct = 2
  density = 1
  expand = 3
  formula = Nd
  name = G4_Nd
  specific = 4
FEATURE [App::DocumentObjectGroupPython] Pm_element001  label="Pm_element : 1"  # scripted group (container) (typed FeaturePython)
  n = 1
  ref = Pm_element
FEATURE [App::DocumentObjectGroupPython] G4_Pm  # scripted group (container) (typed FeaturePython)
  Dunit = g/cm3
  Dvalue = 7.22
  Group = -> [Pm_element001]
  conduct = 2
  density = 1
  expand = 3
  formula = Pm
  name = G4_Pm
  specific = 4
FEATURE [App::DocumentObjectGroupPython] Sm_element001  label="Sm_element : 1"  # scripted group (container) (typed FeaturePython)
  n = 1
  ref = Sm_element
FEATURE [App::DocumentObjectGroupPython] G4_Sm  # scripted group (container) (typed FeaturePython)
  Dunit = g/cm3
  Dvalue = 7.46
  Group = -> [Sm_element001]
  conduct = 2
  density = 1
  expand = 3
  formula = Sm
  name = G4_Sm
  specific = 4
FEATURE [App::DocumentObjectGroupPython] Eu_element001  label="Eu_element : 1"  # scripted group (container) (typed FeaturePython)
  n = 1
  ref = Eu_element
FEATURE [App::DocumentObjectGroupPython] G4_Eu  # scripted group (container) (typed FeaturePython)
  Dunit = g/cm3
  Dvalue = 5.243
  Group = -> [Eu_element001]
  conduct = 2
  density = 1
  expand = 3
  formula = Eu
  name = G4_Eu
  specific = 4
FEATURE [App::DocumentObjectGroupPython] Gd_element002  label="Gd_element : 1"  # scripted group (container) (typed FeaturePython)
  n = 1
  ref = Gd_element
FEATURE [App::DocumentObjectGroupPython] G4_Gd  # scripted group (container) (typed FeaturePython)
  Dunit = g/cm3
  Dvalue = 7.9004
  Group = -> [Gd_element002]
  conduct = 2
  density = 1
  expand = 3
  formula = Gd
  name = G4_Gd
  specific = 4
FEATURE [App::DocumentObjectGroupPython] Tb_element001  label="Tb_element : 1"  # scripted group (container) (typed FeaturePython)
  n = 1
  ref = Tb_element
FEATURE [App::DocumentObjectGroupPython] G4_Tb  # scripted group (container) (typed FeaturePython)
  Dunit = g/cm3
  Dvalue = 8.229
  Group = -> [Tb_element001]
  conduct = 2
  density = 1
  expand = 3
  formula = Tb
  name = G4_Tb
  specific = 4
FEATURE [App::DocumentObjectGroupPython] Dy_element001  label="Dy_element : 1"  # scripted group (container) (typed FeaturePython)
  n = 1
  ref = Dy_element
FEATURE [App::DocumentObjectGroupPython] G4_Dy  # scripted group (container) (typed FeaturePython)
  Dunit = g/cm3
  Dvalue = 8.55
  Group = -> [Dy_element001]
  conduct = 2
  density = 1
  expand = 3
  formula = Dy
  name = G4_Dy
  specific = 4
FEATURE [App::DocumentObjectGroupPython] Ho_element001  label="Ho_element : 1"  # scripted group (container) (typed FeaturePython)
  n = 1
  ref = Ho_element
FEATURE [App::DocumentObjectGroupPython] G4_Ho  # scripted group (container) (typed FeaturePython)
  Dunit = g/cm3
  Dvalue = 8.795
  Group = -> [Ho_element001]
  conduct = 2
  density = 1
  expand = 3
  formula = Ho
  name = G4_Ho
  specific = 4
FEATURE [App::DocumentObjectGroupPython] Er_element001  label="Er_element : 1"  # scripted group (container) (typed FeaturePython)
  n = 1
  ref = Er_element
FEATURE [App::DocumentObjectGroupPython] G4_Er  # scripted group (container) (typed FeaturePython)
  Dunit = g/cm3
  Dvalue = 9.066
  Group = -> [Er_element001]
  conduct = 2
  density = 1
  expand = 3
  formula = Er
  name = G4_Er
  specific = 4
FEATURE [App::DocumentObjectGroupPython] Tm_element001  label="Tm_element : 1"  # scripted group (container) (typed FeaturePython)
  n = 1
  ref = Tm_element
FEATURE [App::DocumentObjectGroupPython] G4_Tm  # scripted group (container) (typed FeaturePython)
  Dunit = g/cm3
  Dvalue = 9.321
  Group = -> [Tm_element001]
  conduct = 2
  density = 1
  expand = 3
  formula = Tm
  name = G4_Tm
  specific = 4
FEATURE [App::DocumentObjectGroupPython] Yb_element001  label="Yb_element : 1"  # scripted group (container) (typed FeaturePython)
  n = 1
  ref = Yb_element
FEATURE [App::DocumentObjectGroupPython] G4_Yb  # scripted group (container) (typed FeaturePython)
  Dunit = g/cm3
  Dvalue = 6.73
  Group = -> [Yb_element001]
  conduct = 2
  density = 1
  expand = 3
  formula = Yb
  name = G4_Yb
  specific = 4
FEATURE [App::DocumentObjectGroupPython] Lu_element001  label="Lu_element : 1"  # scripted group (container) (typed FeaturePython)
  n = 1
  ref = Lu_element
FEATURE [App::DocumentObjectGroupPython] G4_Lu  # scripted group (container) (typed FeaturePython)
  Dunit = g/cm3
  Dvalue = 9.84
  Group = -> [Lu_element001]
  conduct = 2
  density = 1
  expand = 3
  formula = Lu
  name = G4_Lu
  specific = 4
FEATURE [App::DocumentObjectGroupPython] Hf_element001  label="Hf_element : 1"  # scripted group (container) (typed FeaturePython)
  n = 1
  ref = Hf_element
FEATURE [App::DocumentObjectGroupPython] G4_Hf  # scripted group (container) (typed FeaturePython)
  Dunit = g/cm3
  Dvalue = 13.31
  Group = -> [Hf_element001]
  conduct = 2
  density = 1
  expand = 3
  formula = Hf
  name = G4_Hf
  specific = 4
FEATURE [App::DocumentObjectGroupPython] Ta_element001  label="Ta_element : 1"  # scripted group (container) (typed FeaturePython)
  n = 1
  ref = Ta_element
FEATURE [App::DocumentObjectGroupPython] G4_Ta  # scripted group (container) (typed FeaturePython)
  Dunit = g/cm3
  Dvalue = 16.654
  Group = -> [Ta_element001]
  conduct = 2
  density = 1
  expand = 3
  formula = Ta
  name = G4_Ta
  specific = 4
FEATURE [App::DocumentObjectGroupPython] W_element004  label="W_element : 004"  # scripted group (container) (typed FeaturePython)
  n = 1
  ref = W_element
FEATURE [App::DocumentObjectGroupPython] G4_W  # scripted group (container) (typed FeaturePython)
  Dunit = g/cm3
  Dvalue = 19.3
  Group = -> [W_element004]
  conduct = 2
  density = 1
  expand = 3
  formula = W
  name = G4_W
  specific = 4
FEATURE [App::DocumentObjectGroupPython] Re_element001  label="Re_element : 1"  # scripted group (container) (typed FeaturePython)
  n = 1
  ref = Re_element
FEATURE [App::DocumentObjectGroupPython] G4_Re  # scripted group (container) (typed FeaturePython)
  Dunit = g/cm3
  Dvalue = 21.02
  Group = -> [Re_element001]
  conduct = 2
  density = 1
  expand = 3
  formula = Re
  name = G4_Re
  specific = 4
FEATURE [App::DocumentObjectGroupPython] Os_element001  label="Os_element : 1"  # scripted group (container) (typed FeaturePython)
  n = 1
  ref = Os_element
FEATURE [App::DocumentObjectGroupPython] G4_Os  # scripted group (container) (typed FeaturePython)
  Dunit = g/cm3
  Dvalue = 22.57
  Group = -> [Os_element001]
  conduct = 2
  density = 1
  expand = 3
  formula = Os
  name = G4_Os
  specific = 4
FEATURE [App::DocumentObjectGroupPython] Ir_element001  label="Ir_element : 1"  # scripted group (container) (typed FeaturePython)
  n = 1
  ref = Ir_element
FEATURE [App::DocumentObjectGroupPython] G4_Ir  # scripted group (container) (typed FeaturePython)
  Dunit = g/cm3
  Dvalue = 22.42
  Group = -> [Ir_element001]
  conduct = 2
  density = 1
  expand = 3
  formula = Ir
  name = G4_Ir
  specific = 4
FEATURE [App::DocumentObjectGroupPython] Pt_element001  label="Pt_element : 1"  # scripted group (container) (typed FeaturePython)
  n = 1
  ref = Pt_element
FEATURE [App::DocumentObjectGroupPython] G4_Pt  # scripted group (container) (typed FeaturePython)
  Dunit = g/cm3
  Dvalue = 21.45
  Group = -> [Pt_element001]
  conduct = 2
  density = 1
  expand = 3
  formula = Pt
  name = G4_Pt
  specific = 4
FEATURE [App::DocumentObjectGroupPython] Au_element001  label="Au_element : 1"  # scripted group (container) (typed FeaturePython)
  n = 1
  ref = Au_element
FEATURE [App::DocumentObjectGroupPython] G4_Au  # scripted group (container) (typed FeaturePython)
  Dunit = g/cm3
  Dvalue = 19.32
  Group = -> [Au_element001]
  conduct = 2
  density = 1
  expand = 3
  formula = Au
  name = G4_Au
  specific = 4
FEATURE [App::DocumentObjectGroupPython] Hg_element002  label="Hg_element : 002"  # scripted group (container) (typed FeaturePython)
  n = 1
  ref = Hg_element
FEATURE [App::DocumentObjectGroupPython] G4_Hg  # scripted group (container) (typed FeaturePython)
  Dunit = g/cm3
  Dvalue = 13.546
  Group = -> [Hg_element002]
  conduct = 2
  density = 1
  expand = 3
  formula = Hg
  name = G4_Hg
  specific = 4
FEATURE [App::DocumentObjectGroupPython] Tl_element002  label="Tl_element : 002"  # scripted group (container) (typed FeaturePython)
  n = 1
  ref = Tl_element
FEATURE [App::DocumentObjectGroupPython] G4_Tl  # scripted group (container) (typed FeaturePython)
  Dunit = g/cm3
  Dvalue = 11.72
  Group = -> [Tl_element002]
  conduct = 2
  density = 1
  expand = 3
  formula = Tl
  name = G4_Tl
  specific = 4
FEATURE [App::DocumentObjectGroupPython] Pb_element003  label="Pb_element : 1"  # scripted group (container) (typed FeaturePython)
  n = 1
  ref = Pb_element
FEATURE [App::DocumentObjectGroupPython] G4_Pb  # scripted group (container) (typed FeaturePython)
  Dunit = g/cm3
  Dvalue = 11.35
  Group = -> [Pb_element003]
  conduct = 2
  density = 1
  expand = 3
  formula = Pb
  name = G4_Pb
  specific = 4
FEATURE [App::DocumentObjectGroupPython] Bi_element002  label="Bi_element : 1"  # scripted group (container) (typed FeaturePython)
  n = 1
  ref = Bi_element
FEATURE [App::DocumentObjectGroupPython] G4_Bi  # scripted group (container) (typed FeaturePython)
  Dunit = g/cm3
  Dvalue = 9.747
  Group = -> [Bi_element002]
  conduct = 2
  density = 1
  expand = 3
  formula = Bi
  name = G4_Bi
  specific = 4
FEATURE [App::DocumentObjectGroupPython] Po_element001  label="Po_element : 1"  # scripted group (container) (typed FeaturePython)
  n = 1
  ref = Po_element
FEATURE [App::DocumentObjectGroupPython] G4_Po  # scripted group (container) (typed FeaturePython)
  Dunit = g/cm3
  Dvalue = 9.32
  Group = -> [Po_element001]
  conduct = 2
  density = 1
  expand = 3
  formula = Po
  name = G4_Po
  specific = 4
FEATURE [App::DocumentObjectGroupPython] At_element001  label="At_element : 1"  # scripted group (container) (typed FeaturePython)
  n = 1
  ref = At_element
FEATURE [App::DocumentObjectGroupPython] G4_At  # scripted group (container) (typed FeaturePython)
  Dunit = g/cm3
  Dvalue = 9.32
  Group = -> [At_element001]
  conduct = 2
  density = 1
  expand = 3
  formula = At
  name = G4_At
  specific = 4
FEATURE [App::DocumentObjectGroupPython] Rn_element001  label="Rn_element : 1"  # scripted group (container) (typed FeaturePython)
  n = 1
  ref = Rn_element
FEATURE [App::DocumentObjectGroupPython] G4_Rn  # scripted group (container) (typed FeaturePython)
  Dunit = g/cm3
  Dvalue = 0.00900662
  Group = -> [Rn_element001]
  conduct = 2
  density = 1
  expand = 3
  formula = Rn
  name = G4_Rn
  specific = 4
FEATURE [App::DocumentObjectGroupPython] Fr_element001  label="Fr_element : 1"  # scripted group (container) (typed FeaturePython)
  n = 1
  ref = Fr_element
FEATURE [App::DocumentObjectGroupPython] G4_Fr  # scripted group (container) (typed FeaturePython)
  Dunit = g/cm3
  Dvalue = 1
  Group = -> [Fr_element001]
  conduct = 2
  density = 1
  expand = 3
  formula = Fr
  name = G4_Fr
  specific = 4
FEATURE [App::DocumentObjectGroupPython] Ra_element001  label="Ra_element : 1"  # scripted group (container) (typed FeaturePython)
  n = 1
  ref = Ra_element
FEATURE [App::DocumentObjectGroupPython] G4_Ra  # scripted group (container) (typed FeaturePython)
  Dunit = g/cm3
  Dvalue = 5
  Group = -> [Ra_element001]
  conduct = 2
  density = 1
  expand = 3
  formula = Ra
  name = G4_Ra
  specific = 4
FEATURE [App::DocumentObjectGroupPython] Ac_element001  label="Ac_element : 1"  # scripted group (container) (typed FeaturePython)
  n = 1
  ref = Ac_element
FEATURE [App::DocumentObjectGroupPython] G4_Ac  # scripted group (container) (typed FeaturePython)
  Dunit = g/cm3
  Dvalue = 10.07
  Group = -> [Ac_element001]
  conduct = 2
  density = 1
  expand = 3
  formula = Ac
  name = G4_Ac
  specific = 4
FEATURE [App::DocumentObjectGroupPython] Th_element001  label="Th_element : 1"  # scripted group (container) (typed FeaturePython)
  n = 1
  ref = Th_element
FEATURE [App::DocumentObjectGroupPython] G4_Th  # scripted group (container) (typed FeaturePython)
  Dunit = g/cm3
  Dvalue = 11.72
  Group = -> [Th_element001]
  conduct = 2
  density = 1
  expand = 3
  formula = Th
  name = G4_Th
  specific = 4
FEATURE [App::DocumentObjectGroupPython] Pa_element001  label="Pa_element : 1"  # scripted group (container) (typed FeaturePython)
  n = 1
  ref = Pa_element
FEATURE [App::DocumentObjectGroupPython] G4_Pa  # scripted group (container) (typed FeaturePython)
  Dunit = g/cm3
  Dvalue = 15.37
  Group = -> [Pa_element001]
  conduct = 2
  density = 1
  expand = 3
  formula = Pa
  name = G4_Pa
  specific = 4
FEATURE [App::DocumentObjectGroupPython] U_element004  label="U_element : 004"  # scripted group (container) (typed FeaturePython)
  n = 1
  ref = U_element
FEATURE [App::DocumentObjectGroupPython] G4_U  # scripted group (container) (typed FeaturePython)
  Dunit = g/cm3
  Dvalue = 18.95
  Group = -> [U_element004]
  conduct = 2
  density = 1
  expand = 3
  formula = U
  name = G4_U
  specific = 4
FEATURE [App::DocumentObjectGroupPython] Np_element001  label="Np_element : 1"  # scripted group (container) (typed FeaturePython)
  n = 1
  ref = Np_element
FEATURE [App::DocumentObjectGroupPython] G4_Np  # scripted group (container) (typed FeaturePython)
  Dunit = g/cm3
  Dvalue = 20.25
  Group = -> [Np_element001]
  conduct = 2
  density = 1
  expand = 3
  formula = Np
  name = G4_Np
  specific = 4
FEATURE [App::DocumentObjectGroupPython] Pu_element002  label="Pu_element : 002"  # scripted group (container) (typed FeaturePython)
  n = 1
  ref = Pu_element
FEATURE [App::DocumentObjectGroupPython] G4_Pu  # scripted group (container) (typed FeaturePython)
  Dunit = g/cm3
  Dvalue = 19.84
  Group = -> [Pu_element002]
  conduct = 2
  density = 1
  expand = 3
  formula = Pu
  name = G4_Pu
  specific = 4
FEATURE [App::DocumentObjectGroupPython] Am_element001  label="Am_element : 1"  # scripted group (container) (typed FeaturePython)
  n = 1
  ref = Am_element
FEATURE [App::DocumentObjectGroupPython] G4_Am  # scripted group (container) (typed FeaturePython)
  Dunit = g/cm3
  Dvalue = 13.67
  Group = -> [Am_element001]
  conduct = 2
  density = 1
  expand = 3
  formula = Am
  name = G4_Am
  specific = 4
FEATURE [App::DocumentObjectGroupPython] Cm_element001  label="Cm_element : 1"  # scripted group (container) (typed FeaturePython)
  n = 1
  ref = Cm_element
FEATURE [App::DocumentObjectGroupPython] G4_Cm  # scripted group (container) (typed FeaturePython)
  Dunit = g/cm3
  Dvalue = 13.51
  Group = -> [Cm_element001]
  conduct = 2
  density = 1
  expand = 3
  formula = Cm
  name = G4_Cm
  specific = 4
FEATURE [App::DocumentObjectGroupPython] Bk_element001  label="Bk_element : 1"  # scripted group (container) (typed FeaturePython)
  n = 1
  ref = Bk_element
FEATURE [App::DocumentObjectGroupPython] G4_Bk  # scripted group (container) (typed FeaturePython)
  Dunit = g/cm3
  Dvalue = 14
  Group = -> [Bk_element001]
  conduct = 2
  density = 1
  expand = 3
  formula = Bk
  name = G4_Bk
  specific = 4
FEATURE [App::DocumentObjectGroupPython] Cf_element001  label="Cf_element : 1"  # scripted group (container) (typed FeaturePython)
  n = 1
  ref = Cf_element
FEATURE [App::DocumentObjectGroupPython] G4_Cf  # scripted group (container) (typed FeaturePython)
  Dunit = g/cm3
  Dvalue = 10
  Group = -> [Cf_element001]
  conduct = 2
  density = 1
  expand = 3
  formula = Cf
  name = G4_Cf
  specific = 4
FEATURE [App::DocumentObjectGroupPython] Element  # scripted group (container) (typed FeaturePython)
  Group = -> [G4_H,G4_He,G4_Li,G4_Be,G4_B,G4_C,G4_N,G4_O,G4_F,G4_Ne,G4_Na,G4_Mg,G4_Al,G4_Si,G4_P,G4_S,G4_Cl,G4_Ar,G4_K,G4_Ca,G4_Sc,G4_Ti,G4_V,G4_Cr,G4_Mn,G4_Fe,G4_Co,G4_Ni,G4_Cu,G4_Zn,G4_Ga,G4_Ge,G4_As,G4_Se,G4_Br,G4_Kr,G4_Rb,G4_Sr,G4_Y,G4_Zr,G4_Nb,G4_Mo,G4_Tc,G4_Ru,G4_Rh,G4_Pd,G4_Ag,G4_Cd,G4_In,G4_Sn,G4_Sb,G4_Te,G4_I,G4_Xe,G4_Cs,G4_Ba,G4_La,G4_Ce,G4_Pr,G4_Nd,G4_Pm,G4_Sm,G4_Eu,G4_Gd,G4_Tb,G4_Dy,G4_Ho,G4_Er,+30 more]
FEATURE [App::DocumentObjectGroupPython] H_element114  label="H_element : 063"  # scripted group (container) (typed FeaturePython)
  n = 2
  ref = H_element
FEATURE [App::DocumentObjectGroupPython] G4_lH2  # scripted group (container) (typed FeaturePython)
  Dunit = g/cm3
  Dvalue = 0.0708
  Group = -> [H_element114]
  conduct = 2
  density = 1
  expand = 3
  formula = G4_lH2
  name = G4_lH2
  specific = 4
FEATURE [App::DocumentObjectGroupPython] N_element049  label="N_element : 022"  # scripted group (container) (typed FeaturePython)
  n = 2
  ref = N_element
FEATURE [App::DocumentObjectGroupPython] G4_lN2  # scripted group (container) (typed FeaturePython)
  Dunit = g/cm3
  Dvalue = 0.807
  Group = -> [N_element049]
  conduct = 2
  density = 1
  expand = 3
  formula = G4_lN2
  name = G4_lN2
  specific = 4
FEATURE [App::DocumentObjectGroupPython] O_element106  label="O_element : 060"  # scripted group (container) (typed FeaturePython)
  n = 2
  ref = O_element
FEATURE [App::DocumentObjectGroupPython] G4_lO2  # scripted group (container) (typed FeaturePython)
  Dunit = g/cm3
  Dvalue = 1.141
  Group = -> [O_element106]
  conduct = 2
  density = 1
  expand = 3
  formula = G4_lO2
  name = G4_lO2
  specific = 4
FEATURE [App::DocumentObjectGroupPython] Ar  label="Ar : 1"  # scripted group (container) (typed FeaturePython)
  n = 1
  ref = Ar
FEATURE [App::DocumentObjectGroupPython] G4_lAr  # scripted group (container) (typed FeaturePython)
  Dunit = g/cm3
  Dvalue = 1.396
  Group = -> [Ar]
  conduct = 2
  density = 1
  expand = 3
  formula = G4_lAr
  name = G4_lAr
  specific = 4
FEATURE [App::DocumentObjectGroupPython] Br  label="Br : 1"  # scripted group (container) (typed FeaturePython)
  n = 1
  ref = Br
FEATURE [App::DocumentObjectGroupPython] G4_lBr  # scripted group (container) (typed FeaturePython)
  Dunit = g/cm3
  Dvalue = 3.1028
  Group = -> [Br]
  conduct = 2
  density = 1
  expand = 3
  formula = G4_lBr
  name = G4_lBr
  specific = 4
FEATURE [App::DocumentObjectGroupPython] Kr  label="Kr : 1"  # scripted group (container) (typed FeaturePython)
  n = 1
  ref = Kr
FEATURE [App::DocumentObjectGroupPython] G4_lKr  # scripted group (container) (typed FeaturePython)
  Dunit = g/cm3
  Dvalue = 2.418
  Group = -> [Kr]
  conduct = 2
  density = 1
  expand = 3
  formula = G4_lKr
  name = G4_lKr
  specific = 4
FEATURE [App::DocumentObjectGroupPython] Xe  label="Xe : 1"  # scripted group (container) (typed FeaturePython)
  n = 1
  ref = Xe
FEATURE [App::DocumentObjectGroupPython] G4_lXe  # scripted group (container) (typed FeaturePython)
  Dunit = g/cm3
  Dvalue = 2.953
  Group = -> [Xe]
  conduct = 2
  density = 1
  expand = 3
  formula = G4_lXe
  name = G4_lXe
  specific = 4
FEATURE [App::DocumentObjectGroupPython] O_element107  label="O_element : 061"  # scripted group (container) (typed FeaturePython)
  n = 4
  ref = O_element
FEATURE [App::DocumentObjectGroupPython] Pb_element004  label="Pb_element : 002"  # scripted group (container) (typed FeaturePython)
  n = 1
  ref = Pb_element
FEATURE [App::DocumentObjectGroupPython] W_element005  label="W_element : 005"  # scripted group (container) (typed FeaturePython)
  n = 1
  ref = W_element
FEATURE [App::DocumentObjectGroupPython] G4_PbWO4  # scripted group (container) (typed FeaturePython)
  Dunit = g/cm3
  Dvalue = 8.28
  Group = -> [O_element107,Pb_element004,W_element005]
  conduct = 2
  density = 1
  expand = 3
  formula = G4_PbWO4
  name = G4_PbWO4
  specific = 4
FEATURE [App::DocumentObjectGroupPython] alactic  label="alactic : 1"  # scripted group (container) (typed FeaturePython)
  n = 1
  ref = alactic
FEATURE [App::DocumentObjectGroupPython] G4_Galactic  # scripted group (container) (typed FeaturePython)
  Dunit = g/cm3
  Dvalue = 0
  Group = -> [alactic]
  conduct = 2
  density = 1
  expand = 3
  formula = G4_Galactic
  name = G4_Galactic
  specific = 4
FEATURE [App::DocumentObjectGroupPython] RAPHITE_POROUS  label="RAPHITE_POROUS : 1"  # scripted group (container) (typed FeaturePython)
  n = 1
  ref = RAPHITE_POROUS
FEATURE [App::DocumentObjectGroupPython] G4_GRAPHITE_POROUS  # scripted group (container) (typed FeaturePython)
  Dunit = g/cm3
  Dvalue = 1.7
  Group = -> [RAPHITE_POROUS]
  conduct = 2
  density = 1
  expand = 3
  formula = G4_GRAPHITE_POROUS
  name = G4_GRAPHITE_POROUS
  specific = 4
FEATURE [App::DocumentObjectGroupPython] H_element115  label="H_element : 0.150"  # scripted group (container) (typed FeaturePython)
  n = 0.080538
FEATURE [App::DocumentObjectGroupPython] C_element125  label="C_element : 0.600"  # scripted group (container) (typed FeaturePython)
  n = 0.599848
FEATURE [App::DocumentObjectGroupPython] O_element108  label="O_element : 0.320"  # scripted group (container) (typed FeaturePython)
  n = 0.319614
FEATURE [App::DocumentObjectGroupPython] G4_LUCITE  # scripted group (container) (typed FeaturePython)
  Dunit = g/cm3
  Dvalue = 1.19
  Group = -> [H_element115,C_element125,O_element108]
  conduct = 2
  density = 1
  expand = 3
  formula = G4_LUCITE
  name = G4_LUCITE
  specific = 4
FEATURE [App::DocumentObjectGroupPython] Cu_element002  label="Cu_element : 62"  # scripted group (container) (typed FeaturePython)
  n = 62
  ref = Cu_element
FEATURE [App::DocumentObjectGroupPython] Zn_element002  label="Zn_element : 35"  # scripted group (container) (typed FeaturePython)
  n = 35
  ref = Zn_element
FEATURE [App::DocumentObjectGroupPython] Pb_element005  label="Pb_element : 3"  # scripted group (container) (typed FeaturePython)
  n = 3
  ref = Pb_element
FEATURE [App::DocumentObjectGroupPython] G4_BRASS  # scripted group (container) (typed FeaturePython)
  Dunit = g/cm3
  Dvalue = 8.52
  Group = -> [Cu_element002,Zn_element002,Pb_element005]
  conduct = 2
  density = 1
  expand = 3
  formula = G4_BRASS
  name = G4_BRASS
  specific = 4
FEATURE [App::DocumentObjectGroupPython] Cu_element003  label="Cu_element : 89"  # scripted group (container) (typed FeaturePython)
  n = 89
  ref = Cu_element
FEATURE [App::DocumentObjectGroupPython] Zn_element003  label="Zn_element : 9"  # scripted group (container) (typed FeaturePython)
  n = 9
  ref = Zn_element
FEATURE [App::DocumentObjectGroupPython] Pb_element006  label="Pb_element : 2"  # scripted group (container) (typed FeaturePython)
  n = 2
  ref = Pb_element
FEATURE [App::DocumentObjectGroupPython] G4_BRONZE  # scripted group (container) (typed FeaturePython)
  Dunit = g/cm3
  Dvalue = 8.82
  Group = -> [Cu_element003,Zn_element003,Pb_element006]
  conduct = 2
  density = 1
  expand = 3
  formula = G4_BRONZE
  name = G4_BRONZE
  specific = 4
FEATURE [App::DocumentObjectGroupPython] Fe_element008  label="Fe_element : 74"  # scripted group (container) (typed FeaturePython)
  n = 74
  ref = Fe_element
FEATURE [App::DocumentObjectGroupPython] Cr_element002  label="Cr_element : 18"  # scripted group (container) (typed FeaturePython)
  n = 18
  ref = Cr_element
FEATURE [App::DocumentObjectGroupPython] Ni_element002  label="Ni_element : 8"  # scripted group (container) (typed FeaturePython)
  n = 8
  ref = Ni_element
FEATURE [App::DocumentObjectGroupPython] G4_STAINLESS_STEEL  label="G4_STAINLESS-STEEL"  # scripted group (container) (typed FeaturePython)
  Dunit = g/cm3
  Dvalue = 8
  Group = -> [Fe_element008,Cr_element002,Ni_element002]
  conduct = 2
  density = 1
  expand = 3
  formula = G4_STAINLESS-STEEL
  name = G4_STAINLESS-STEEL
  specific = 4
FEATURE [App::DocumentObjectGroupPython] H_element116  label="H_element : 064"  # scripted group (container) (typed FeaturePython)
  n = 18
  ref = H_element
FEATURE [App::DocumentObjectGroupPython] C_element126  label="C_element : 071"  # scripted group (container) (typed FeaturePython)
  n = 12
  ref = C_element
FEATURE [App::DocumentObjectGroupPython] O_element109  label="O_element : 062"  # scripted group (container) (typed FeaturePython)
  n = 7
  ref = O_element
FEATURE [App::DocumentObjectGroupPython] G4_CR39  # scripted group (container) (typed FeaturePython)
  Dunit = g/cm3
  Dvalue = 1.32
  Group = -> [H_element116,C_element126,O_element109]
  conduct = 2
  density = 1
  expand = 3
  formula = G4_CR39
  name = G4_CR39
  specific = 4
FEATURE [App::DocumentObjectGroupPython] H_element117  label="H_element : 38"  # scripted group (container) (typed FeaturePython)
  n = 38
  ref = H_element
FEATURE [App::DocumentObjectGroupPython] C_element127  label="C_element : 072"  # scripted group (container) (typed FeaturePython)
  n = 18
  ref = C_element
FEATURE [App::DocumentObjectGroupPython] O_element110  label="O_element : 063"  # scripted group (container) (typed FeaturePython)
  n = 1
  ref = O_element
FEATURE [App::DocumentObjectGroupPython] G4_OCTADECANOL  # scripted group (container) (typed FeaturePython)
  Dunit = g/cm3
  Dvalue = 0.812
  Group = -> [H_element117,C_element127,O_element110]
  conduct = 2
  density = 1
  expand = 3
  formula = G4_OCTADECANOL
  name = G4_OCTADECANOL
  specific = 4
FEATURE [App::DocumentObjectGroupPython] HEP  # scripted group (container) (typed FeaturePython)
  Group = -> [G4_lH2,G4_lN2,G4_lO2,G4_lAr,G4_lBr,G4_lKr,G4_lXe,G4_PbWO4,G4_Galactic,G4_GRAPHITE_POROUS,G4_LUCITE,G4_BRASS,G4_BRONZE,G4_STAINLESS_STEEL,G4_CR39,G4_OCTADECANOL]
FEATURE [App::DocumentObjectGroupPython] C_element128  label="C_element : 073"  # scripted group (container) (typed FeaturePython)
  n = 14
  ref = C_element
FEATURE [App::DocumentObjectGroupPython] H_element118  label="H_element : 065"  # scripted group (container) (typed FeaturePython)
  n = 10
  ref = H_element
FEATURE [App::DocumentObjectGroupPython] O_element111  label="O_element : 064"  # scripted group (container) (typed FeaturePython)
  n = 2
  ref = O_element
FEATURE [App::DocumentObjectGroupPython] N_element050  label="N_element : 023"  # scripted group (container) (typed FeaturePython)
  n = 2
  ref = N_element
FEATURE [App::DocumentObjectGroupPython] G4_KEVLAR  # scripted group (container) (typed FeaturePython)
  Dunit = g/cm3
  Dvalue = 1.44
  Group = -> [C_element128,H_element118,O_element111,N_element050]
  conduct = 2
  density = 1
  expand = 3
  formula = G4_KEVLAR
  name = G4_KEVLAR
  specific = 4
FEATURE [App::DocumentObjectGroupPython] C_element129  label="C_element : 074"  # scripted group (container) (typed FeaturePython)
  n = 10
  ref = C_element
FEATURE [App::DocumentObjectGroupPython] H_element119  label="H_element : 066"  # scripted group (container) (typed FeaturePython)
  n = 8
  ref = H_element
FEATURE [App::DocumentObjectGroupPython] O_element112  label="O_element : 065"  # scripted group (container) (typed FeaturePython)
  n = 4
  ref = O_element
FEATURE [App::DocumentObjectGroupPython] G4_DACRON  # scripted group (container) (typed FeaturePython)
  Dunit = g/cm3
  Dvalue = 1.4
  Group = -> [C_element129,H_element119,O_element112]
  conduct = 2
  density = 1
  expand = 3
  formula = G4_DACRON
  name = G4_DACRON
  specific = 4
FEATURE [App::DocumentObjectGroupPython] C_element130  label="C_element : 075"  # scripted group (container) (typed FeaturePython)
  n = 4
  ref = C_element
FEATURE [App::DocumentObjectGroupPython] H_element120  label="H_element : 067"  # scripted group (container) (typed FeaturePython)
  n = 5
  ref = H_element
FEATURE [App::DocumentObjectGroupPython] Cl_element030  label="Cl_element : 016"  # scripted group (container) (typed FeaturePython)
  n = 1
  ref = Cl_element
FEATURE [App::DocumentObjectGroupPython] G4_NEOPRENE  # scripted group (container) (typed FeaturePython)
  Dunit = g/cm3
  Dvalue = 1.23
  Group = -> [C_element130,H_element120,Cl_element030]
  conduct = 2
  density = 1
  expand = 3
  formula = G4_NEOPRENE
  name = G4_NEOPRENE
  specific = 4
FEATURE [App::DocumentObjectGroupPython] Space  # scripted group (container) (typed FeaturePython)
  Group = -> [G4_KEVLAR,G4_DACRON,G4_NEOPRENE]
FEATURE [App::DocumentObjectGroupPython] H_element121  label="H_element : 068"  # scripted group (container) (typed FeaturePython)
  n = 5
  ref = H_element
FEATURE [App::DocumentObjectGroupPython] C_element131  label="C_element : 076"  # scripted group (container) (typed FeaturePython)
  n = 4
  ref = C_element
FEATURE [App::DocumentObjectGroupPython] N_element051  label="N_element : 3"  # scripted group (container) (typed FeaturePython)
  n = 3
  ref = N_element
FEATURE [App::DocumentObjectGroupPython] O_element113  label="O_element : 066"  # scripted group (container) (typed FeaturePython)
  n = 1
  ref = O_element
FEATURE [App::DocumentObjectGroupPython] G4_CYTOSINE  # scripted group (container) (typed FeaturePython)
  Dunit = g/cm3
  Dvalue = 1.55
  Group = -> [H_element121,C_element131,N_element051,O_element113]
  conduct = 2
  density = 1
  expand = 3
  formula = G4_CYTOSINE
  name = G4_CYTOSINE
  specific = 4
FEATURE [App::DocumentObjectGroupPython] H_element122  label="H_element : 069"  # scripted group (container) (typed FeaturePython)
  n = 6
  ref = H_element
FEATURE [App::DocumentObjectGroupPython] C_element132  label="C_element : 077"  # scripted group (container) (typed FeaturePython)
  n = 5
  ref = C_element
FEATURE [App::DocumentObjectGroupPython] N_element052  label="N_element : 024"  # scripted group (container) (typed FeaturePython)
  n = 2
  ref = N_element
FEATURE [App::DocumentObjectGroupPython] O_element114  label="O_element : 067"  # scripted group (container) (typed FeaturePython)
  n = 2
  ref = O_element
FEATURE [App::DocumentObjectGroupPython] G4_THYMINE  # scripted group (container) (typed FeaturePython)
  Dunit = g/cm3
  Dvalue = 1.23
  Group = -> [H_element122,C_element132,N_element052,O_element114]
  conduct = 2
  density = 1
  expand = 3
  formula = G4_THYMINE
  name = G4_THYMINE
  specific = 4
FEATURE [App::DocumentObjectGroupPython] H_element123  label="H_element : 070"  # scripted group (container) (typed FeaturePython)
  n = 4
  ref = H_element
FEATURE [App::DocumentObjectGroupPython] C_element133  label="C_element : 078"  # scripted group (container) (typed FeaturePython)
  n = 4
  ref = C_element
FEATURE [App::DocumentObjectGroupPython] N_element053  label="N_element : 025"  # scripted group (container) (typed FeaturePython)
  n = 2
  ref = N_element
FEATURE [App::DocumentObjectGroupPython] O_element115  label="O_element : 068"  # scripted group (container) (typed FeaturePython)
  n = 2
  ref = O_element
FEATURE [App::DocumentObjectGroupPython] G4_URACIL  # scripted group (container) (typed FeaturePython)
  Dunit = g/cm3
  Dvalue = 1.32
  Group = -> [H_element123,C_element133,N_element053,O_element115]
  conduct = 2
  density = 1
  expand = 3
  formula = G4_URACIL
  name = G4_URACIL
  specific = 4
FEATURE [App::DocumentObjectGroupPython] H_element124  label="H_element : 071"  # scripted group (container) (typed FeaturePython)
  n = 4
  ref = H_element
FEATURE [App::DocumentObjectGroupPython] C_element134  label="C_element : 079"  # scripted group (container) (typed FeaturePython)
  n = 5
  ref = C_element
FEATURE [App::DocumentObjectGroupPython] N_element054  label="N_element : 026"  # scripted group (container) (typed FeaturePython)
  n = 5
  ref = N_element
FEATURE [App::DocumentObjectGroupPython] G4_DNA_ADENINE  # scripted group (container) (typed FeaturePython)
  Dunit = g/cm3
  Dvalue = 1
  Group = -> [H_element124,C_element134,N_element054]
  conduct = 2
  density = 1
  expand = 3
  formula = G4_DNA_ADENINE
  name = G4_DNA_ADENINE
  specific = 4
FEATURE [App::DocumentObjectGroupPython] H_element125  label="H_element : 072"  # scripted group (container) (typed FeaturePython)
  n = 4
  ref = H_element
FEATURE [App::DocumentObjectGroupPython] C_element135  label="C_element : 080"  # scripted group (container) (typed FeaturePython)
  n = 5
  ref = C_element
FEATURE [App::DocumentObjectGroupPython] N_element055  label="N_element : 027"  # scripted group (container) (typed FeaturePython)
  n = 5
  ref = N_element
FEATURE [App::DocumentObjectGroupPython] O_element116  label="O_element : 069"  # scripted group (container) (typed FeaturePython)
  n = 1
  ref = O_element
FEATURE [App::DocumentObjectGroupPython] G4_DNA_GUANINE  # scripted group (container) (typed FeaturePython)
  Dunit = g/cm3
  Dvalue = 1
  Group = -> [H_element125,C_element135,N_element055,O_element116]
  conduct = 2
  density = 1
  expand = 3
  formula = G4_DNA_GUANINE
  name = G4_DNA_GUANINE
  specific = 4
FEATURE [App::DocumentObjectGroupPython] H_element126  label="H_element : 073"  # scripted group (container) (typed FeaturePython)
  n = 4
  ref = H_element
FEATURE [App::DocumentObjectGroupPython] C_element136  label="C_element : 081"  # scripted group (container) (typed FeaturePython)
  n = 4
  ref = C_element
FEATURE [App::DocumentObjectGroupPython] N_element056  label="N_element : 028"  # scripted group (container) (typed FeaturePython)
  n = 3
  ref = N_element
FEATURE [App::DocumentObjectGroupPython] O_element117  label="O_element : 070"  # scripted group (container) (typed FeaturePython)
  n = 1
  ref = O_element
FEATURE [App::DocumentObjectGroupPython] G4_DNA_CYTOSINE  # scripted group (container) (typed FeaturePython)
  Dunit = g/cm3
  Dvalue = 1
  Group = -> [H_element126,C_element136,N_element056,O_element117]
  conduct = 2
  density = 1
  expand = 3
  formula = G4_DNA_CYTOSINE
  name = G4_DNA_CYTOSINE
  specific = 4
FEATURE [App::DocumentObjectGroupPython] H_element127  label="H_element : 074"  # scripted group (container) (typed FeaturePython)
  n = 5
  ref = H_element
FEATURE [App::DocumentObjectGroupPython] C_element137  label="C_element : 082"  # scripted group (container) (typed FeaturePython)
  n = 5
  ref = C_element
FEATURE [App::DocumentObjectGroupPython] N_element057  label="N_element : 029"  # scripted group (container) (typed FeaturePython)
  n = 2
  ref = N_element
FEATURE [App::DocumentObjectGroupPython] O_element118  label="O_element : 071"  # scripted group (container) (typed FeaturePython)
  n = 2
  ref = O_element
FEATURE [App::DocumentObjectGroupPython] G4_DNA_THYMINE  # scripted group (container) (typed FeaturePython)
  Dunit = g/cm3
  Dvalue = 1
  Group = -> [H_element127,C_element137,N_element057,O_element118]
  conduct = 2
  density = 1
  expand = 3
  formula = G4_DNA_THYMINE
  name = G4_DNA_THYMINE
  specific = 4
FEATURE [App::DocumentObjectGroupPython] H_element128  label="H_element : 075"  # scripted group (container) (typed FeaturePython)
  n = 3
  ref = H_element
FEATURE [App::DocumentObjectGroupPython] C_element138  label="C_element : 083"  # scripted group (container) (typed FeaturePython)
  n = 4
  ref = C_element
FEATURE [App::DocumentObjectGroupPython] N_element058  label="N_element : 030"  # scripted group (container) (typed FeaturePython)
  n = 2
  ref = N_element
FEATURE [App::DocumentObjectGroupPython] O_element119  label="O_element : 072"  # scripted group (container) (typed FeaturePython)
  n = 2
  ref = O_element
FEATURE [App::DocumentObjectGroupPython] G4_DNA_URACIL  # scripted group (container) (typed FeaturePython)
  Dunit = g/cm3
  Dvalue = 1
  Group = -> [H_element128,C_element138,N_element058,O_element119]
  conduct = 2
  density = 1
  expand = 3
  formula = G4_DNA_URACIL
  name = G4_DNA_URACIL
  specific = 4
FEATURE [App::DocumentObjectGroupPython] H_element129  label="H_element : 076"  # scripted group (container) (typed FeaturePython)
  n = 10
  ref = H_element
FEATURE [App::DocumentObjectGroupPython] C_element139  label="C_element : 084"  # scripted group (container) (typed FeaturePython)
  n = 10
  ref = C_element
FEATURE [App::DocumentObjectGroupPython] N_element059  label="N_element : 031"  # scripted group (container) (typed FeaturePython)
  n = 5
  ref = N_element
FEATURE [App::DocumentObjectGroupPython] O_element120  label="O_element : 073"  # scripted group (container) (typed FeaturePython)
  n = 4
  ref = O_element
FEATURE [App::DocumentObjectGroupPython] G4_DNA_ADENOSINE  # scripted group (container) (typed FeaturePython)
  Dunit = g/cm3
  Dvalue = 1
  Group = -> [H_element129,C_element139,N_element059,O_element120]
  conduct = 2
  density = 1
  expand = 3
  formula = G4_DNA_ADENOSINE
  name = G4_DNA_ADENOSINE
  specific = 4
FEATURE [App::DocumentObjectGroupPython] H_element130  label="H_element : 077"  # scripted group (container) (typed FeaturePython)
  n = 10
  ref = H_element
FEATURE [App::DocumentObjectGroupPython] C_element140  label="C_element : 085"  # scripted group (container) (typed FeaturePython)
  n = 10
  ref = C_element
FEATURE [App::DocumentObjectGroupPython] N_element060  label="N_element : 032"  # scripted group (container) (typed FeaturePython)
  n = 5
  ref = N_element
FEATURE [App::DocumentObjectGroupPython] O_element121  label="O_element : 074"  # scripted group (container) (typed FeaturePython)
  n = 5
  ref = O_element
FEATURE [App::DocumentObjectGroupPython] G4_DNA_GUANOSINE  # scripted group (container) (typed FeaturePython)
  Dunit = g/cm3
  Dvalue = 1
  Group = -> [H_element130,C_element140,N_element060,O_element121]
  conduct = 2
  density = 1
  expand = 3
  formula = G4_DNA_GUANOSINE
  name = G4_DNA_GUANOSINE
  specific = 4
FEATURE [App::DocumentObjectGroupPython] H_element131  label="H_element : 078"  # scripted group (container) (typed FeaturePython)
  n = 10
  ref = H_element
FEATURE [App::DocumentObjectGroupPython] C_element141  label="C_element : 086"  # scripted group (container) (typed FeaturePython)
  n = 9
  ref = C_element
FEATURE [App::DocumentObjectGroupPython] N_element061  label="N_element : 033"  # scripted group (container) (typed FeaturePython)
  n = 3
  ref = N_element
FEATURE [App::DocumentObjectGroupPython] O_element122  label="O_element : 075"  # scripted group (container) (typed FeaturePython)
  n = 5
  ref = O_element
FEATURE [App::DocumentObjectGroupPython] G4_DNA_CYTIDINE  # scripted group (container) (typed FeaturePython)
  Dunit = g/cm3
  Dvalue = 1
  Group = -> [H_element131,C_element141,N_element061,O_element122]
  conduct = 2
  density = 1
  expand = 3
  formula = G4_DNA_CYTIDINE
  name = G4_DNA_CYTIDINE
  specific = 4
FEATURE [App::DocumentObjectGroupPython] H_element132  label="H_element : 079"  # scripted group (container) (typed FeaturePython)
  n = 9
  ref = H_element
FEATURE [App::DocumentObjectGroupPython] C_element142  label="C_element : 087"  # scripted group (container) (typed FeaturePython)
  n = 9
  ref = C_element
FEATURE [App::DocumentObjectGroupPython] N_element062  label="N_element : 034"  # scripted group (container) (typed FeaturePython)
  n = 2
  ref = N_element
FEATURE [App::DocumentObjectGroupPython] O_element123  label="O_element : 076"  # scripted group (container) (typed FeaturePython)
  n = 6
  ref = O_element
FEATURE [App::DocumentObjectGroupPython] G4_DNA_URIDINE  # scripted group (container) (typed FeaturePython)
  Dunit = g/cm3
  Dvalue = 1
  Group = -> [H_element132,C_element142,N_element062,O_element123]
  conduct = 2
  density = 1
  expand = 3
  formula = G4_DNA_URIDINE
  name = G4_DNA_URIDINE
  specific = 4
FEATURE [App::DocumentObjectGroupPython] H_element133  label="H_element : 080"  # scripted group (container) (typed FeaturePython)
  n = 11
  ref = H_element
FEATURE [App::DocumentObjectGroupPython] C_element143  label="C_element : 088"  # scripted group (container) (typed FeaturePython)
  n = 10
  ref = C_element
FEATURE [App::DocumentObjectGroupPython] N_element063  label="N_element : 035"  # scripted group (container) (typed FeaturePython)
  n = 2
  ref = N_element
FEATURE [App::DocumentObjectGroupPython] O_element124  label="O_element : 077"  # scripted group (container) (typed FeaturePython)
  n = 6
  ref = O_element
FEATURE [App::DocumentObjectGroupPython] G4_DNA_METHYLURIDINE  # scripted group (container) (typed FeaturePython)
  Dunit = g/cm3
  Dvalue = 1
  Group = -> [H_element133,C_element143,N_element063,O_element124]
  conduct = 2
  density = 1
  expand = 3
  formula = G4_DNA_METHYLURIDINE
  name = G4_DNA_METHYLURIDINE
  specific = 4
FEATURE [App::DocumentObjectGroupPython] P_element014  label="P_element : 003"  # scripted group (container) (typed FeaturePython)
  n = 1
  ref = P_element
FEATURE [App::DocumentObjectGroupPython] O_element125  label="O_element : 078"  # scripted group (container) (typed FeaturePython)
  n = 3
  ref = O_element
FEATURE [App::DocumentObjectGroupPython] G4_DNA_MONOPHOSPHATE  # scripted group (container) (typed FeaturePython)
  Dunit = g/cm3
  Dvalue = 1
  Group = -> [P_element014,O_element125]
  conduct = 2
  density = 1
  expand = 3
  formula = G4_DNA_MONOPHOSPHATE
  name = G4_DNA_MONOPHOSPHATE
  specific = 4
FEATURE [App::DocumentObjectGroupPython] H_element134  label="H_element : 081"  # scripted group (container) (typed FeaturePython)
  n = 10
  ref = H_element
FEATURE [App::DocumentObjectGroupPython] C_element144  label="C_element : 089"  # scripted group (container) (typed FeaturePython)
  n = 10
  ref = C_element
FEATURE [App::DocumentObjectGroupPython] N_element064  label="N_element : 036"  # scripted group (container) (typed FeaturePython)
  n = 5
  ref = N_element
FEATURE [App::DocumentObjectGroupPython] O_element126  label="O_element : 079"  # scripted group (container) (typed FeaturePython)
  n = 7
  ref = O_element
FEATURE [App::DocumentObjectGroupPython] P_element015  label="P_element : 004"  # scripted group (container) (typed FeaturePython)
  n = 1
  ref = P_element
FEATURE [App::DocumentObjectGroupPython] G4_DNA_A  # scripted group (container) (typed FeaturePython)
  Dunit = g/cm3
  Dvalue = 1
  Group = -> [H_element134,C_element144,N_element064,O_element126,P_element015]
  conduct = 2
  density = 1
  expand = 3
  formula = G4_DNA_A
  name = G4_DNA_A
  specific = 4
FEATURE [App::DocumentObjectGroupPython] H_element135  label="H_element : 082"  # scripted group (container) (typed FeaturePython)
  n = 10
  ref = H_element
FEATURE [App::DocumentObjectGroupPython] C_element145  label="C_element : 090"  # scripted group (container) (typed FeaturePython)
  n = 10
  ref = C_element
FEATURE [App::DocumentObjectGroupPython] N_element065  label="N_element : 037"  # scripted group (container) (typed FeaturePython)
  n = 5
  ref = N_element
FEATURE [App::DocumentObjectGroupPython] O_element127  label="O_element : 8"  # scripted group (container) (typed FeaturePython)
  n = 8
  ref = O_element
FEATURE [App::DocumentObjectGroupPython] P_element016  label="P_element : 005"  # scripted group (container) (typed FeaturePython)
  n = 1
  ref = P_element
FEATURE [App::DocumentObjectGroupPython] G4_DNA_G  # scripted group (container) (typed FeaturePython)
  Dunit = g/cm3
  Dvalue = 1
  Group = -> [H_element135,C_element145,N_element065,O_element127,P_element016]
  conduct = 2
  density = 1
  expand = 3
  formula = G4_DNA_G
  name = G4_DNA_G
  specific = 4
FEATURE [App::DocumentObjectGroupPython] H_element136  label="H_element : 083"  # scripted group (container) (typed FeaturePython)
  n = 10
  ref = H_element
FEATURE [App::DocumentObjectGroupPython] C_element146  label="C_element : 091"  # scripted group (container) (typed FeaturePython)
  n = 9
  ref = C_element
FEATURE [App::DocumentObjectGroupPython] N_element066  label="N_element : 038"  # scripted group (container) (typed FeaturePython)
  n = 3
  ref = N_element
FEATURE [App::DocumentObjectGroupPython] O_element128  label="O_element : 080"  # scripted group (container) (typed FeaturePython)
  n = 8
  ref = O_element
FEATURE [App::DocumentObjectGroupPython] P_element017  label="P_element : 006"  # scripted group (container) (typed FeaturePython)
  n = 1
  ref = P_element
FEATURE [App::DocumentObjectGroupPython] G4_DNA_C  # scripted group (container) (typed FeaturePython)
  Dunit = g/cm3
  Dvalue = 1
  Group = -> [H_element136,C_element146,N_element066,O_element128,P_element017]
  conduct = 2
  density = 1
  expand = 3
  formula = G4_DNA_C
  name = G4_DNA_C
  specific = 4
FEATURE [App::DocumentObjectGroupPython] H_element137  label="H_element : 084"  # scripted group (container) (typed FeaturePython)
  n = 9
  ref = H_element
FEATURE [App::DocumentObjectGroupPython] C_element147  label="C_element : 092"  # scripted group (container) (typed FeaturePython)
  n = 9
  ref = C_element
FEATURE [App::DocumentObjectGroupPython] N_element067  label="N_element : 039"  # scripted group (container) (typed FeaturePython)
  n = 2
  ref = N_element
FEATURE [App::DocumentObjectGroupPython] O_element129  label="O_element : 9"  # scripted group (container) (typed FeaturePython)
  n = 9
  ref = O_element
FEATURE [App::DocumentObjectGroupPython] P_element018  label="P_element : 007"  # scripted group (container) (typed FeaturePython)
  n = 1
  ref = P_element
FEATURE [App::DocumentObjectGroupPython] G4_DNA_U  # scripted group (container) (typed FeaturePython)
  Dunit = g/cm3
  Dvalue = 1
  Group = -> [H_element137,C_element147,N_element067,O_element129,P_element018]
  conduct = 2
  density = 1
  expand = 3
  formula = G4_DNA_U
  name = G4_DNA_U
  specific = 4
FEATURE [App::DocumentObjectGroupPython] H_element138  label="H_element : 085"  # scripted group (container) (typed FeaturePython)
  n = 11
  ref = H_element
FEATURE [App::DocumentObjectGroupPython] C_element148  label="C_element : 093"  # scripted group (container) (typed FeaturePython)
  n = 10
  ref = C_element
FEATURE [App::DocumentObjectGroupPython] N_element068  label="N_element : 040"  # scripted group (container) (typed FeaturePython)
  n = 2
  ref = N_element
FEATURE [App::DocumentObjectGroupPython] O_element130  label="O_element : 081"  # scripted group (container) (typed FeaturePython)
  n = 9
  ref = O_element
FEATURE [App::DocumentObjectGroupPython] P_element019  label="P_element : 008"  # scripted group (container) (typed FeaturePython)
  n = 1
  ref = P_element
FEATURE [App::DocumentObjectGroupPython] G4_DNA_MU  # scripted group (container) (typed FeaturePython)
  Dunit = g/cm3
  Dvalue = 1
  Group = -> [H_element138,C_element148,N_element068,O_element130,P_element019]
  conduct = 2
  density = 1
  expand = 3
  formula = G4_DNA_MU
  name = G4_DNA_MU
  specific = 4
FEATURE [App::DocumentObjectGroupPython] BioChemical  # scripted group (container) (typed FeaturePython)
  Group = -> [G4_CYTOSINE,G4_THYMINE,G4_URACIL,G4_DNA_ADENINE,G4_DNA_GUANINE,G4_DNA_CYTOSINE,G4_DNA_THYMINE,G4_DNA_URACIL,G4_DNA_ADENOSINE,G4_DNA_GUANOSINE,G4_DNA_CYTIDINE,G4_DNA_URIDINE,G4_DNA_METHYLURIDINE,G4_DNA_MONOPHOSPHATE,G4_DNA_A,G4_DNA_G,G4_DNA_C,G4_DNA_U,G4_DNA_MU]
FEATURE [App::DocumentObjectGroupPython] G4Materials  # scripted group (container) (typed FeaturePython)
  Group = -> [NIST,Element,HEP,Space,BioChemical]
  version = 1
FEATURE [App::DocumentObjectGroupPython] Geant4  # scripted group (container) (typed FeaturePython)
  Group = -> [G4Isotopes,G4Elements,G4Materials]
FEATURE [App::DocumentObjectGroupPython] Materials  # scripted group (container) (typed FeaturePython)
  Group = -> [Geant4]
FEATURE [Part::FeaturePython] GDMLBox_WorldBox  # WARN: FeaturePython — macro-defined, semantics opaque (R4)
  lunit = 2
  material = 7
  x = 26
  y = 26
  z = 31.2
FEATURE [Part::Cone] Cone
  Angle = 360
  AttacherType = Attacher::AttachEngine3D
  Height = 2
  Radius1 = 0
  Radius2 = 1
FEATURE [Part::Helix] Helix
  Angle = 0
  AttacherType = Attacher::AttachEngine3D
  Height = 20
  LocalCoord = 0
  Pitch = 8
  Radius = 10
  SegmentLength = 0
  Style = 1
FEATURE [Part::FeaturePython] PathArray  # WARN: FeaturePython — macro-defined, semantics opaque (R4)
  Align = false
  AlignMode = 0
  Base = -> Cone
  Count = 40
  EndOffset = 0
  ExtraTranslation = (0,0,0)
  ForceVertical = false
  PathObject = -> Helix
  StartOffset = 0
  TangentVector = (1,0,0)
  VerticalVector = (0,0,1)
FEATURE [App::Part] Part
  Group = -> [PathArray]
  Origin = -> Origin001
FEATURE [App::Part] worldVOL
  Group = -> [GDMLBox_WorldBox,Part]
  Origin = -> Origin
